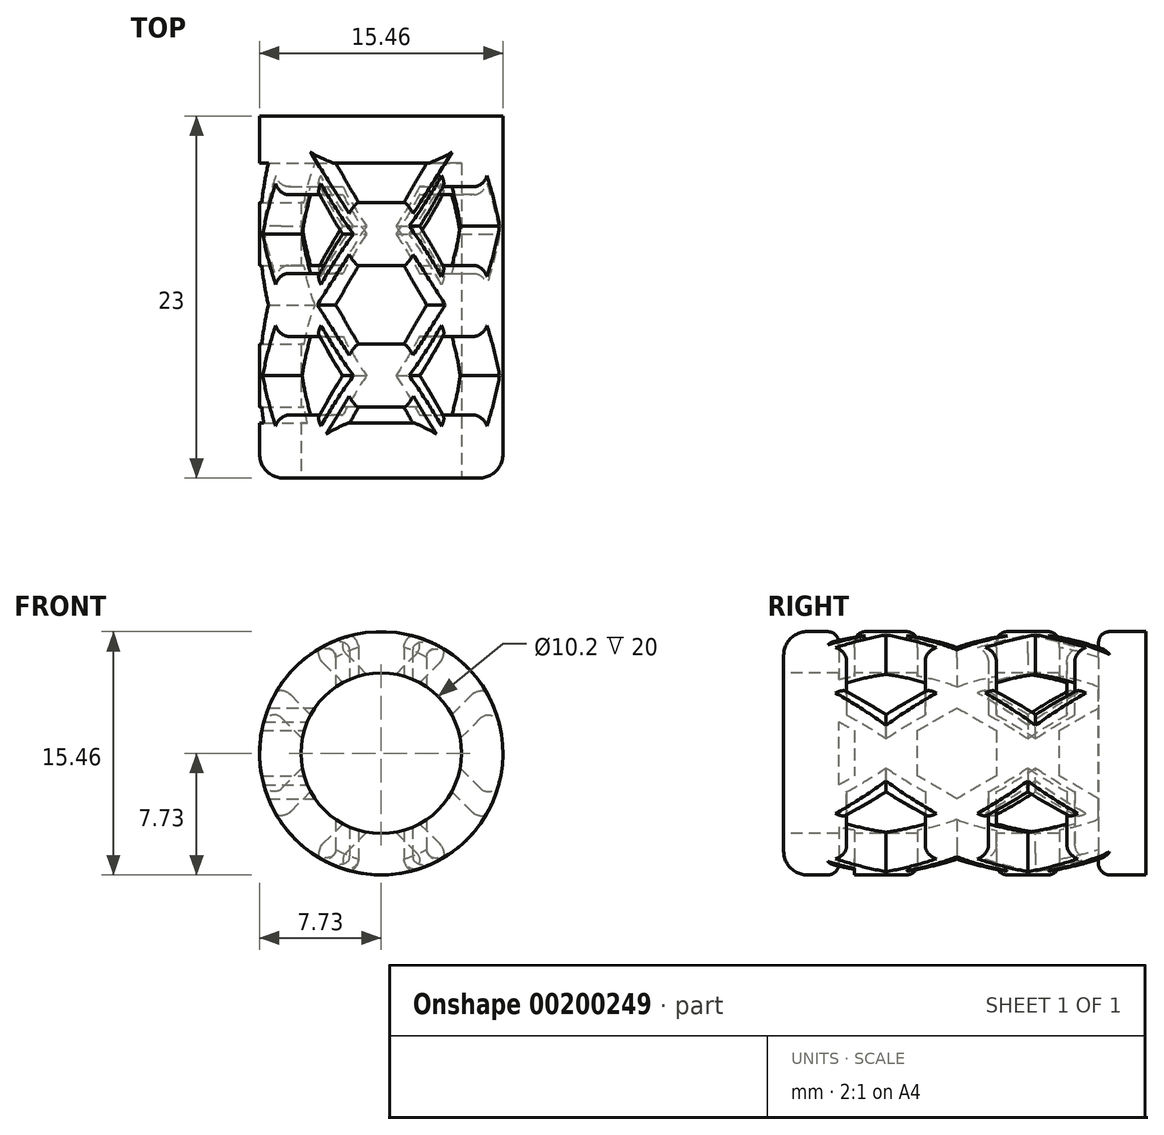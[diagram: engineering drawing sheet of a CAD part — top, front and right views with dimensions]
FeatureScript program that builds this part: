
annotation { "Feature Type Name" : "Feature", "Feature Type Description" : "" }
export const myFeature = defineFeature(function(context is Context, id is Id, definition is map)
    precondition{}
    {
        {
            var Q0;
            Q0=qCreatedBy(makeId("Front.planeOp"),FACE);
            var sketch = newSketch(context, id + "F0", { "sketchPlane" : qUnion([Q0])});
            skCircle(sketch, "E0", {"center": v(0, 0) * mm, "radius": 7.73 * mm});
            skSolve(sketch);
        }
        {
            var Q0;
            Q0=makeQuery(id+"F0.imprint","IMPRINT",FACE,{"disambiguationData":[TD([[makeQuery(id+"F0.imprint","IMPRINT",EDGE,{"derivedFrom":sQuery(id+"F0.wireOp",EDGE,"E0")}),1.0]])]});
            extrude(context, id + "F1", {"entities" : qUnion([Q0]), "oppositeDirection" : true, "depth" : 23 * mm, "offsetDistance" : 25 * mm});
        }
        {
            var Q0;
            Q0=makeQuery(id+"F1.opExtrude","CAP_FACE",FACE,{"disambiguationData":[OSD([sQuery(id+"F0.wireOp",EDGE,"E0")])],"isStart":true});
            var sketch = newSketch(context, id + "F2", { "sketchPlane" : qUnion([Q0])});
            skCircle(sketch, "E1", {"center": v(0, 0) * mm, "radius": 5.1 * mm});
            skSolve(sketch);
        }
        {
            var Q0;
            Q0=qSketchRegion(id+"F2",true);
            extrude(context, id + "F3", {"entities" : qUnion([Q0]), "operationType" : NewBodyOperationType.REMOVE, "oppositeDirection" : true, "depth" : 20 * mm, "offsetDistance" : 25 * mm});
        }
        {
            var Q0;
            Q0=qCreatedBy(makeId("Top.planeOp"),FACE);
            var sketch = newSketch(context, id + "F4", { "sketchPlane" : qUnion([Q0])});
            skLineSegment(sketch, "E2", {"start": v(0, 0) * mm, "end": v(0, 6.5) * mm, "construction": true});
            skLineSegment(sketch, "E3", {"start": v(0, 6.5) * mm, "end": v(0, 9) * mm, "construction": true});
            skCircle(sketch, "E4.cCircle", {"center": v(0, 6.5) * mm, "radius": 2.5 * mm, "construction": true});
            skLineSegment(sketch, "E4.0", {"start": v(-1.44, 9) * mm, "end": v(1.44, 9) * mm});
            skLineSegment(sketch, "E4.1", {"start": v(1.44, 9) * mm, "end": v(2.89, 6.5) * mm});
            skLineSegment(sketch, "E4.2", {"start": v(2.89, 6.5) * mm, "end": v(1.44, 4) * mm});
            skLineSegment(sketch, "E4.3", {"start": v(1.44, 4) * mm, "end": v(-1.44, 4) * mm});
            skLineSegment(sketch, "E4.4", {"start": v(-1.44, 4) * mm, "end": v(-2.89, 6.5) * mm});
            skLineSegment(sketch, "E4.5", {"start": v(-2.89, 6.5) * mm, "end": v(-1.44, 9) * mm});
            skPoint(sketch, "E4.0.midPoint", {"position": v(0, 9) * mm});
            skLineSegment(sketch, "E5.0.1.0", {"start": v(-2.89, 15.5) * mm, "end": v(-1.44, 18) * mm});
            skLineSegment(sketch, "E5.0.1.1", {"start": v(1.44, 13) * mm, "end": v(-1.44, 13) * mm});
            skLineSegment(sketch, "E5.0.1.2", {"start": v(2.89, 15.5) * mm, "end": v(1.44, 13) * mm});
            skLineSegment(sketch, "E5.0.1.3", {"start": v(1.44, 18) * mm, "end": v(2.89, 15.5) * mm});
            skLineSegment(sketch, "E5.0.1.4", {"start": v(-1.44, 18) * mm, "end": v(1.44, 18) * mm});
            skLineSegment(sketch, "E5.0.1.5", {"start": v(0, 15.5) * mm, "end": v(0, 18) * mm, "construction": true});
            skPoint(sketch, "E5.0.1.6", {"position": v(0, 18) * mm});
            skLineSegment(sketch, "E5.0.1.7", {"start": v(-1.44, 13) * mm, "end": v(-2.89, 15.5) * mm});
            skCircle(sketch, "E5.0.1.8", {"center": v(0, 15.5) * mm, "radius": 2.5 * mm, "construction": true});
            skLineSegment(sketch, "E5.direction1", {"start": v(-1.44, 4) * mm, "end": v(23.56, 4) * mm, "construction": true});
            skLineSegment(sketch, "E5.direction2", {"start": v(-1.44, 4) * mm, "end": v(-1.44, 13) * mm, "construction": true});
            skSolve(sketch);
        }
        {
            var Q0;
            Q0=qSketchRegion(id+"F4",true);
            extrude(context, id + "F5", {"entities" : qUnion([Q0]), "operationType" : NewBodyOperationType.REMOVE, "endBound" : BoundingType.SYMMETRIC, "depth" : 25 * mm});
        }
        {
            var Q0;
            Q0=qCreatedBy(makeId("Right.planeOp"),FACE);
            var sketch = newSketch(context, id + "F6", { "sketchPlane" : qUnion([Q0])});
            skLineSegment(sketch, "E6", {"start": v(0, 0) * mm, "end": v(6.5, 0) * mm, "construction": true});
            skLineSegment(sketch, "E7", {"start": v(6.5, 0) * mm, "end": v(9, 0) * mm, "construction": true});
            skCircle(sketch, "E8.cCircle", {"center": v(6.5, 0) * mm, "radius": 2.5 * mm, "construction": true});
            skLineSegment(sketch, "E8.0", {"start": v(9, 1.44) * mm, "end": v(9, -1.44) * mm});
            skLineSegment(sketch, "E8.1", {"start": v(9, -1.44) * mm, "end": v(6.5, -2.89) * mm});
            skLineSegment(sketch, "E8.2", {"start": v(6.5, -2.89) * mm, "end": v(4, -1.44) * mm});
            skLineSegment(sketch, "E8.3", {"start": v(4, -1.44) * mm, "end": v(4, 1.44) * mm});
            skLineSegment(sketch, "E8.4", {"start": v(4, 1.44) * mm, "end": v(6.5, 2.89) * mm});
            skLineSegment(sketch, "E8.5", {"start": v(6.5, 2.89) * mm, "end": v(9, 1.44) * mm});
            skPoint(sketch, "E8.0.midPoint", {"position": v(9, 0) * mm});
            skLineSegment(sketch, "E9", {"start": v(9, 0) * mm, "end": v(13.5, 0) * mm, "construction": true});
            skLineSegment(sketch, "E10", {"start": v(13.5, 0) * mm, "end": v(16, 0) * mm, "construction": true});
            skCircle(sketch, "E11.cCircle", {"center": v(16, 0) * mm, "radius": 2.5 * mm, "construction": true});
            skLineSegment(sketch, "E11.0", {"start": v(13.5, -1.44) * mm, "end": v(13.5, 1.44) * mm});
            skLineSegment(sketch, "E11.1", {"start": v(13.5, 1.44) * mm, "end": v(16, 2.89) * mm});
            skLineSegment(sketch, "E11.2", {"start": v(16, 2.89) * mm, "end": v(18.5, 1.44) * mm});
            skLineSegment(sketch, "E11.3", {"start": v(18.5, 1.44) * mm, "end": v(18.5, -1.44) * mm});
            skLineSegment(sketch, "E11.4", {"start": v(18.5, -1.44) * mm, "end": v(16, -2.89) * mm});
            skLineSegment(sketch, "E11.5", {"start": v(16, -2.89) * mm, "end": v(13.5, -1.44) * mm});
            skPoint(sketch, "E11.0.midPoint", {"position": v(13.5, 0) * mm});
            skSolve(sketch);
        }
        {
            var Q0;
            Q0=qSketchRegion(id+"F6",true);
            extrude(context, id + "F7", {"entities" : qUnion([Q0]), "operationType" : NewBodyOperationType.REMOVE, "endBound" : BoundingType.SYMMETRIC, "oppositeDirection" : true, "depth" : 25 * mm});
        }
        {
            var Q0;
            Q0=makeQuery(id+"F1.opExtrude","SWEPT_BODY",BODY,{"disambiguationData":[OSD([sQuery(id+"F0.wireOp",EDGE,"E0")])]});
            var Q1;
            Q1=makeQuery(id+"F1.opExtrude","SWEPT_FACE",FACE,{"disambiguationData":[OSD([sQuery(id+"F0.wireOp",EDGE,"E0")])]});
            transform(context, id + "F8", {"entities" : qUnion([Q0]), "transformType" : TransformType.ROTATION, "transformAxis" : qUnion([Q1]), "angle" : 45 * degree, "makeCopy" : false});
        }
        {
            var Q0;
            Q0=qCreatedBy(makeId("Top.planeOp"),FACE);
            var sketch = newSketch(context, id + "F9", { "sketchPlane" : qUnion([Q0])});
            skLineSegment(sketch, "E12", {"start": v(0, 0) * mm, "end": v(0, 11) * mm, "construction": true});
            skLineSegment(sketch, "E13", {"start": v(0, 11) * mm, "end": v(0, 13.5) * mm, "construction": true});
            skCircle(sketch, "E14.cCircle", {"center": v(0, 11) * mm, "radius": 2.5 * mm, "construction": true});
            skLineSegment(sketch, "E14.0", {"start": v(-1.44, 13.5) * mm, "end": v(1.44, 13.5) * mm});
            skLineSegment(sketch, "E14.1", {"start": v(1.44, 13.5) * mm, "end": v(2.89, 11) * mm});
            skLineSegment(sketch, "E14.2", {"start": v(2.89, 11) * mm, "end": v(1.44, 8.5) * mm});
            skLineSegment(sketch, "E14.3", {"start": v(1.44, 8.5) * mm, "end": v(-1.44, 8.5) * mm});
            skLineSegment(sketch, "E14.4", {"start": v(-1.44, 8.5) * mm, "end": v(-2.89, 11) * mm});
            skLineSegment(sketch, "E14.5", {"start": v(-2.89, 11) * mm, "end": v(-1.44, 13.5) * mm});
            skPoint(sketch, "E14.0.midPoint", {"position": v(0, 13.5) * mm});
            skLineSegment(sketch, "E15.0.1.0", {"start": v(0, 20) * mm, "end": v(0, 22.5) * mm, "construction": true});
            skPoint(sketch, "E15.0.1.1", {"position": v(0, 22.5) * mm});
            skLineSegment(sketch, "E15.0.1.2", {"start": v(1.44, 17.5) * mm, "end": v(-1.44, 17.5) * mm});
            skLineSegment(sketch, "E15.0.1.3", {"start": v(2.89, 20) * mm, "end": v(1.44, 17.5) * mm});
            skLineSegment(sketch, "E15.0.1.6", {"start": v(-1.44, 17.5) * mm, "end": v(-2.89, 20) * mm});
            skCircle(sketch, "E15.0.1.8", {"center": v(0, 20) * mm, "radius": 2.5 * mm, "construction": true});
            skLineSegment(sketch, "E15.direction1", {"start": v(-1.44, 8.5) * mm, "end": v(23.56, 8.5) * mm, "construction": true});
            skLineSegment(sketch, "E15.direction2", {"start": v(-1.44, 8.5) * mm, "end": v(-1.44, 17.5) * mm, "construction": true});
            skLineSegment(sketch, "E16", {"start": v(0, 119) * mm, "end": v(0, 128) * mm, "construction": true});
            skCircle(sketch, "E17.cCircle", {"center": v(0, 128) * mm, "radius": 2.5 * mm, "construction": true});
            skLineSegment(sketch, "E17.3", {"start": v(1.44, 125.5) * mm, "end": v(-1.44, 125.5) * mm});
            skPoint(sketch, "E17.0.midPoint", {"position": v(0, 130.5) * mm});
            skLineSegment(sketch, "E18", {"start": v(0, 126.5) * mm, "end": v(0, 125.5) * mm, "construction": true});
            skLineSegment(sketch, "E19", {"start": v(0, 126.5) * mm, "end": v(2, 126.5) * mm});
            skLineSegment(sketch, "E20", {"start": v(0, 126.5) * mm, "end": v(-2, 126.5) * mm});
            skLineSegment(sketch, "E21", {"start": v(-2, 126.5) * mm, "end": v(-1.44, 125.5) * mm});
            skLineSegment(sketch, "E22", {"start": v(1.44, 125.5) * mm, "end": v(2, 126.5) * mm});
            skLineSegment(sketch, "E23", {"start": v(0, 11) * mm, "end": v(0, 2) * mm, "construction": true});
            skCircle(sketch, "E24.cCircle", {"center": v(0, 2) * mm, "radius": 2.5 * mm, "construction": true});
            skLineSegment(sketch, "E24.3", {"start": v(-1.44, 4.5) * mm, "end": v(1.44, 4.5) * mm});
            skPoint(sketch, "E24.0.midPoint", {"position": v(0, -0.5) * mm});
            skLineSegment(sketch, "E25", {"start": v(0, 3.5) * mm, "end": v(0, 4.5) * mm, "construction": true});
            skLineSegment(sketch, "E26", {"start": v(0, 3.5) * mm, "end": v(-2, 3.5) * mm});
            skLineSegment(sketch, "E27", {"start": v(0, 3.5) * mm, "end": v(2, 3.5) * mm});
            skLineSegment(sketch, "E28", {"start": v(-2, 3.5) * mm, "end": v(-1.44, 4.5) * mm});
            skLineSegment(sketch, "E29", {"start": v(2, 3.5) * mm, "end": v(1.44, 4.5) * mm});
            skLineSegment(sketch, "E30", {"start": v(2.89, 20) * mm, "end": v(-2.89, 20) * mm});
            skSolve(sketch);
        }
        {
            var Q0;
            Q0=qSketchRegion(id+"F9",true);
            extrude(context, id + "F10", {"entities" : qUnion([Q0]), "operationType" : NewBodyOperationType.REMOVE, "endBound" : BoundingType.SYMMETRIC, "depth" : 25 * mm});
        }
        {
            var Q0;
            Q0=qCreatedBy(makeId("Right.planeOp"),FACE);
            var sketch = newSketch(context, id + "F11", { "sketchPlane" : qUnion([Q0])});
            skLineSegment(sketch, "E31", {"start": v(0, 0) * mm, "end": v(11, 0) * mm, "construction": true});
            skLineSegment(sketch, "E32", {"start": v(13.5, 0) * mm, "end": v(11, 0) * mm, "construction": true});
            skCircle(sketch, "E33.cCircle", {"center": v(11, 0) * mm, "radius": 2.5 * mm, "construction": true});
            skLineSegment(sketch, "E33.0", {"start": v(13.5, 1.44) * mm, "end": v(13.5, -1.44) * mm});
            skLineSegment(sketch, "E33.1", {"start": v(13.5, -1.44) * mm, "end": v(11, -2.89) * mm});
            skLineSegment(sketch, "E33.2", {"start": v(11, -2.89) * mm, "end": v(8.5, -1.44) * mm});
            skLineSegment(sketch, "E33.3", {"start": v(8.5, -1.44) * mm, "end": v(8.5, 1.44) * mm});
            skLineSegment(sketch, "E33.4", {"start": v(8.5, 1.44) * mm, "end": v(11, 2.89) * mm});
            skLineSegment(sketch, "E33.5", {"start": v(11, 2.89) * mm, "end": v(13.5, 1.44) * mm});
            skPoint(sketch, "E33.0.midPoint", {"position": v(13.5, 0) * mm});
            skLineSegment(sketch, "E34", {"start": v(13.5, 0) * mm, "end": v(20, 0) * mm, "construction": true});
            skLineSegment(sketch, "E35", {"start": v(20, 0) * mm, "end": v(22.5, 0) * mm, "construction": true});
            skCircle(sketch, "E36.cCircle", {"center": v(20, 0) * mm, "radius": 2.5 * mm, "construction": true});
            skLineSegment(sketch, "E36.2", {"start": v(20, -2.89) * mm, "end": v(17.5, -1.44) * mm});
            skLineSegment(sketch, "E36.3", {"start": v(17.5, -1.44) * mm, "end": v(17.5, 1.44) * mm});
            skLineSegment(sketch, "E36.4", {"start": v(17.5, 1.44) * mm, "end": v(20, 2.89) * mm});
            skPoint(sketch, "E36.0.midPoint", {"position": v(22.5, 0) * mm});
            skLineSegment(sketch, "E37", {"start": v(2, 0) * mm, "end": v(11, 0) * mm, "construction": true});
            skCircle(sketch, "E38.cCircle", {"center": v(2, 0) * mm, "radius": 2.5 * mm, "construction": true});
            skLineSegment(sketch, "E38.3", {"start": v(4.5, 1.44) * mm, "end": v(4.5, -1.44) * mm});
            skPoint(sketch, "E38.0.midPoint", {"position": v(-0.5, 0) * mm});
            skLineSegment(sketch, "E39", {"start": v(3.5, 0) * mm, "end": v(4.5, 0) * mm, "construction": true});
            skLineSegment(sketch, "E40", {"start": v(3.5, 0) * mm, "end": v(3.5, 2) * mm});
            skLineSegment(sketch, "E41", {"start": v(3.5, 0) * mm, "end": v(3.5, -2) * mm});
            skLineSegment(sketch, "E42", {"start": v(3.5, 2) * mm, "end": v(4.5, 1.44) * mm});
            skLineSegment(sketch, "E43", {"start": v(3.5, -2) * mm, "end": v(4.5, -1.44) * mm});
            skLineSegment(sketch, "E44", {"start": v(20, 2.89) * mm, "end": v(20, -2.89) * mm});
            skSolve(sketch);
        }
        {
            var Q0;
            Q0=qSketchRegion(id+"F11",true);
            extrude(context, id + "F12", {"entities" : qUnion([Q0]), "operationType" : NewBodyOperationType.REMOVE, "oppositeDirection" : true, "depth" : 25 * mm});
        }
        {
            var Q0;
            Q0=makeQuery(id+"F1.opExtrude","CAP_EDGE",EDGE,{"disambiguationData":[OSD([sQuery(id+"F0.wireOp",EDGE,"E0")])],"isStart":true});
            fillet(context, id + "F13", {"entities" : qUnion([Q0]), "radius" : 1.5 * mm, "tangentPropagation" : true, "allowEdgeOverflow" : false});
        }
        {
            var Q0;
            Q0=makeQuery(id+"F5.boolean.opBoolean","INTERSECT",EDGE,{"disambiguationData":[OD(0.0)],"derivedFrom":[makeQuery(id+"F1.opExtrude","SWEPT_FACE",FACE,{"disambiguationData":[OSD([sQuery(id+"F0.wireOp",EDGE,"E0")])]}),makeQuery(id+"F5.opExtrude","SWEPT_FACE",FACE,{"disambiguationData":[OSD([sQuery(id+"F4.wireOp",EDGE,"b579cf08-57c8-4be4-a64a-6a7c8f7f1ba5")])]})]});
            var Q1;
            Q1=makeQuery(id+"F5.boolean.opBoolean","INTERSECT",EDGE,{"disambiguationData":[OD(0.0)],"derivedFrom":[makeQuery(id+"F1.opExtrude","SWEPT_FACE",FACE,{"disambiguationData":[OSD([sQuery(id+"F0.wireOp",EDGE,"E0")])]}),makeQuery(id+"F5.opExtrude","SWEPT_FACE",FACE,{"disambiguationData":[OSD([sQuery(id+"F4.wireOp",EDGE,"bcb0f5b9-98e4-4035-bb5b-1a8c92403a19")])]})]});
            var Q2;
            Q2=makeQuery(id+"F5.boolean.opBoolean","INTERSECT",EDGE,{"disambiguationData":[OD(0.0)],"derivedFrom":[makeQuery(id+"F1.opExtrude","SWEPT_FACE",FACE,{"disambiguationData":[OSD([sQuery(id+"F0.wireOp",EDGE,"E0")])]}),makeQuery(id+"F5.opExtrude","SWEPT_FACE",FACE,{"disambiguationData":[OSD([sQuery(id+"F4.wireOp",EDGE,"09477fc4-9d29-4f20-8901-aec53dcd1546")])]})]});
            var Q3;
            Q3=makeQuery(id+"F5.boolean.opBoolean","INTERSECT",EDGE,{"disambiguationData":[OD(0.0)],"derivedFrom":[makeQuery(id+"F1.opExtrude","SWEPT_FACE",FACE,{"disambiguationData":[OSD([sQuery(id+"F0.wireOp",EDGE,"E0")])]}),makeQuery(id+"F5.opExtrude","SWEPT_FACE",FACE,{"disambiguationData":[OSD([sQuery(id+"F4.wireOp",EDGE,"92af876a-0958-4a7c-97b2-f4e8acbef095")])]})]});
            var Q4;
            Q4=makeQuery(id+"F5.boolean.opBoolean","INTERSECT",EDGE,{"disambiguationData":[OD(0.0)],"derivedFrom":[makeQuery(id+"F1.opExtrude","SWEPT_FACE",FACE,{"disambiguationData":[OSD([sQuery(id+"F0.wireOp",EDGE,"E0")])]}),makeQuery(id+"F5.opExtrude","SWEPT_FACE",FACE,{"disambiguationData":[OSD([sQuery(id+"F4.wireOp",EDGE,"67b481ec-10fe-46d3-8faa-ebe6010fe4f1")])]})]});
            var Q5;
            Q5=makeQuery(id+"F5.boolean.opBoolean","INTERSECT",EDGE,{"disambiguationData":[OD(0.0)],"derivedFrom":[makeQuery(id+"F1.opExtrude","SWEPT_FACE",FACE,{"disambiguationData":[OSD([sQuery(id+"F0.wireOp",EDGE,"E0")])]}),makeQuery(id+"F5.opExtrude","SWEPT_FACE",FACE,{"disambiguationData":[OSD([sQuery(id+"F4.wireOp",EDGE,"aca02d5f-46a9-486e-88e3-eb9aae4273e8")])]})]});
            var Q6;
            Q6=makeQuery(id+"F5.boolean.opBoolean","INTERSECT",EDGE,{"disambiguationData":[OD(0.0)],"derivedFrom":[makeQuery(id+"F1.opExtrude","SWEPT_FACE",FACE,{"disambiguationData":[OSD([sQuery(id+"F0.wireOp",EDGE,"E0")])]}),makeQuery(id+"F5.opExtrude","SWEPT_FACE",FACE,{"disambiguationData":[OSD([sQuery(id+"F4.wireOp",EDGE,"76385219-3691-4f38-9da5-edf1140a4629")])]})]});
            var Q7;
            Q7=makeQuery(id+"F5.boolean.opBoolean","INTERSECT",EDGE,{"disambiguationData":[OD(0.0)],"derivedFrom":[makeQuery(id+"F1.opExtrude","SWEPT_FACE",FACE,{"disambiguationData":[OSD([sQuery(id+"F0.wireOp",EDGE,"E0")])]}),makeQuery(id+"F5.opExtrude","SWEPT_FACE",FACE,{"disambiguationData":[OSD([sQuery(id+"F4.wireOp",EDGE,"30311b2f-ed17-4601-a199-a8278ef993fb")])]})]});
            var Q8;
            Q8=makeQuery(id+"F5.boolean.opBoolean","INTERSECT",EDGE,{"disambiguationData":[OD(0.0)],"derivedFrom":[makeQuery(id+"F1.opExtrude","SWEPT_FACE",FACE,{"disambiguationData":[OSD([sQuery(id+"F0.wireOp",EDGE,"E0")])]}),makeQuery(id+"F5.opExtrude","SWEPT_FACE",FACE,{"disambiguationData":[OSD([sQuery(id+"F4.wireOp",EDGE,"ed008b68-955d-4315-9cc0-8abb2c6860b0")])]})]});
            var Q9;
            Q9=makeQuery(id+"F5.boolean.opBoolean","INTERSECT",EDGE,{"disambiguationData":[OD(0.0)],"derivedFrom":[makeQuery(id+"F1.opExtrude","SWEPT_FACE",FACE,{"disambiguationData":[OSD([sQuery(id+"F0.wireOp",EDGE,"E0")])]}),makeQuery(id+"F5.opExtrude","SWEPT_FACE",FACE,{"disambiguationData":[OSD([sQuery(id+"F4.wireOp",EDGE,"efc5e5b1-0746-45f0-90e3-bd883f3492f4")])]})]});
            var Q10;
            Q10=makeQuery(id+"F5.boolean.opBoolean","INTERSECT",EDGE,{"disambiguationData":[OD(0.0)],"derivedFrom":[makeQuery(id+"F1.opExtrude","SWEPT_FACE",FACE,{"disambiguationData":[OSD([sQuery(id+"F0.wireOp",EDGE,"E0")])]}),makeQuery(id+"F5.opExtrude","SWEPT_FACE",FACE,{"disambiguationData":[OSD([sQuery(id+"F4.wireOp",EDGE,"562b9cc4-530f-4157-bc84-2c37910fa221")])]})]});
            var Q11;
            Q11=makeQuery(id+"F5.boolean.opBoolean","INTERSECT",EDGE,{"disambiguationData":[OD(0.0)],"derivedFrom":[makeQuery(id+"F1.opExtrude","SWEPT_FACE",FACE,{"disambiguationData":[OSD([sQuery(id+"F0.wireOp",EDGE,"E0")])]}),makeQuery(id+"F5.opExtrude","SWEPT_FACE",FACE,{"disambiguationData":[OSD([sQuery(id+"F4.wireOp",EDGE,"ab9f0dd0-8a88-45b5-9e6c-47f07906d12f")])]})]});
            var Q12;
            Q12=makeQuery(id+"F5.boolean.opBoolean","INTERSECT",EDGE,{"disambiguationData":[OD(0.0)],"derivedFrom":[makeQuery(id+"F1.opExtrude","SWEPT_FACE",FACE,{"disambiguationData":[OSD([sQuery(id+"F0.wireOp",EDGE,"E0")])]}),makeQuery(id+"F5.opExtrude","SWEPT_FACE",FACE,{"disambiguationData":[OSD([sQuery(id+"F4.wireOp",EDGE,"5e54ec67-0438-4ccb-ab1e-fb0c5627ff7a")])]})]});
            var Q13;
            Q13=makeQuery(id+"F5.boolean.opBoolean","INTERSECT",EDGE,{"disambiguationData":[OD(0.0)],"derivedFrom":[makeQuery(id+"F1.opExtrude","SWEPT_FACE",FACE,{"disambiguationData":[OSD([sQuery(id+"F0.wireOp",EDGE,"E0")])]}),makeQuery(id+"F5.opExtrude","SWEPT_FACE",FACE,{"disambiguationData":[OSD([sQuery(id+"F4.wireOp",EDGE,"1da9000e-137c-457e-9dd6-58b65176467c")])]})]});
            var Q14;
            Q14=makeQuery(id+"F5.boolean.opBoolean","INTERSECT",EDGE,{"disambiguationData":[OD(0.0)],"derivedFrom":[makeQuery(id+"F1.opExtrude","SWEPT_FACE",FACE,{"disambiguationData":[OSD([sQuery(id+"F0.wireOp",EDGE,"E0")])]}),makeQuery(id+"F5.opExtrude","SWEPT_FACE",FACE,{"disambiguationData":[OSD([sQuery(id+"F4.wireOp",EDGE,"15ec9440-3994-4756-befc-73e6937f9073")])]})]});
            var Q15;
            Q15=makeQuery(id+"F5.boolean.opBoolean","INTERSECT",EDGE,{"disambiguationData":[OD(0.0)],"derivedFrom":[makeQuery(id+"F1.opExtrude","SWEPT_FACE",FACE,{"disambiguationData":[OSD([sQuery(id+"F0.wireOp",EDGE,"E0")])]}),makeQuery(id+"F5.opExtrude","SWEPT_FACE",FACE,{"disambiguationData":[OSD([sQuery(id+"F4.wireOp",EDGE,"70ca714e-c3bb-4dc2-844f-e69955e1961d")])]})]});
            var Q16;
            Q16=makeQuery(id+"F5.boolean.opBoolean","INTERSECT",EDGE,{"disambiguationData":[OD(0.0)],"derivedFrom":[makeQuery(id+"F1.opExtrude","SWEPT_FACE",FACE,{"disambiguationData":[OSD([sQuery(id+"F0.wireOp",EDGE,"E0")])]}),makeQuery(id+"F5.opExtrude","SWEPT_FACE",FACE,{"disambiguationData":[OSD([sQuery(id+"F4.wireOp",EDGE,"b9a5c8a8-e1c1-4ccb-a6a4-30bc00998619")])]})]});
            var Q17;
            Q17=makeQuery(id+"F5.boolean.opBoolean","INTERSECT",EDGE,{"disambiguationData":[OD(0.0)],"derivedFrom":[makeQuery(id+"F1.opExtrude","SWEPT_FACE",FACE,{"disambiguationData":[OSD([sQuery(id+"F0.wireOp",EDGE,"E0")])]}),makeQuery(id+"F5.opExtrude","SWEPT_FACE",FACE,{"disambiguationData":[OSD([sQuery(id+"F4.wireOp",EDGE,"66c2d1b9-9082-457f-8158-46fefb0d0b5d")])]})]});
            var Q18;
            Q18=makeQuery(id+"F5.boolean.opBoolean","INTERSECT",EDGE,{"disambiguationData":[OD(0.0)],"derivedFrom":[makeQuery(id+"F1.opExtrude","SWEPT_FACE",FACE,{"disambiguationData":[OSD([sQuery(id+"F0.wireOp",EDGE,"E0")])]}),makeQuery(id+"F5.opExtrude","SWEPT_FACE",FACE,{"disambiguationData":[OSD([sQuery(id+"F4.wireOp",EDGE,"fd9b85d0-086e-4753-9286-7d80f3d11dd9")])]})]});
            var Q19;
            Q19=makeQuery(id+"F5.boolean.opBoolean","INTERSECT",EDGE,{"disambiguationData":[OD(0.0)],"derivedFrom":[makeQuery(id+"F1.opExtrude","SWEPT_FACE",FACE,{"disambiguationData":[OSD([sQuery(id+"F0.wireOp",EDGE,"E0")])]}),makeQuery(id+"F5.opExtrude","SWEPT_FACE",FACE,{"disambiguationData":[OSD([sQuery(id+"F4.wireOp",EDGE,"82180203-eaff-47f3-b606-d8d7c32d142f")])]})]});
            var Q20;
            Q20=makeQuery(id+"F5.boolean.opBoolean","INTERSECT",EDGE,{"disambiguationData":[OD(0.0)],"derivedFrom":[makeQuery(id+"F1.opExtrude","SWEPT_FACE",FACE,{"disambiguationData":[OSD([sQuery(id+"F0.wireOp",EDGE,"E0")])]}),makeQuery(id+"F5.opExtrude","SWEPT_FACE",FACE,{"disambiguationData":[OSD([sQuery(id+"F4.wireOp",EDGE,"536ab4de-4fb2-4d7d-9807-1d714ccadb66")])]})]});
            var Q21;
            Q21=makeQuery(id+"F5.boolean.opBoolean","INTERSECT",EDGE,{"disambiguationData":[OD(0.0)],"derivedFrom":[makeQuery(id+"F1.opExtrude","SWEPT_FACE",FACE,{"disambiguationData":[OSD([sQuery(id+"F0.wireOp",EDGE,"E0")])]}),makeQuery(id+"F5.opExtrude","SWEPT_FACE",FACE,{"disambiguationData":[OSD([sQuery(id+"F4.wireOp",EDGE,"c5cda94b-8dbb-4131-8629-d94229ce36f8")])]})]});
            var Q22;
            Q22=makeQuery(id+"F5.boolean.opBoolean","INTERSECT",EDGE,{"disambiguationData":[OD(0.0)],"derivedFrom":[makeQuery(id+"F1.opExtrude","SWEPT_FACE",FACE,{"disambiguationData":[OSD([sQuery(id+"F0.wireOp",EDGE,"E0")])]}),makeQuery(id+"F5.opExtrude","SWEPT_FACE",FACE,{"disambiguationData":[OSD([sQuery(id+"F4.wireOp",EDGE,"b8538754-f3f1-4cf7-bfe9-078eb6985bef")])]})]});
            var Q23;
            Q23=makeQuery(id+"F5.boolean.opBoolean","INTERSECT",EDGE,{"disambiguationData":[OD(0.0)],"derivedFrom":[makeQuery(id+"F1.opExtrude","SWEPT_FACE",FACE,{"disambiguationData":[OSD([sQuery(id+"F0.wireOp",EDGE,"E0")])]}),makeQuery(id+"F5.opExtrude","SWEPT_FACE",FACE,{"disambiguationData":[OSD([sQuery(id+"F4.wireOp",EDGE,"9e1b2bd2-a8a3-4caa-b598-0f2db5d1325d")])]})]});
            var Q24;
            Q24=makeQuery(id+"F5.boolean.opBoolean","INTERSECT",EDGE,{"disambiguationData":[OD(0.0)],"derivedFrom":[makeQuery(id+"F1.opExtrude","SWEPT_FACE",FACE,{"disambiguationData":[OSD([sQuery(id+"F0.wireOp",EDGE,"E0")])]}),makeQuery(id+"F5.opExtrude","SWEPT_FACE",FACE,{"disambiguationData":[OSD([sQuery(id+"F4.wireOp",EDGE,"c0d87fc6-e010-4d73-961e-dfed47c8a1b3")])]})]});
            var Q25;
            Q25=makeQuery(id+"F5.boolean.opBoolean","INTERSECT",EDGE,{"disambiguationData":[OD(0.0)],"derivedFrom":[makeQuery(id+"F1.opExtrude","SWEPT_FACE",FACE,{"disambiguationData":[OSD([sQuery(id+"F0.wireOp",EDGE,"E0")])]}),makeQuery(id+"F5.opExtrude","SWEPT_FACE",FACE,{"disambiguationData":[OSD([sQuery(id+"F4.wireOp",EDGE,"14d064f9-5360-4d18-9d9e-82328bf9daba")])]})]});
            var Q26;
            Q26=makeQuery(id+"F5.boolean.opBoolean","INTERSECT",EDGE,{"disambiguationData":[OD(0.0)],"derivedFrom":[makeQuery(id+"F1.opExtrude","SWEPT_FACE",FACE,{"disambiguationData":[OSD([sQuery(id+"F0.wireOp",EDGE,"E0")])]}),makeQuery(id+"F5.opExtrude","SWEPT_FACE",FACE,{"disambiguationData":[OSD([sQuery(id+"F4.wireOp",EDGE,"b60fa973-c727-4668-bfa0-a1e16f7a99aa")])]})]});
            var Q27;
            Q27=makeQuery(id+"F5.boolean.opBoolean","INTERSECT",EDGE,{"disambiguationData":[OD(0.0)],"derivedFrom":[makeQuery(id+"F1.opExtrude","SWEPT_FACE",FACE,{"disambiguationData":[OSD([sQuery(id+"F0.wireOp",EDGE,"E0")])]}),makeQuery(id+"F5.opExtrude","SWEPT_FACE",FACE,{"disambiguationData":[OSD([sQuery(id+"F4.wireOp",EDGE,"978e1622-7887-4f07-a91b-81f9d5efcfbf")])]})]});
            var Q28;
            Q28=makeQuery(id+"F5.boolean.opBoolean","INTERSECT",EDGE,{"disambiguationData":[OD(0.0)],"derivedFrom":[makeQuery(id+"F1.opExtrude","SWEPT_FACE",FACE,{"disambiguationData":[OSD([sQuery(id+"F0.wireOp",EDGE,"E0")])]}),makeQuery(id+"F5.opExtrude","SWEPT_FACE",FACE,{"disambiguationData":[OSD([sQuery(id+"F4.wireOp",EDGE,"d0a2849f-a89e-4989-ab6e-8e188e140a90")])]})]});
            var Q29;
            Q29=makeQuery(id+"F5.boolean.opBoolean","INTERSECT",EDGE,{"disambiguationData":[OD(0.0)],"derivedFrom":[makeQuery(id+"F1.opExtrude","SWEPT_FACE",FACE,{"disambiguationData":[OSD([sQuery(id+"F0.wireOp",EDGE,"E0")])]}),makeQuery(id+"F5.opExtrude","SWEPT_FACE",FACE,{"disambiguationData":[OSD([sQuery(id+"F4.wireOp",EDGE,"f55199c0-7004-4acb-b4c7-226994b61401")])]})]});
            var Q30;
            Q30=makeQuery(id+"F5.boolean.opBoolean","INTERSECT",EDGE,{"disambiguationData":[OD(0.0)],"derivedFrom":[makeQuery(id+"F1.opExtrude","SWEPT_FACE",FACE,{"disambiguationData":[OSD([sQuery(id+"F0.wireOp",EDGE,"E0")])]}),makeQuery(id+"F5.opExtrude","SWEPT_FACE",FACE,{"disambiguationData":[OSD([sQuery(id+"F4.wireOp",EDGE,"8a1b3b7c-f627-453a-8324-eadb2e6b2aa6")])]})]});
            var Q31;
            Q31=makeQuery(id+"F5.boolean.opBoolean","INTERSECT",EDGE,{"disambiguationData":[OD(0.0)],"derivedFrom":[makeQuery(id+"F1.opExtrude","SWEPT_FACE",FACE,{"disambiguationData":[OSD([sQuery(id+"F0.wireOp",EDGE,"E0")])]}),makeQuery(id+"F5.opExtrude","SWEPT_FACE",FACE,{"disambiguationData":[OSD([sQuery(id+"F4.wireOp",EDGE,"d52b0a11-5b01-40f3-ab4f-3d3d9242be96")])]})]});
            var Q32;
            Q32=makeQuery(id+"F5.boolean.opBoolean","INTERSECT",EDGE,{"disambiguationData":[OD(0.0)],"derivedFrom":[makeQuery(id+"F1.opExtrude","SWEPT_FACE",FACE,{"disambiguationData":[OSD([sQuery(id+"F0.wireOp",EDGE,"E0")])]}),makeQuery(id+"F5.opExtrude","SWEPT_FACE",FACE,{"disambiguationData":[OSD([sQuery(id+"F4.wireOp",EDGE,"4d2b9fd0-2ce7-462d-91df-97fb973a0c3b")])]})]});
            var Q33;
            Q33=makeQuery(id+"F5.boolean.opBoolean","INTERSECT",EDGE,{"disambiguationData":[OD(0.0)],"derivedFrom":[makeQuery(id+"F1.opExtrude","SWEPT_FACE",FACE,{"disambiguationData":[OSD([sQuery(id+"F0.wireOp",EDGE,"E0")])]}),makeQuery(id+"F5.opExtrude","SWEPT_FACE",FACE,{"disambiguationData":[OSD([sQuery(id+"F4.wireOp",EDGE,"cdeb415e-409f-4668-ae01-d5015ff68174")])]})]});
            var Q34;
            Q34=makeQuery(id+"F5.boolean.opBoolean","INTERSECT",EDGE,{"disambiguationData":[OD(0.0)],"derivedFrom":[makeQuery(id+"F1.opExtrude","SWEPT_FACE",FACE,{"disambiguationData":[OSD([sQuery(id+"F0.wireOp",EDGE,"E0")])]}),makeQuery(id+"F5.opExtrude","SWEPT_FACE",FACE,{"disambiguationData":[OSD([sQuery(id+"F4.wireOp",EDGE,"f6bfe6da-8190-4625-8366-2eafc9149588")])]})]});
            var Q35;
            Q35=makeQuery(id+"F5.boolean.opBoolean","INTERSECT",EDGE,{"disambiguationData":[OD(0.0)],"derivedFrom":[makeQuery(id+"F1.opExtrude","SWEPT_FACE",FACE,{"disambiguationData":[OSD([sQuery(id+"F0.wireOp",EDGE,"E0")])]}),makeQuery(id+"F5.opExtrude","SWEPT_FACE",FACE,{"disambiguationData":[OSD([sQuery(id+"F4.wireOp",EDGE,"c79ec3c5-8163-43ca-85dc-8d9b1c829184")])]})]});
            var Q36;
            Q36=makeQuery(id+"F5.boolean.opBoolean","INTERSECT",EDGE,{"disambiguationData":[OD(0.0)],"derivedFrom":[makeQuery(id+"F1.opExtrude","SWEPT_FACE",FACE,{"disambiguationData":[OSD([sQuery(id+"F0.wireOp",EDGE,"E0")])]}),makeQuery(id+"F5.opExtrude","SWEPT_FACE",FACE,{"disambiguationData":[OSD([sQuery(id+"F4.wireOp",EDGE,"a3fb4c3e-2145-4d81-81b1-06ede13a7337")])]})]});
            var Q37;
            Q37=makeQuery(id+"F5.boolean.opBoolean","INTERSECT",EDGE,{"disambiguationData":[OD(0.0)],"derivedFrom":[makeQuery(id+"F1.opExtrude","SWEPT_FACE",FACE,{"disambiguationData":[OSD([sQuery(id+"F0.wireOp",EDGE,"E0")])]}),makeQuery(id+"F5.opExtrude","SWEPT_FACE",FACE,{"disambiguationData":[OSD([sQuery(id+"F4.wireOp",EDGE,"b0c4be78-8462-4223-a050-0597d47616df")])]})]});
            var Q38;
            Q38=makeQuery(id+"F5.boolean.opBoolean","INTERSECT",EDGE,{"disambiguationData":[OD(0.0)],"derivedFrom":[makeQuery(id+"F1.opExtrude","SWEPT_FACE",FACE,{"disambiguationData":[OSD([sQuery(id+"F0.wireOp",EDGE,"E0")])]}),makeQuery(id+"F5.opExtrude","SWEPT_FACE",FACE,{"disambiguationData":[OSD([sQuery(id+"F4.wireOp",EDGE,"b63d48e1-6cba-4484-95e4-232a2befb6ff")])]})]});
            var Q39;
            Q39=makeQuery(id+"F5.boolean.opBoolean","INTERSECT",EDGE,{"disambiguationData":[OD(0.0)],"derivedFrom":[makeQuery(id+"F1.opExtrude","SWEPT_FACE",FACE,{"disambiguationData":[OSD([sQuery(id+"F0.wireOp",EDGE,"E0")])]}),makeQuery(id+"F5.opExtrude","SWEPT_FACE",FACE,{"disambiguationData":[OSD([sQuery(id+"F4.wireOp",EDGE,"afbb9b2d-3fe8-4547-9304-fccae8a72bf5")])]})]});
            var Q40;
            Q40=makeQuery(id+"F5.boolean.opBoolean","INTERSECT",EDGE,{"disambiguationData":[OD(0.0)],"derivedFrom":[makeQuery(id+"F1.opExtrude","SWEPT_FACE",FACE,{"disambiguationData":[OSD([sQuery(id+"F0.wireOp",EDGE,"E0")])]}),makeQuery(id+"F5.opExtrude","SWEPT_FACE",FACE,{"disambiguationData":[OSD([sQuery(id+"F4.wireOp",EDGE,"17e898d8-84c7-47b4-8d53-d44f4836d596")])]})]});
            var Q41;
            Q41=makeQuery(id+"F5.boolean.opBoolean","INTERSECT",EDGE,{"disambiguationData":[OD(0.0)],"derivedFrom":[makeQuery(id+"F1.opExtrude","SWEPT_FACE",FACE,{"disambiguationData":[OSD([sQuery(id+"F0.wireOp",EDGE,"E0")])]}),makeQuery(id+"F5.opExtrude","SWEPT_FACE",FACE,{"disambiguationData":[OSD([sQuery(id+"F4.wireOp",EDGE,"0321eed8-d3a5-4dab-8f9f-a696995c0651")])]})]});
            var Q42;
            Q42=makeQuery(id+"F5.boolean.opBoolean","INTERSECT",EDGE,{"disambiguationData":[OD(0.0)],"derivedFrom":[makeQuery(id+"F1.opExtrude","SWEPT_FACE",FACE,{"disambiguationData":[OSD([sQuery(id+"F0.wireOp",EDGE,"E0")])]}),makeQuery(id+"F5.opExtrude","SWEPT_FACE",FACE,{"disambiguationData":[OSD([sQuery(id+"F4.wireOp",EDGE,"c4d35b72-aeb9-430e-9e73-853e9b0c76ec")])]})]});
            var Q43;
            Q43=makeQuery(id+"F5.boolean.opBoolean","INTERSECT",EDGE,{"disambiguationData":[OD(0.0)],"derivedFrom":[makeQuery(id+"F1.opExtrude","SWEPT_FACE",FACE,{"disambiguationData":[OSD([sQuery(id+"F0.wireOp",EDGE,"E0")])]}),makeQuery(id+"F5.opExtrude","SWEPT_FACE",FACE,{"disambiguationData":[OSD([sQuery(id+"F4.wireOp",EDGE,"dc280805-f6e6-449f-9c66-de12d14a6505")])]})]});
            var Q44;
            Q44=makeQuery(id+"F5.boolean.opBoolean","INTERSECT",EDGE,{"disambiguationData":[OD(0.0)],"derivedFrom":[makeQuery(id+"F1.opExtrude","SWEPT_FACE",FACE,{"disambiguationData":[OSD([sQuery(id+"F0.wireOp",EDGE,"E0")])]}),makeQuery(id+"F5.opExtrude","SWEPT_FACE",FACE,{"disambiguationData":[OSD([sQuery(id+"F4.wireOp",EDGE,"c3060930-26c4-4b07-9e4a-7a125c9e4bcc")])]})]});
            var Q45;
            Q45=makeQuery(id+"F5.boolean.opBoolean","INTERSECT",EDGE,{"disambiguationData":[OD(0.0)],"derivedFrom":[makeQuery(id+"F1.opExtrude","SWEPT_FACE",FACE,{"disambiguationData":[OSD([sQuery(id+"F0.wireOp",EDGE,"E0")])]}),makeQuery(id+"F5.opExtrude","SWEPT_FACE",FACE,{"disambiguationData":[OSD([sQuery(id+"F4.wireOp",EDGE,"c1b4e133-c4b8-441d-9ad6-da7bbba7f6e1")])]})]});
            var Q46;
            Q46=makeQuery(id+"F5.boolean.opBoolean","INTERSECT",EDGE,{"disambiguationData":[OD(0.0)],"derivedFrom":[makeQuery(id+"F1.opExtrude","SWEPT_FACE",FACE,{"disambiguationData":[OSD([sQuery(id+"F0.wireOp",EDGE,"E0")])]}),makeQuery(id+"F5.opExtrude","SWEPT_FACE",FACE,{"disambiguationData":[OSD([sQuery(id+"F4.wireOp",EDGE,"6482df09-691d-4fcb-8b92-72aa1eb952c4")])]})]});
            var Q47;
            Q47=makeQuery(id+"F5.boolean.opBoolean","INTERSECT",EDGE,{"disambiguationData":[OD(0.0)],"derivedFrom":[makeQuery(id+"F1.opExtrude","SWEPT_FACE",FACE,{"disambiguationData":[OSD([sQuery(id+"F0.wireOp",EDGE,"E0")])]}),makeQuery(id+"F5.opExtrude","SWEPT_FACE",FACE,{"disambiguationData":[OSD([sQuery(id+"F4.wireOp",EDGE,"c69de198-cab7-4a97-91da-0287aae22bb7")])]})]});
            var Q48;
            Q48=makeQuery(id+"F5.boolean.opBoolean","INTERSECT",EDGE,{"disambiguationData":[OD(0.0)],"derivedFrom":[makeQuery(id+"F1.opExtrude","SWEPT_FACE",FACE,{"disambiguationData":[OSD([sQuery(id+"F0.wireOp",EDGE,"E0")])]}),makeQuery(id+"F5.opExtrude","SWEPT_FACE",FACE,{"disambiguationData":[OSD([sQuery(id+"F4.wireOp",EDGE,"4dd2465f-f76c-4ed8-a0a4-661656c39b6e")])]})]});
            var Q49;
            Q49=makeQuery(id+"F5.boolean.opBoolean","INTERSECT",EDGE,{"disambiguationData":[OD(0.0)],"derivedFrom":[makeQuery(id+"F1.opExtrude","SWEPT_FACE",FACE,{"disambiguationData":[OSD([sQuery(id+"F0.wireOp",EDGE,"E0")])]}),makeQuery(id+"F5.opExtrude","SWEPT_FACE",FACE,{"disambiguationData":[OSD([sQuery(id+"F4.wireOp",EDGE,"981d5c34-8f63-4288-b664-c119c34ece28")])]})]});
            var Q50;
            Q50=makeQuery(id+"F5.boolean.opBoolean","INTERSECT",EDGE,{"disambiguationData":[OD(0.0)],"derivedFrom":[makeQuery(id+"F1.opExtrude","SWEPT_FACE",FACE,{"disambiguationData":[OSD([sQuery(id+"F0.wireOp",EDGE,"E0")])]}),makeQuery(id+"F5.opExtrude","SWEPT_FACE",FACE,{"disambiguationData":[OSD([sQuery(id+"F4.wireOp",EDGE,"4bb37bd6-656b-4624-b683-e77c2f51eea1")])]})]});
            var Q51;
            Q51=makeQuery(id+"F5.boolean.opBoolean","INTERSECT",EDGE,{"disambiguationData":[OD(0.0)],"derivedFrom":[makeQuery(id+"F1.opExtrude","SWEPT_FACE",FACE,{"disambiguationData":[OSD([sQuery(id+"F0.wireOp",EDGE,"E0")])]}),makeQuery(id+"F5.opExtrude","SWEPT_FACE",FACE,{"disambiguationData":[OSD([sQuery(id+"F4.wireOp",EDGE,"a7220ec3-3de3-437a-89c6-8f6e48a94db4")])]})]});
            var Q52;
            Q52=makeQuery(id+"F5.boolean.opBoolean","INTERSECT",EDGE,{"disambiguationData":[OD(0.0)],"derivedFrom":[makeQuery(id+"F1.opExtrude","SWEPT_FACE",FACE,{"disambiguationData":[OSD([sQuery(id+"F0.wireOp",EDGE,"E0")])]}),makeQuery(id+"F5.opExtrude","SWEPT_FACE",FACE,{"disambiguationData":[OSD([sQuery(id+"F4.wireOp",EDGE,"ad6a620c-f5ab-4820-8ed8-d40d38394706")])]})]});
            var Q53;
            Q53=makeQuery(id+"F5.boolean.opBoolean","INTERSECT",EDGE,{"disambiguationData":[OD(0.0)],"derivedFrom":[makeQuery(id+"F1.opExtrude","SWEPT_FACE",FACE,{"disambiguationData":[OSD([sQuery(id+"F0.wireOp",EDGE,"E0")])]}),makeQuery(id+"F5.opExtrude","SWEPT_FACE",FACE,{"disambiguationData":[OSD([sQuery(id+"F4.wireOp",EDGE,"941b1c59-87e7-468b-8371-b89298454958")])]})]});
            var Q54;
            Q54=makeQuery(id+"F5.boolean.opBoolean","INTERSECT",EDGE,{"disambiguationData":[OD(0.0)],"derivedFrom":[makeQuery(id+"F1.opExtrude","SWEPT_FACE",FACE,{"disambiguationData":[OSD([sQuery(id+"F0.wireOp",EDGE,"E0")])]}),makeQuery(id+"F5.opExtrude","SWEPT_FACE",FACE,{"disambiguationData":[OSD([sQuery(id+"F4.wireOp",EDGE,"bef314f7-3a79-43c5-a841-5e6a101abbee")])]})]});
            var Q55;
            Q55=makeQuery(id+"F5.boolean.opBoolean","INTERSECT",EDGE,{"disambiguationData":[OD(0.0)],"derivedFrom":[makeQuery(id+"F1.opExtrude","SWEPT_FACE",FACE,{"disambiguationData":[OSD([sQuery(id+"F0.wireOp",EDGE,"E0")])]}),makeQuery(id+"F5.opExtrude","SWEPT_FACE",FACE,{"disambiguationData":[OSD([sQuery(id+"F4.wireOp",EDGE,"0648dc57-717b-43e8-adf0-6dc20ff83d95")])]})]});
            var Q56;
            Q56=makeQuery(id+"F5.boolean.opBoolean","INTERSECT",EDGE,{"disambiguationData":[OD(0.0)],"derivedFrom":[makeQuery(id+"F1.opExtrude","SWEPT_FACE",FACE,{"disambiguationData":[OSD([sQuery(id+"F0.wireOp",EDGE,"E0")])]}),makeQuery(id+"F5.opExtrude","SWEPT_FACE",FACE,{"disambiguationData":[OSD([sQuery(id+"F4.wireOp",EDGE,"6b48d1a6-d9e0-4d44-864b-96c7a48616eb")])]})]});
            var Q57;
            Q57=makeQuery(id+"F5.boolean.opBoolean","INTERSECT",EDGE,{"disambiguationData":[OD(0.0)],"derivedFrom":[makeQuery(id+"F1.opExtrude","SWEPT_FACE",FACE,{"disambiguationData":[OSD([sQuery(id+"F0.wireOp",EDGE,"E0")])]}),makeQuery(id+"F5.opExtrude","SWEPT_FACE",FACE,{"disambiguationData":[OSD([sQuery(id+"F4.wireOp",EDGE,"0cab01fc-36dc-4ee5-8aad-b0ef9c2b601d")])]})]});
            var Q58;
            Q58=makeQuery(id+"F5.boolean.opBoolean","INTERSECT",EDGE,{"disambiguationData":[OD(0.0)],"derivedFrom":[makeQuery(id+"F1.opExtrude","SWEPT_FACE",FACE,{"disambiguationData":[OSD([sQuery(id+"F0.wireOp",EDGE,"E0")])]}),makeQuery(id+"F5.opExtrude","SWEPT_FACE",FACE,{"disambiguationData":[OSD([sQuery(id+"F4.wireOp",EDGE,"07e56c10-a22d-4a71-bd1c-05f810bbc1d3")])]})]});
            var Q59;
            Q59=makeQuery(id+"F5.boolean.opBoolean","INTERSECT",EDGE,{"disambiguationData":[OD(0.0)],"derivedFrom":[makeQuery(id+"F1.opExtrude","SWEPT_FACE",FACE,{"disambiguationData":[OSD([sQuery(id+"F0.wireOp",EDGE,"E0")])]}),makeQuery(id+"F5.opExtrude","SWEPT_FACE",FACE,{"disambiguationData":[OSD([sQuery(id+"F4.wireOp",EDGE,"537901f3-e070-42e2-b15a-1a2327522176")])]})]});
            var Q60;
            Q60=makeQuery(id+"F5.boolean.opBoolean","INTERSECT",EDGE,{"disambiguationData":[OD(0.0)],"derivedFrom":[makeQuery(id+"F1.opExtrude","SWEPT_FACE",FACE,{"disambiguationData":[OSD([sQuery(id+"F0.wireOp",EDGE,"E0")])]}),makeQuery(id+"F5.opExtrude","SWEPT_FACE",FACE,{"disambiguationData":[OSD([sQuery(id+"F4.wireOp",EDGE,"570eaa13-a835-4f5c-9393-ffbc36022b64")])]})]});
            var Q61;
            Q61=makeQuery(id+"F5.boolean.opBoolean","INTERSECT",EDGE,{"disambiguationData":[OD(0.0)],"derivedFrom":[makeQuery(id+"F1.opExtrude","SWEPT_FACE",FACE,{"disambiguationData":[OSD([sQuery(id+"F0.wireOp",EDGE,"E0")])]}),makeQuery(id+"F5.opExtrude","SWEPT_FACE",FACE,{"disambiguationData":[OSD([sQuery(id+"F4.wireOp",EDGE,"5e9c52b7-e873-4326-812b-35e100de69ae")])]})]});
            var Q62;
            Q62=makeQuery(id+"F5.boolean.opBoolean","INTERSECT",EDGE,{"disambiguationData":[OD(0.0)],"derivedFrom":[makeQuery(id+"F1.opExtrude","SWEPT_FACE",FACE,{"disambiguationData":[OSD([sQuery(id+"F0.wireOp",EDGE,"E0")])]}),makeQuery(id+"F5.opExtrude","SWEPT_FACE",FACE,{"disambiguationData":[OSD([sQuery(id+"F4.wireOp",EDGE,"2f2a9835-3d8d-43e3-8360-67f6976d79c8")])]})]});
            var Q63;
            Q63=makeQuery(id+"F5.boolean.opBoolean","INTERSECT",EDGE,{"disambiguationData":[OD(0.0)],"derivedFrom":[makeQuery(id+"F1.opExtrude","SWEPT_FACE",FACE,{"disambiguationData":[OSD([sQuery(id+"F0.wireOp",EDGE,"E0")])]}),makeQuery(id+"F5.opExtrude","SWEPT_FACE",FACE,{"disambiguationData":[OSD([sQuery(id+"F4.wireOp",EDGE,"6d0ddde6-eeae-473b-8fbb-40228edda87a")])]})]});
            var Q64;
            Q64=makeQuery(id+"F5.boolean.opBoolean","INTERSECT",EDGE,{"disambiguationData":[OD(0.0)],"derivedFrom":[makeQuery(id+"F1.opExtrude","SWEPT_FACE",FACE,{"disambiguationData":[OSD([sQuery(id+"F0.wireOp",EDGE,"E0")])]}),makeQuery(id+"F5.opExtrude","SWEPT_FACE",FACE,{"disambiguationData":[OSD([sQuery(id+"F4.wireOp",EDGE,"698e3026-83e8-4a96-89d8-85748f8eba81")])]})]});
            var Q65;
            Q65=makeQuery(id+"F5.boolean.opBoolean","INTERSECT",EDGE,{"disambiguationData":[OD(0.0)],"derivedFrom":[makeQuery(id+"F1.opExtrude","SWEPT_FACE",FACE,{"disambiguationData":[OSD([sQuery(id+"F0.wireOp",EDGE,"E0")])]}),makeQuery(id+"F5.opExtrude","SWEPT_FACE",FACE,{"disambiguationData":[OSD([sQuery(id+"F4.wireOp",EDGE,"7b01ac76-4f73-4855-90dc-ab2067377e7d")])]})]});
            var Q66;
            Q66=makeQuery(id+"F5.boolean.opBoolean","INTERSECT",EDGE,{"disambiguationData":[OD(0.0)],"derivedFrom":[makeQuery(id+"F1.opExtrude","SWEPT_FACE",FACE,{"disambiguationData":[OSD([sQuery(id+"F0.wireOp",EDGE,"E0")])]}),makeQuery(id+"F5.opExtrude","SWEPT_FACE",FACE,{"disambiguationData":[OSD([sQuery(id+"F4.wireOp",EDGE,"f2f599b8-f5a2-47e9-8bc0-b292fd8eaa36")])]})]});
            var Q67;
            Q67=makeQuery(id+"F5.boolean.opBoolean","INTERSECT",EDGE,{"disambiguationData":[OD(0.0)],"derivedFrom":[makeQuery(id+"F1.opExtrude","SWEPT_FACE",FACE,{"disambiguationData":[OSD([sQuery(id+"F0.wireOp",EDGE,"E0")])]}),makeQuery(id+"F5.opExtrude","SWEPT_FACE",FACE,{"disambiguationData":[OSD([sQuery(id+"F4.wireOp",EDGE,"cd1f4ce4-2bdf-46d9-add9-aa29dd8642a7")])]})]});
            var Q68;
            Q68=makeQuery(id+"F5.boolean.opBoolean","INTERSECT",EDGE,{"disambiguationData":[OD(0.0)],"derivedFrom":[makeQuery(id+"F1.opExtrude","SWEPT_FACE",FACE,{"disambiguationData":[OSD([sQuery(id+"F0.wireOp",EDGE,"E0")])]}),makeQuery(id+"F5.opExtrude","SWEPT_FACE",FACE,{"disambiguationData":[OSD([sQuery(id+"F4.wireOp",EDGE,"37a73c55-c155-4e62-8b34-27461510b276")])]})]});
            var Q69;
            Q69=makeQuery(id+"F5.boolean.opBoolean","INTERSECT",EDGE,{"disambiguationData":[OD(0.0)],"derivedFrom":[makeQuery(id+"F1.opExtrude","SWEPT_FACE",FACE,{"disambiguationData":[OSD([sQuery(id+"F0.wireOp",EDGE,"E0")])]}),makeQuery(id+"F5.opExtrude","SWEPT_FACE",FACE,{"disambiguationData":[OSD([sQuery(id+"F4.wireOp",EDGE,"70095d75-91cd-40af-a70f-813c3114abcc")])]})]});
            var Q70;
            Q70=makeQuery(id+"F5.boolean.opBoolean","INTERSECT",EDGE,{"disambiguationData":[OD(0.0)],"derivedFrom":[makeQuery(id+"F1.opExtrude","SWEPT_FACE",FACE,{"disambiguationData":[OSD([sQuery(id+"F0.wireOp",EDGE,"E0")])]}),makeQuery(id+"F5.opExtrude","SWEPT_FACE",FACE,{"disambiguationData":[OSD([sQuery(id+"F4.wireOp",EDGE,"82706a72-63eb-40cc-839c-e0d1195260aa")])]})]});
            var Q71;
            Q71=makeQuery(id+"F5.boolean.opBoolean","INTERSECT",EDGE,{"disambiguationData":[OD(0.0)],"derivedFrom":[makeQuery(id+"F1.opExtrude","SWEPT_FACE",FACE,{"disambiguationData":[OSD([sQuery(id+"F0.wireOp",EDGE,"E0")])]}),makeQuery(id+"F5.opExtrude","SWEPT_FACE",FACE,{"disambiguationData":[OSD([sQuery(id+"F4.wireOp",EDGE,"8ba90ffa-b527-484e-b8a8-654b458372bb")])]})]});
            var Q72;
            Q72=makeQuery(id+"F5.boolean.opBoolean","INTERSECT",EDGE,{"disambiguationData":[OD(0.0)],"derivedFrom":[makeQuery(id+"F1.opExtrude","SWEPT_FACE",FACE,{"disambiguationData":[OSD([sQuery(id+"F0.wireOp",EDGE,"E0")])]}),makeQuery(id+"F5.opExtrude","SWEPT_FACE",FACE,{"disambiguationData":[OSD([sQuery(id+"F4.wireOp",EDGE,"f230033e-8e97-4c48-a61c-878d7d3044cc")])]})]});
            var Q73;
            Q73=makeQuery(id+"F5.boolean.opBoolean","INTERSECT",EDGE,{"disambiguationData":[OD(0.0)],"derivedFrom":[makeQuery(id+"F1.opExtrude","SWEPT_FACE",FACE,{"disambiguationData":[OSD([sQuery(id+"F0.wireOp",EDGE,"E0")])]}),makeQuery(id+"F5.opExtrude","SWEPT_FACE",FACE,{"disambiguationData":[OSD([sQuery(id+"F4.wireOp",EDGE,"4144a65f-7927-494c-8b6f-a1137679e0c2")])]})]});
            var Q74;
            Q74=makeQuery(id+"F5.boolean.opBoolean","INTERSECT",EDGE,{"disambiguationData":[OD(0.0)],"derivedFrom":[makeQuery(id+"F1.opExtrude","SWEPT_FACE",FACE,{"disambiguationData":[OSD([sQuery(id+"F0.wireOp",EDGE,"E0")])]}),makeQuery(id+"F5.opExtrude","SWEPT_FACE",FACE,{"disambiguationData":[OSD([sQuery(id+"F4.wireOp",EDGE,"12fd482c-4469-40d2-a6f5-f27bb2f23065")])]})]});
            var Q75;
            Q75=makeQuery(id+"F5.boolean.opBoolean","INTERSECT",EDGE,{"disambiguationData":[OD(0.0)],"derivedFrom":[makeQuery(id+"F1.opExtrude","SWEPT_FACE",FACE,{"disambiguationData":[OSD([sQuery(id+"F0.wireOp",EDGE,"E0")])]}),makeQuery(id+"F5.opExtrude","SWEPT_FACE",FACE,{"disambiguationData":[OSD([sQuery(id+"F4.wireOp",EDGE,"068a08e4-cb17-442e-8f38-57a3403c7c46")])]})]});
            var Q76;
            Q76=makeQuery(id+"F5.boolean.opBoolean","INTERSECT",EDGE,{"disambiguationData":[OD(0.0)],"derivedFrom":[makeQuery(id+"F1.opExtrude","SWEPT_FACE",FACE,{"disambiguationData":[OSD([sQuery(id+"F0.wireOp",EDGE,"E0")])]}),makeQuery(id+"F5.opExtrude","SWEPT_FACE",FACE,{"disambiguationData":[OSD([sQuery(id+"F4.wireOp",EDGE,"57a90445-0bd0-490a-9b1f-698a67fd895c")])]})]});
            var Q77;
            Q77=makeQuery(id+"F5.boolean.opBoolean","INTERSECT",EDGE,{"disambiguationData":[OD(0.0)],"derivedFrom":[makeQuery(id+"F1.opExtrude","SWEPT_FACE",FACE,{"disambiguationData":[OSD([sQuery(id+"F0.wireOp",EDGE,"E0")])]}),makeQuery(id+"F5.opExtrude","SWEPT_FACE",FACE,{"disambiguationData":[OSD([sQuery(id+"F4.wireOp",EDGE,"0cf69e63-39ca-4a42-b99a-dd0b7aa5f2af")])]})]});
            var Q78;
            Q78=makeQuery(id+"F5.boolean.opBoolean","INTERSECT",EDGE,{"disambiguationData":[OD(0.0)],"derivedFrom":[makeQuery(id+"F1.opExtrude","SWEPT_FACE",FACE,{"disambiguationData":[OSD([sQuery(id+"F0.wireOp",EDGE,"E0")])]}),makeQuery(id+"F5.opExtrude","SWEPT_FACE",FACE,{"disambiguationData":[OSD([sQuery(id+"F4.wireOp",EDGE,"f02fcaa4-8809-4191-8bb9-9daee93d77e2")])]})]});
            var Q79;
            Q79=makeQuery(id+"F5.boolean.opBoolean","INTERSECT",EDGE,{"disambiguationData":[OD(0.0)],"derivedFrom":[makeQuery(id+"F1.opExtrude","SWEPT_FACE",FACE,{"disambiguationData":[OSD([sQuery(id+"F0.wireOp",EDGE,"E0")])]}),makeQuery(id+"F5.opExtrude","SWEPT_FACE",FACE,{"disambiguationData":[OSD([sQuery(id+"F4.wireOp",EDGE,"d264c38f-4b04-4a21-be61-ebc556e8b4dc")])]})]});
            var Q80;
            Q80=makeQuery(id+"F5.boolean.opBoolean","INTERSECT",EDGE,{"disambiguationData":[OD(0.0)],"derivedFrom":[makeQuery(id+"F1.opExtrude","SWEPT_FACE",FACE,{"disambiguationData":[OSD([sQuery(id+"F0.wireOp",EDGE,"E0")])]}),makeQuery(id+"F5.opExtrude","SWEPT_FACE",FACE,{"disambiguationData":[OSD([sQuery(id+"F4.wireOp",EDGE,"bd2a5c31-cc9d-444b-baf1-6f7b9b2beccf")])]})]});
            var Q81;
            Q81=makeQuery(id+"F5.boolean.opBoolean","INTERSECT",EDGE,{"disambiguationData":[OD(0.0)],"derivedFrom":[makeQuery(id+"F1.opExtrude","SWEPT_FACE",FACE,{"disambiguationData":[OSD([sQuery(id+"F0.wireOp",EDGE,"E0")])]}),makeQuery(id+"F5.opExtrude","SWEPT_FACE",FACE,{"disambiguationData":[OSD([sQuery(id+"F4.wireOp",EDGE,"19f739e4-1ef2-45c8-9f20-bd755fe40443")])]})]});
            var Q82;
            Q82=makeQuery(id+"F5.boolean.opBoolean","INTERSECT",EDGE,{"disambiguationData":[OD(0.0)],"derivedFrom":[makeQuery(id+"F1.opExtrude","SWEPT_FACE",FACE,{"disambiguationData":[OSD([sQuery(id+"F0.wireOp",EDGE,"E0")])]}),makeQuery(id+"F5.opExtrude","SWEPT_FACE",FACE,{"disambiguationData":[OSD([sQuery(id+"F4.wireOp",EDGE,"03b36015-34d2-4950-84e9-b550512b4ec9")])]})]});
            var Q83;
            Q83=makeQuery(id+"F5.boolean.opBoolean","INTERSECT",EDGE,{"disambiguationData":[OD(0.0)],"derivedFrom":[makeQuery(id+"F1.opExtrude","SWEPT_FACE",FACE,{"disambiguationData":[OSD([sQuery(id+"F0.wireOp",EDGE,"E0")])]}),makeQuery(id+"F5.opExtrude","SWEPT_FACE",FACE,{"disambiguationData":[OSD([sQuery(id+"F4.wireOp",EDGE,"10851094-9e06-4481-a16a-60cc523c1961")])]})]});
            var Q84;
            Q84=makeQuery(id+"F7.boolean.opBoolean","INTERSECT",EDGE,{"disambiguationData":[OD(0.0)],"derivedFrom":[makeQuery(id+"F1.opExtrude","SWEPT_FACE",FACE,{"disambiguationData":[OSD([sQuery(id+"F0.wireOp",EDGE,"E0")])]}),makeQuery(id+"F7.opExtrude","SWEPT_FACE",FACE,{"disambiguationData":[OSD([sQuery(id+"F6.wireOp",EDGE,"22307501-336a-4987-af9f-3473d2358a36")])]})]});
            var Q85;
            Q85=makeQuery(id+"F7.boolean.opBoolean","INTERSECT",EDGE,{"disambiguationData":[OD(0.0)],"derivedFrom":[makeQuery(id+"F1.opExtrude","SWEPT_FACE",FACE,{"disambiguationData":[OSD([sQuery(id+"F0.wireOp",EDGE,"E0")])]}),makeQuery(id+"F7.opExtrude","SWEPT_FACE",FACE,{"disambiguationData":[OSD([sQuery(id+"F6.wireOp",EDGE,"7a5957e4-cc16-4d21-8b24-b71f9a09db7a")])]})]});
            var Q86;
            Q86=makeQuery(id+"F7.boolean.opBoolean","INTERSECT",EDGE,{"disambiguationData":[OD(0.0)],"derivedFrom":[makeQuery(id+"F1.opExtrude","SWEPT_FACE",FACE,{"disambiguationData":[OSD([sQuery(id+"F0.wireOp",EDGE,"E0")])]}),makeQuery(id+"F7.opExtrude","SWEPT_FACE",FACE,{"disambiguationData":[OSD([sQuery(id+"F6.wireOp",EDGE,"f5a73cac-6e2b-4509-98b7-614c817debd5")])]})]});
            var Q87;
            Q87=makeQuery(id+"F7.boolean.opBoolean","INTERSECT",EDGE,{"disambiguationData":[OD(0.0)],"derivedFrom":[makeQuery(id+"F1.opExtrude","SWEPT_FACE",FACE,{"disambiguationData":[OSD([sQuery(id+"F0.wireOp",EDGE,"E0")])]}),makeQuery(id+"F7.opExtrude","SWEPT_FACE",FACE,{"disambiguationData":[OSD([sQuery(id+"F6.wireOp",EDGE,"3257f0e8-a14c-4f57-a5a9-66824f5aab70")])]})]});
            var Q88;
            Q88=makeQuery(id+"F7.boolean.opBoolean","INTERSECT",EDGE,{"disambiguationData":[OD(0.0)],"derivedFrom":[makeQuery(id+"F1.opExtrude","SWEPT_FACE",FACE,{"disambiguationData":[OSD([sQuery(id+"F0.wireOp",EDGE,"E0")])]}),makeQuery(id+"F7.opExtrude","SWEPT_FACE",FACE,{"disambiguationData":[OSD([sQuery(id+"F6.wireOp",EDGE,"ee405ad0-9952-4166-b40a-09788f6ddfb5")])]})]});
            var Q89;
            Q89=makeQuery(id+"F7.boolean.opBoolean","INTERSECT",EDGE,{"disambiguationData":[OD(0.0)],"derivedFrom":[makeQuery(id+"F1.opExtrude","SWEPT_FACE",FACE,{"disambiguationData":[OSD([sQuery(id+"F0.wireOp",EDGE,"E0")])]}),makeQuery(id+"F7.opExtrude","SWEPT_FACE",FACE,{"disambiguationData":[OSD([sQuery(id+"F6.wireOp",EDGE,"2fa87e37-a699-481d-8a24-3aeddef2e244")])]})]});
            var Q90;
            Q90=makeQuery(id+"F7.boolean.opBoolean","INTERSECT",EDGE,{"disambiguationData":[OD(0.0)],"derivedFrom":[makeQuery(id+"F1.opExtrude","SWEPT_FACE",FACE,{"disambiguationData":[OSD([sQuery(id+"F0.wireOp",EDGE,"E0")])]}),makeQuery(id+"F7.opExtrude","SWEPT_FACE",FACE,{"disambiguationData":[OSD([sQuery(id+"F6.wireOp",EDGE,"4cac9c55-7efd-43a6-b3a8-6db941ce081a")])]})]});
            var Q91;
            Q91=makeQuery(id+"F7.boolean.opBoolean","INTERSECT",EDGE,{"disambiguationData":[OD(0.0)],"derivedFrom":[makeQuery(id+"F1.opExtrude","SWEPT_FACE",FACE,{"disambiguationData":[OSD([sQuery(id+"F0.wireOp",EDGE,"E0")])]}),makeQuery(id+"F7.opExtrude","SWEPT_FACE",FACE,{"disambiguationData":[OSD([sQuery(id+"F6.wireOp",EDGE,"b7c61857-15d8-4b71-81a2-4fbbf24b3784")])]})]});
            var Q92;
            Q92=makeQuery(id+"F7.boolean.opBoolean","INTERSECT",EDGE,{"disambiguationData":[OD(0.0)],"derivedFrom":[makeQuery(id+"F1.opExtrude","SWEPT_FACE",FACE,{"disambiguationData":[OSD([sQuery(id+"F0.wireOp",EDGE,"E0")])]}),makeQuery(id+"F7.opExtrude","SWEPT_FACE",FACE,{"disambiguationData":[OSD([sQuery(id+"F6.wireOp",EDGE,"48937804-74be-4d1d-a780-8159de361928")])]})]});
            var Q93;
            Q93=makeQuery(id+"F7.boolean.opBoolean","INTERSECT",EDGE,{"disambiguationData":[OD(0.0)],"derivedFrom":[makeQuery(id+"F1.opExtrude","SWEPT_FACE",FACE,{"disambiguationData":[OSD([sQuery(id+"F0.wireOp",EDGE,"E0")])]}),makeQuery(id+"F7.opExtrude","SWEPT_FACE",FACE,{"disambiguationData":[OSD([sQuery(id+"F6.wireOp",EDGE,"f4b3b797-2859-490d-b7b5-c2bfef3c68df")])]})]});
            var Q94;
            Q94=makeQuery(id+"F7.boolean.opBoolean","INTERSECT",EDGE,{"disambiguationData":[OD(0.0)],"derivedFrom":[makeQuery(id+"F1.opExtrude","SWEPT_FACE",FACE,{"disambiguationData":[OSD([sQuery(id+"F0.wireOp",EDGE,"E0")])]}),makeQuery(id+"F7.opExtrude","SWEPT_FACE",FACE,{"disambiguationData":[OSD([sQuery(id+"F6.wireOp",EDGE,"1201f4c5-c131-4895-a1f1-c302d83bce6e")])]})]});
            var Q95;
            Q95=makeQuery(id+"F7.boolean.opBoolean","INTERSECT",EDGE,{"disambiguationData":[OD(0.0)],"derivedFrom":[makeQuery(id+"F1.opExtrude","SWEPT_FACE",FACE,{"disambiguationData":[OSD([sQuery(id+"F0.wireOp",EDGE,"E0")])]}),makeQuery(id+"F7.opExtrude","SWEPT_FACE",FACE,{"disambiguationData":[OSD([sQuery(id+"F6.wireOp",EDGE,"de09daf4-2825-49fb-a621-eb4d3bd58af1")])]})]});
            var Q96;
            Q96=makeQuery(id+"F7.boolean.opBoolean","INTERSECT",EDGE,{"disambiguationData":[OD(0.0)],"derivedFrom":[makeQuery(id+"F1.opExtrude","SWEPT_FACE",FACE,{"disambiguationData":[OSD([sQuery(id+"F0.wireOp",EDGE,"E0")])]}),makeQuery(id+"F7.opExtrude","SWEPT_FACE",FACE,{"disambiguationData":[OSD([sQuery(id+"F6.wireOp",EDGE,"2a262191-3a4f-451e-b395-dc7af2397be1")])]})]});
            var Q97;
            Q97=makeQuery(id+"F7.boolean.opBoolean","INTERSECT",EDGE,{"disambiguationData":[OD(0.0)],"derivedFrom":[makeQuery(id+"F1.opExtrude","SWEPT_FACE",FACE,{"disambiguationData":[OSD([sQuery(id+"F0.wireOp",EDGE,"E0")])]}),makeQuery(id+"F7.opExtrude","SWEPT_FACE",FACE,{"disambiguationData":[OSD([sQuery(id+"F6.wireOp",EDGE,"9832b7fa-ab71-4669-b3d5-036fdeb69183")])]})]});
            var Q98;
            Q98=makeQuery(id+"F7.boolean.opBoolean","INTERSECT",EDGE,{"disambiguationData":[OD(0.0)],"derivedFrom":[makeQuery(id+"F1.opExtrude","SWEPT_FACE",FACE,{"disambiguationData":[OSD([sQuery(id+"F0.wireOp",EDGE,"E0")])]}),makeQuery(id+"F7.opExtrude","SWEPT_FACE",FACE,{"disambiguationData":[OSD([sQuery(id+"F6.wireOp",EDGE,"5a534d87-88aa-4def-9ebb-4f3525dad718")])]})]});
            var Q99;
            Q99=makeQuery(id+"F7.boolean.opBoolean","INTERSECT",EDGE,{"disambiguationData":[OD(0.0)],"derivedFrom":[makeQuery(id+"F1.opExtrude","SWEPT_FACE",FACE,{"disambiguationData":[OSD([sQuery(id+"F0.wireOp",EDGE,"E0")])]}),makeQuery(id+"F7.opExtrude","SWEPT_FACE",FACE,{"disambiguationData":[OSD([sQuery(id+"F6.wireOp",EDGE,"af5d01d9-e0bb-42d4-a9e9-53d224fa13c4")])]})]});
            var Q100;
            Q100=makeQuery(id+"F7.boolean.opBoolean","INTERSECT",EDGE,{"disambiguationData":[OD(0.0)],"derivedFrom":[makeQuery(id+"F1.opExtrude","SWEPT_FACE",FACE,{"disambiguationData":[OSD([sQuery(id+"F0.wireOp",EDGE,"E0")])]}),makeQuery(id+"F7.opExtrude","SWEPT_FACE",FACE,{"disambiguationData":[OSD([sQuery(id+"F6.wireOp",EDGE,"63af3750-506c-4288-83c5-8929affd3ff9")])]})]});
            var Q101;
            Q101=makeQuery(id+"F7.boolean.opBoolean","INTERSECT",EDGE,{"disambiguationData":[OD(0.0)],"derivedFrom":[makeQuery(id+"F1.opExtrude","SWEPT_FACE",FACE,{"disambiguationData":[OSD([sQuery(id+"F0.wireOp",EDGE,"E0")])]}),makeQuery(id+"F7.opExtrude","SWEPT_FACE",FACE,{"disambiguationData":[OSD([sQuery(id+"F6.wireOp",EDGE,"2db1c546-a54b-418f-a515-398807a46512")])]})]});
            var Q102;
            Q102=makeQuery(id+"F10.boolean.opBoolean","INTERSECT",EDGE,{"disambiguationData":[OD(0.0)],"derivedFrom":[makeQuery(id+"F1.opExtrude","SWEPT_FACE",FACE,{"disambiguationData":[OSD([sQuery(id+"F0.wireOp",EDGE,"E0")])]}),makeQuery(id+"F10.opExtrude","SWEPT_FACE",FACE,{"disambiguationData":[OSD([sQuery(id+"F9.wireOp",EDGE,"429d95a1-3c8a-48cf-b1fd-65ae80db6ffc")])]})]});
            var Q103;
            Q103=makeQuery(id+"F10.boolean.opBoolean","INTERSECT",EDGE,{"disambiguationData":[OD(0.0)],"derivedFrom":[makeQuery(id+"F1.opExtrude","SWEPT_FACE",FACE,{"disambiguationData":[OSD([sQuery(id+"F0.wireOp",EDGE,"E0")])]}),makeQuery(id+"F10.opExtrude","SWEPT_FACE",FACE,{"disambiguationData":[OSD([sQuery(id+"F9.wireOp",EDGE,"88dc3317-14d6-4f39-a813-642e505b3db3")])]})]});
            var Q104;
            Q104=makeQuery(id+"F10.boolean.opBoolean","INTERSECT",EDGE,{"disambiguationData":[OD(0.0)],"derivedFrom":[makeQuery(id+"F1.opExtrude","SWEPT_FACE",FACE,{"disambiguationData":[OSD([sQuery(id+"F0.wireOp",EDGE,"E0")])]}),makeQuery(id+"F10.opExtrude","SWEPT_FACE",FACE,{"disambiguationData":[OSD([sQuery(id+"F9.wireOp",EDGE,"c61f0de6-50a4-4502-a890-74c6c6ac1cd3")])]})]});
            var Q105;
            Q105=makeQuery(id+"F10.boolean.opBoolean","INTERSECT",EDGE,{"disambiguationData":[OD(0.0)],"derivedFrom":[makeQuery(id+"F1.opExtrude","SWEPT_FACE",FACE,{"disambiguationData":[OSD([sQuery(id+"F0.wireOp",EDGE,"E0")])]}),makeQuery(id+"F10.opExtrude","SWEPT_FACE",FACE,{"disambiguationData":[OSD([sQuery(id+"F9.wireOp",EDGE,"479dec23-3f8f-44ee-8e45-d2b113d31b07")])]})]});
            var Q106;
            Q106=makeQuery(id+"F10.boolean.opBoolean","INTERSECT",EDGE,{"disambiguationData":[OD(0.0)],"derivedFrom":[makeQuery(id+"F1.opExtrude","SWEPT_FACE",FACE,{"disambiguationData":[OSD([sQuery(id+"F0.wireOp",EDGE,"E0")])]}),makeQuery(id+"F10.opExtrude","SWEPT_FACE",FACE,{"disambiguationData":[OSD([sQuery(id+"F9.wireOp",EDGE,"fce1ec24-8c70-45cc-92f2-20edd6db3c88")])]})]});
            var Q107;
            Q107=makeQuery(id+"F10.boolean.opBoolean","INTERSECT",EDGE,{"disambiguationData":[OD(0.0)],"derivedFrom":[makeQuery(id+"F1.opExtrude","SWEPT_FACE",FACE,{"disambiguationData":[OSD([sQuery(id+"F0.wireOp",EDGE,"E0")])]}),makeQuery(id+"F10.opExtrude","SWEPT_FACE",FACE,{"disambiguationData":[OSD([sQuery(id+"F9.wireOp",EDGE,"0975aea8-55f6-417d-8d6b-6ad5a96ef988")])]})]});
            var Q108;
            Q108=makeQuery(id+"F10.boolean.opBoolean","INTERSECT",EDGE,{"disambiguationData":[OD(0.0)],"derivedFrom":[makeQuery(id+"F1.opExtrude","SWEPT_FACE",FACE,{"disambiguationData":[OSD([sQuery(id+"F0.wireOp",EDGE,"E0")])]}),makeQuery(id+"F10.opExtrude","SWEPT_FACE",FACE,{"disambiguationData":[OSD([sQuery(id+"F9.wireOp",EDGE,"e0e213fe-66f1-429b-aeb4-bda37cd8a542")])]})]});
            var Q109;
            Q109=makeQuery(id+"F10.boolean.opBoolean","INTERSECT",EDGE,{"disambiguationData":[OD(0.0)],"derivedFrom":[makeQuery(id+"F1.opExtrude","SWEPT_FACE",FACE,{"disambiguationData":[OSD([sQuery(id+"F0.wireOp",EDGE,"E0")])]}),makeQuery(id+"F10.opExtrude","SWEPT_FACE",FACE,{"disambiguationData":[OSD([sQuery(id+"F9.wireOp",EDGE,"OpU4Ypz6-Hcb8-YkKV-7chd-lZCeiZS7tYYF")])]})]});
            var Q110;
            Q110=makeQuery(id+"F10.boolean.opBoolean","INTERSECT",EDGE,{"disambiguationData":[OD(0.0)],"derivedFrom":[makeQuery(id+"F1.opExtrude","SWEPT_FACE",FACE,{"disambiguationData":[OSD([sQuery(id+"F0.wireOp",EDGE,"E0")])]}),makeQuery(id+"F10.opExtrude","SWEPT_FACE",FACE,{"disambiguationData":[OSD([sQuery(id+"F9.wireOp",EDGE,"7meaahbg-dbg3-uSPd-PEJJ-e7DtyzYx0gQt"),sQuery(id+"F9.wireOp",EDGE,"vEAYXyeL-ay2Z-WL7a-7Ha5-VfRoazVvpcCo")])]})]});
            var Q111;
            Q111=makeQuery(id+"F10.boolean.opBoolean","INTERSECT",EDGE,{"disambiguationData":[OD(0.0)],"derivedFrom":[makeQuery(id+"F1.opExtrude","SWEPT_FACE",FACE,{"disambiguationData":[OSD([sQuery(id+"F0.wireOp",EDGE,"E0")])]}),makeQuery(id+"F10.opExtrude","SWEPT_FACE",FACE,{"disambiguationData":[OSD([sQuery(id+"F9.wireOp",EDGE,"1QEsIIjE-87yi-7XXF-o0p4-XyzEA0SBXInf")])]})]});
            var Q112;
            Q112=makeQuery(id+"F10.boolean.opBoolean","INTERSECT",EDGE,{"disambiguationData":[OD(0.0)],"derivedFrom":[makeQuery(id+"F1.opExtrude","SWEPT_FACE",FACE,{"disambiguationData":[OSD([sQuery(id+"F0.wireOp",EDGE,"E0")])]}),makeQuery(id+"F10.opExtrude","SWEPT_FACE",FACE,{"disambiguationData":[OSD([sQuery(id+"F9.wireOp",EDGE,"4fa15834-391d-4db3-8b3b-82f9d2034739")])]})]});
            var Q113;
            Q113=makeQuery(id+"F10.boolean.opBoolean","INTERSECT",EDGE,{"disambiguationData":[OD(0.0)],"derivedFrom":[makeQuery(id+"F1.opExtrude","SWEPT_FACE",FACE,{"disambiguationData":[OSD([sQuery(id+"F0.wireOp",EDGE,"E0")])]}),makeQuery(id+"F10.opExtrude","SWEPT_FACE",FACE,{"disambiguationData":[OSD([sQuery(id+"F9.wireOp",EDGE,"cf1de00f-3169-4f70-98fb-b7290205bd4b")])]})]});
            var Q114;
            Q114=makeQuery(id+"F10.boolean.opBoolean","INTERSECT",EDGE,{"disambiguationData":[OD(0.0)],"derivedFrom":[makeQuery(id+"F1.opExtrude","SWEPT_FACE",FACE,{"disambiguationData":[OSD([sQuery(id+"F0.wireOp",EDGE,"E0")])]}),makeQuery(id+"F10.opExtrude","SWEPT_FACE",FACE,{"disambiguationData":[OSD([sQuery(id+"F9.wireOp",EDGE,"e82f161c-c8f9-431a-b111-592f8292c69f")])]})]});
            var Q115;
            Q115=makeQuery(id+"F10.boolean.opBoolean","INTERSECT",EDGE,{"disambiguationData":[OD(0.0)],"derivedFrom":[makeQuery(id+"F1.opExtrude","SWEPT_FACE",FACE,{"disambiguationData":[OSD([sQuery(id+"F0.wireOp",EDGE,"E0")])]}),makeQuery(id+"F10.opExtrude","SWEPT_FACE",FACE,{"disambiguationData":[OSD([sQuery(id+"F9.wireOp",EDGE,"17f8cebd-a2bc-4d80-8a13-7e07ce9ceaf0")])]})]});
            var Q116;
            Q116=makeQuery(id+"F10.boolean.opBoolean","INTERSECT",EDGE,{"disambiguationData":[OD(0.0)],"derivedFrom":[makeQuery(id+"F1.opExtrude","SWEPT_FACE",FACE,{"disambiguationData":[OSD([sQuery(id+"F0.wireOp",EDGE,"E0")])]}),makeQuery(id+"F10.opExtrude","SWEPT_FACE",FACE,{"disambiguationData":[OSD([sQuery(id+"F9.wireOp",EDGE,"4653122c-81e7-43b8-a175-0e9b4399c1dd")])]})]});
            var Q117;
            Q117=makeQuery(id+"F10.boolean.opBoolean","INTERSECT",EDGE,{"disambiguationData":[OD(0.0)],"derivedFrom":[makeQuery(id+"F1.opExtrude","SWEPT_FACE",FACE,{"disambiguationData":[OSD([sQuery(id+"F0.wireOp",EDGE,"E0")])]}),makeQuery(id+"F10.opExtrude","SWEPT_FACE",FACE,{"disambiguationData":[OSD([sQuery(id+"F9.wireOp",EDGE,"f7332d99-994a-4820-91d6-0eb80c66d826")])]})]});
            var Q118;
            Q118=makeQuery(id+"F10.boolean.opBoolean","INTERSECT",EDGE,{"disambiguationData":[OD(0.0)],"derivedFrom":[makeQuery(id+"F1.opExtrude","SWEPT_FACE",FACE,{"disambiguationData":[OSD([sQuery(id+"F0.wireOp",EDGE,"E0")])]}),makeQuery(id+"F10.opExtrude","SWEPT_FACE",FACE,{"disambiguationData":[OSD([sQuery(id+"F9.wireOp",EDGE,"917abea8-5958-4d13-b49a-d9c63b39efb4")])]})]});
            var Q119;
            Q119=makeQuery(id+"F10.boolean.opBoolean","INTERSECT",EDGE,{"disambiguationData":[OD(0.0)],"derivedFrom":[makeQuery(id+"F1.opExtrude","SWEPT_FACE",FACE,{"disambiguationData":[OSD([sQuery(id+"F0.wireOp",EDGE,"E0")])]}),makeQuery(id+"F10.opExtrude","SWEPT_FACE",FACE,{"disambiguationData":[OSD([sQuery(id+"F9.wireOp",EDGE,"5ad42132-cac8-4035-b0a1-ce6f07b595eb")])]})]});
            var Q120;
            Q120=makeQuery(id+"F10.boolean.opBoolean","INTERSECT",EDGE,{"disambiguationData":[OD(0.0)],"derivedFrom":[makeQuery(id+"F1.opExtrude","SWEPT_FACE",FACE,{"disambiguationData":[OSD([sQuery(id+"F0.wireOp",EDGE,"E0")])]}),makeQuery(id+"F10.opExtrude","SWEPT_FACE",FACE,{"disambiguationData":[OSD([sQuery(id+"F9.wireOp",EDGE,"423f58d8-1f19-46c3-b5b6-1235c5f2b6ac")])]})]});
            var Q121;
            Q121=makeQuery(id+"F10.boolean.opBoolean","INTERSECT",EDGE,{"disambiguationData":[OD(0.0)],"derivedFrom":[makeQuery(id+"F1.opExtrude","SWEPT_FACE",FACE,{"disambiguationData":[OSD([sQuery(id+"F0.wireOp",EDGE,"E0")])]}),makeQuery(id+"F10.opExtrude","SWEPT_FACE",FACE,{"disambiguationData":[OSD([sQuery(id+"F9.wireOp",EDGE,"a8de5c63-b59d-4111-aaf0-c59ceeb84539")])]})]});
            var Q122;
            Q122=makeQuery(id+"F10.boolean.opBoolean","INTERSECT",EDGE,{"disambiguationData":[OD(0.0)],"derivedFrom":[makeQuery(id+"F1.opExtrude","SWEPT_FACE",FACE,{"disambiguationData":[OSD([sQuery(id+"F0.wireOp",EDGE,"E0")])]}),makeQuery(id+"F10.opExtrude","SWEPT_FACE",FACE,{"disambiguationData":[OSD([sQuery(id+"F9.wireOp",EDGE,"43266347-99e5-4a65-87d8-d68d1b57105e")])]})]});
            var Q123;
            Q123=makeQuery(id+"F10.boolean.opBoolean","INTERSECT",EDGE,{"disambiguationData":[OD(0.0)],"derivedFrom":[makeQuery(id+"F1.opExtrude","SWEPT_FACE",FACE,{"disambiguationData":[OSD([sQuery(id+"F0.wireOp",EDGE,"E0")])]}),makeQuery(id+"F10.opExtrude","SWEPT_FACE",FACE,{"disambiguationData":[OSD([sQuery(id+"F9.wireOp",EDGE,"2193aa8a-cfb0-48d0-87fc-1cfe83a7fd52")])]})]});
            var Q124;
            Q124=makeQuery(id+"F10.boolean.opBoolean","INTERSECT",EDGE,{"disambiguationData":[OD(0.0)],"derivedFrom":[makeQuery(id+"F1.opExtrude","SWEPT_FACE",FACE,{"disambiguationData":[OSD([sQuery(id+"F0.wireOp",EDGE,"E0")])]}),makeQuery(id+"F10.opExtrude","SWEPT_FACE",FACE,{"disambiguationData":[OSD([sQuery(id+"F9.wireOp",EDGE,"589360f9-4b1b-47cd-a11b-2a67260c207c")])]})]});
            var Q125;
            Q125=makeQuery(id+"F10.boolean.opBoolean","INTERSECT",EDGE,{"disambiguationData":[OD(0.0)],"derivedFrom":[makeQuery(id+"F1.opExtrude","SWEPT_FACE",FACE,{"disambiguationData":[OSD([sQuery(id+"F0.wireOp",EDGE,"E0")])]}),makeQuery(id+"F10.opExtrude","SWEPT_FACE",FACE,{"disambiguationData":[OSD([sQuery(id+"F9.wireOp",EDGE,"d7004727-f34f-4852-a492-ed529d9aa36c")])]})]});
            var Q126;
            Q126=makeQuery(id+"F10.boolean.opBoolean","INTERSECT",EDGE,{"disambiguationData":[OD(0.0)],"derivedFrom":[makeQuery(id+"F1.opExtrude","SWEPT_FACE",FACE,{"disambiguationData":[OSD([sQuery(id+"F0.wireOp",EDGE,"E0")])]}),makeQuery(id+"F10.opExtrude","SWEPT_FACE",FACE,{"disambiguationData":[OSD([sQuery(id+"F9.wireOp",EDGE,"b6c25ba9-2617-4775-a0b3-41ef528efab6")])]})]});
            var Q127;
            Q127=makeQuery(id+"F10.boolean.opBoolean","INTERSECT",EDGE,{"disambiguationData":[OD(0.0)],"derivedFrom":[makeQuery(id+"F1.opExtrude","SWEPT_FACE",FACE,{"disambiguationData":[OSD([sQuery(id+"F0.wireOp",EDGE,"E0")])]}),makeQuery(id+"F10.opExtrude","SWEPT_FACE",FACE,{"disambiguationData":[OSD([sQuery(id+"F9.wireOp",EDGE,"0749a5eb-1656-439a-a869-05d76e53423e")])]})]});
            var Q128;
            Q128=makeQuery(id+"F10.boolean.opBoolean","INTERSECT",EDGE,{"disambiguationData":[OD(0.0)],"derivedFrom":[makeQuery(id+"F1.opExtrude","SWEPT_FACE",FACE,{"disambiguationData":[OSD([sQuery(id+"F0.wireOp",EDGE,"E0")])]}),makeQuery(id+"F10.opExtrude","SWEPT_FACE",FACE,{"disambiguationData":[OSD([sQuery(id+"F9.wireOp",EDGE,"8357bcdf-6207-4d5b-93da-fad6725d465d")])]})]});
            var Q129;
            Q129=makeQuery(id+"F10.boolean.opBoolean","INTERSECT",EDGE,{"disambiguationData":[OD(0.0)],"derivedFrom":[makeQuery(id+"F1.opExtrude","SWEPT_FACE",FACE,{"disambiguationData":[OSD([sQuery(id+"F0.wireOp",EDGE,"E0")])]}),makeQuery(id+"F10.opExtrude","SWEPT_FACE",FACE,{"disambiguationData":[OSD([sQuery(id+"F9.wireOp",EDGE,"c678ade0-3d66-4aad-85d1-643d7c5f28b6")])]})]});
            var Q130;
            Q130=makeQuery(id+"F7.boolean.opBoolean","INTERSECT",EDGE,{"disambiguationData":[OD(0.0)],"derivedFrom":[makeQuery(id+"F1.opExtrude","SWEPT_FACE",FACE,{"disambiguationData":[OSD([sQuery(id+"F0.wireOp",EDGE,"E0")])]}),makeQuery(id+"F7.opExtrude","SWEPT_FACE",FACE,{"disambiguationData":[OSD([sQuery(id+"F6.wireOp",EDGE,"31c7d22c-81f8-4662-bd11-6a8b92b7cb61")])]})]});
            var Q131;
            Q131=makeQuery(id+"F7.boolean.opBoolean","INTERSECT",EDGE,{"disambiguationData":[OD(0.0)],"derivedFrom":[makeQuery(id+"F1.opExtrude","SWEPT_FACE",FACE,{"disambiguationData":[OSD([sQuery(id+"F0.wireOp",EDGE,"E0")])]}),makeQuery(id+"F7.opExtrude","SWEPT_FACE",FACE,{"disambiguationData":[OSD([sQuery(id+"F6.wireOp",EDGE,"9760f720-9e2d-42e7-b9e9-8ad347021829")])]})]});
            var Q132;
            Q132=makeQuery(id+"F7.boolean.opBoolean","INTERSECT",EDGE,{"disambiguationData":[OD(0.0)],"derivedFrom":[makeQuery(id+"F1.opExtrude","SWEPT_FACE",FACE,{"disambiguationData":[OSD([sQuery(id+"F0.wireOp",EDGE,"E0")])]}),makeQuery(id+"F7.opExtrude","SWEPT_FACE",FACE,{"disambiguationData":[OSD([sQuery(id+"F6.wireOp",EDGE,"f669afdf-d7ad-41c0-aa00-2f38db0ae71b")])]})]});
            var Q133;
            Q133=makeQuery(id+"F7.boolean.opBoolean","INTERSECT",EDGE,{"disambiguationData":[OD(0.0)],"derivedFrom":[makeQuery(id+"F1.opExtrude","SWEPT_FACE",FACE,{"disambiguationData":[OSD([sQuery(id+"F0.wireOp",EDGE,"E0")])]}),makeQuery(id+"F7.opExtrude","SWEPT_FACE",FACE,{"disambiguationData":[OSD([sQuery(id+"F6.wireOp",EDGE,"27ce2371-831d-4e51-9e08-e601952e9ea9")])]})]});
            var Q134;
            Q134=makeQuery(id+"F7.boolean.opBoolean","INTERSECT",EDGE,{"disambiguationData":[OD(0.0)],"derivedFrom":[makeQuery(id+"F1.opExtrude","SWEPT_FACE",FACE,{"disambiguationData":[OSD([sQuery(id+"F0.wireOp",EDGE,"E0")])]}),makeQuery(id+"F7.opExtrude","SWEPT_FACE",FACE,{"disambiguationData":[OSD([sQuery(id+"F6.wireOp",EDGE,"e27b1b56-f1a0-4449-8924-ff9f4a1ebb5a")])]})]});
            var Q135;
            Q135=makeQuery(id+"F10.boolean.opBoolean","INTERSECT",EDGE,{"disambiguationData":[OD(0.0)],"derivedFrom":[makeQuery(id+"F1.opExtrude","SWEPT_FACE",FACE,{"disambiguationData":[OSD([sQuery(id+"F0.wireOp",EDGE,"E0")])]}),makeQuery(id+"F10.opExtrude","SWEPT_FACE",FACE,{"disambiguationData":[OSD([sQuery(id+"F9.wireOp",EDGE,"bc574ee6-e8d7-4402-b7bf-a31d76de5201")])]})]});
            var Q136;
            Q136=makeQuery(id+"F10.boolean.opBoolean","INTERSECT",EDGE,{"disambiguationData":[OD(0.0)],"derivedFrom":[makeQuery(id+"F1.opExtrude","SWEPT_FACE",FACE,{"disambiguationData":[OSD([sQuery(id+"F0.wireOp",EDGE,"E0")])]}),makeQuery(id+"F10.opExtrude","SWEPT_FACE",FACE,{"disambiguationData":[OSD([sQuery(id+"F9.wireOp",EDGE,"34f3141e-2481-4cad-a724-18fe9355e9ac")])]})]});
            var Q137;
            Q137=makeQuery(id+"F10.boolean.opBoolean","INTERSECT",EDGE,{"disambiguationData":[OD(0.0)],"derivedFrom":[makeQuery(id+"F1.opExtrude","SWEPT_FACE",FACE,{"disambiguationData":[OSD([sQuery(id+"F0.wireOp",EDGE,"E0")])]}),makeQuery(id+"F10.opExtrude","SWEPT_FACE",FACE,{"disambiguationData":[OSD([sQuery(id+"F9.wireOp",EDGE,"6dc2a6c8-a69d-41e3-9ee2-05e60369f11b")])]})]});
            var Q138;
            Q138=makeQuery(id+"F10.boolean.opBoolean","INTERSECT",EDGE,{"disambiguationData":[OD(0.0)],"derivedFrom":[makeQuery(id+"F1.opExtrude","SWEPT_FACE",FACE,{"disambiguationData":[OSD([sQuery(id+"F0.wireOp",EDGE,"E0")])]}),makeQuery(id+"F10.opExtrude","SWEPT_FACE",FACE,{"disambiguationData":[OSD([sQuery(id+"F9.wireOp",EDGE,"2db869a3-9406-4888-bcbb-00bb43a69eba")])]})]});
            var Q139;
            Q139=makeQuery(id+"F10.boolean.opBoolean","INTERSECT",EDGE,{"disambiguationData":[OD(0.0)],"derivedFrom":[makeQuery(id+"F1.opExtrude","SWEPT_FACE",FACE,{"disambiguationData":[OSD([sQuery(id+"F0.wireOp",EDGE,"E0")])]}),makeQuery(id+"F10.opExtrude","SWEPT_FACE",FACE,{"disambiguationData":[OSD([sQuery(id+"F9.wireOp",EDGE,"7b437f7c-4576-4f11-8c60-76c3eb11ba37")])]})]});
            var Q140;
            Q140=makeQuery(id+"F10.boolean.opBoolean","INTERSECT",EDGE,{"disambiguationData":[OD(0.0)],"derivedFrom":[makeQuery(id+"F1.opExtrude","SWEPT_FACE",FACE,{"disambiguationData":[OSD([sQuery(id+"F0.wireOp",EDGE,"E0")])]}),makeQuery(id+"F10.opExtrude","SWEPT_FACE",FACE,{"disambiguationData":[OSD([sQuery(id+"F9.wireOp",EDGE,"7bb27c30-01e1-4c30-9b62-d81abe0e1569")])]})]});
            var Q141;
            Q141=makeQuery(id+"F7.boolean.opBoolean","INTERSECT",EDGE,{"disambiguationData":[OD(0.0)],"derivedFrom":[makeQuery(id+"F1.opExtrude","SWEPT_FACE",FACE,{"disambiguationData":[OSD([sQuery(id+"F0.wireOp",EDGE,"E0")])]}),makeQuery(id+"F7.opExtrude","SWEPT_FACE",FACE,{"disambiguationData":[OSD([sQuery(id+"F6.wireOp",EDGE,"93935017-728a-4f1c-903b-dfa4ee534358")])]})]});
            var Q142;
            Q142=makeQuery(id+"F7.boolean.opBoolean","INTERSECT",EDGE,{"disambiguationData":[OD(0.0)],"derivedFrom":[makeQuery(id+"F1.opExtrude","SWEPT_FACE",FACE,{"disambiguationData":[OSD([sQuery(id+"F0.wireOp",EDGE,"E0")])]}),makeQuery(id+"F7.opExtrude","SWEPT_FACE",FACE,{"disambiguationData":[OSD([sQuery(id+"F6.wireOp",EDGE,"1be80a28-2c43-4fd4-89f8-f32c44110b3f")])]})]});
            var Q143;
            Q143=makeQuery(id+"F7.boolean.opBoolean","INTERSECT",EDGE,{"disambiguationData":[OD(0.0)],"derivedFrom":[makeQuery(id+"F1.opExtrude","SWEPT_FACE",FACE,{"disambiguationData":[OSD([sQuery(id+"F0.wireOp",EDGE,"E0")])]}),makeQuery(id+"F7.opExtrude","SWEPT_FACE",FACE,{"disambiguationData":[OSD([sQuery(id+"F6.wireOp",EDGE,"bd02c535-79a8-436b-9978-bd3653fcbfbf")])]})]});
            var Q144;
            Q144=makeQuery(id+"F7.boolean.opBoolean","INTERSECT",EDGE,{"disambiguationData":[OD(0.0)],"derivedFrom":[makeQuery(id+"F1.opExtrude","SWEPT_FACE",FACE,{"disambiguationData":[OSD([sQuery(id+"F0.wireOp",EDGE,"E0")])]}),makeQuery(id+"F7.opExtrude","SWEPT_FACE",FACE,{"disambiguationData":[OSD([sQuery(id+"F6.wireOp",EDGE,"8923652c-60ee-40cc-b4c6-e39304594786")])]})]});
            var Q145;
            Q145=makeQuery(id+"F7.boolean.opBoolean","INTERSECT",EDGE,{"disambiguationData":[OD(0.0)],"derivedFrom":[makeQuery(id+"F1.opExtrude","SWEPT_FACE",FACE,{"disambiguationData":[OSD([sQuery(id+"F0.wireOp",EDGE,"E0")])]}),makeQuery(id+"F7.opExtrude","SWEPT_FACE",FACE,{"disambiguationData":[OSD([sQuery(id+"F6.wireOp",EDGE,"a1de85a8-8a62-40c6-b726-1736eda7a2da")])]})]});
            var Q146;
            Q146=makeQuery(id+"F7.boolean.opBoolean","INTERSECT",EDGE,{"disambiguationData":[OD(0.0)],"derivedFrom":[makeQuery(id+"F1.opExtrude","SWEPT_FACE",FACE,{"disambiguationData":[OSD([sQuery(id+"F0.wireOp",EDGE,"E0")])]}),makeQuery(id+"F7.opExtrude","SWEPT_FACE",FACE,{"disambiguationData":[OSD([sQuery(id+"F6.wireOp",EDGE,"5c94e7fe-7667-4b5c-a899-a170bc688a63")])]})]});
            var Q147;
            Q147=makeQuery(id+"F10.boolean.opBoolean","INTERSECT",EDGE,{"disambiguationData":[OD(0.0)],"derivedFrom":[makeQuery(id+"F1.opExtrude","SWEPT_FACE",FACE,{"disambiguationData":[OSD([sQuery(id+"F0.wireOp",EDGE,"E0")])]}),makeQuery(id+"F10.opExtrude","SWEPT_FACE",FACE,{"disambiguationData":[OSD([sQuery(id+"F9.wireOp",EDGE,"ad162529-5cfe-4944-83b4-e317f5486a3e")])]})]});
            var Q148;
            Q148=makeQuery(id+"F10.boolean.opBoolean","INTERSECT",EDGE,{"disambiguationData":[OD(0.0)],"derivedFrom":[makeQuery(id+"F1.opExtrude","SWEPT_FACE",FACE,{"disambiguationData":[OSD([sQuery(id+"F0.wireOp",EDGE,"E0")])]}),makeQuery(id+"F10.opExtrude","SWEPT_FACE",FACE,{"disambiguationData":[OSD([sQuery(id+"F9.wireOp",EDGE,"68b86c13-7ece-4168-b183-e17e549264ea")])]})]});
            var Q149;
            Q149=makeQuery(id+"F10.boolean.opBoolean","INTERSECT",EDGE,{"disambiguationData":[OD(0.0)],"derivedFrom":[makeQuery(id+"F1.opExtrude","SWEPT_FACE",FACE,{"disambiguationData":[OSD([sQuery(id+"F0.wireOp",EDGE,"E0")])]}),makeQuery(id+"F10.opExtrude","SWEPT_FACE",FACE,{"disambiguationData":[OSD([sQuery(id+"F9.wireOp",EDGE,"b2bf0872-2c35-4f65-a834-23150e7e820b")])]})]});
            var Q150;
            Q150=makeQuery(id+"F10.boolean.opBoolean","INTERSECT",EDGE,{"disambiguationData":[OD(0.0)],"derivedFrom":[makeQuery(id+"F1.opExtrude","SWEPT_FACE",FACE,{"disambiguationData":[OSD([sQuery(id+"F0.wireOp",EDGE,"E0")])]}),makeQuery(id+"F10.opExtrude","SWEPT_FACE",FACE,{"disambiguationData":[OSD([sQuery(id+"F9.wireOp",EDGE,"8715a638-6380-49e4-8166-a35da90eea4d")])]})]});
            var Q151;
            Q151=makeQuery(id+"F10.boolean.opBoolean","INTERSECT",EDGE,{"disambiguationData":[OD(0.0)],"derivedFrom":[makeQuery(id+"F1.opExtrude","SWEPT_FACE",FACE,{"disambiguationData":[OSD([sQuery(id+"F0.wireOp",EDGE,"E0")])]}),makeQuery(id+"F10.opExtrude","SWEPT_FACE",FACE,{"disambiguationData":[OSD([sQuery(id+"F9.wireOp",EDGE,"1193cbdb-8a08-404e-b46e-3bccfaa25342")])]})]});
            var Q152;
            Q152=makeQuery(id+"F10.boolean.opBoolean","INTERSECT",EDGE,{"disambiguationData":[OD(0.0)],"derivedFrom":[makeQuery(id+"F1.opExtrude","SWEPT_FACE",FACE,{"disambiguationData":[OSD([sQuery(id+"F0.wireOp",EDGE,"E0")])]}),makeQuery(id+"F10.opExtrude","SWEPT_FACE",FACE,{"disambiguationData":[OSD([sQuery(id+"F9.wireOp",EDGE,"9310307e-7862-42e2-8ad8-274fad6d12ca")])]})]});
            var Q153;
            Q153=makeQuery(id+"F7.boolean.opBoolean","INTERSECT",EDGE,{"disambiguationData":[OD(0.0)],"derivedFrom":[makeQuery(id+"F1.opExtrude","SWEPT_FACE",FACE,{"disambiguationData":[OSD([sQuery(id+"F0.wireOp",EDGE,"E0")])]}),makeQuery(id+"F7.opExtrude","SWEPT_FACE",FACE,{"disambiguationData":[OSD([sQuery(id+"F6.wireOp",EDGE,"a7bcfd16-c37a-45c4-b358-1ae0edba8923")])]})]});
            var Q154;
            Q154=makeQuery(id+"F7.boolean.opBoolean","INTERSECT",EDGE,{"disambiguationData":[OD(0.0)],"derivedFrom":[makeQuery(id+"F1.opExtrude","SWEPT_FACE",FACE,{"disambiguationData":[OSD([sQuery(id+"F0.wireOp",EDGE,"E0")])]}),makeQuery(id+"F7.opExtrude","SWEPT_FACE",FACE,{"disambiguationData":[OSD([sQuery(id+"F6.wireOp",EDGE,"ccd121b1-441a-4014-95ef-4c36e07d2233")])]})]});
            var Q155;
            Q155=makeQuery(id+"F7.boolean.opBoolean","INTERSECT",EDGE,{"disambiguationData":[OD(0.0)],"derivedFrom":[makeQuery(id+"F1.opExtrude","SWEPT_FACE",FACE,{"disambiguationData":[OSD([sQuery(id+"F0.wireOp",EDGE,"E0")])]}),makeQuery(id+"F7.opExtrude","SWEPT_FACE",FACE,{"disambiguationData":[OSD([sQuery(id+"F6.wireOp",EDGE,"1a29ebeb-8835-42a1-b92c-50c246a9d529")])]})]});
            var Q156;
            Q156=makeQuery(id+"F7.boolean.opBoolean","INTERSECT",EDGE,{"disambiguationData":[OD(0.0)],"derivedFrom":[makeQuery(id+"F1.opExtrude","SWEPT_FACE",FACE,{"disambiguationData":[OSD([sQuery(id+"F0.wireOp",EDGE,"E0")])]}),makeQuery(id+"F7.opExtrude","SWEPT_FACE",FACE,{"disambiguationData":[OSD([sQuery(id+"F6.wireOp",EDGE,"b31f20a5-7ea0-4ac5-bdea-8d9f319a5f5b")])]})]});
            var Q157;
            Q157=makeQuery(id+"F7.boolean.opBoolean","INTERSECT",EDGE,{"disambiguationData":[OD(0.0)],"derivedFrom":[makeQuery(id+"F1.opExtrude","SWEPT_FACE",FACE,{"disambiguationData":[OSD([sQuery(id+"F0.wireOp",EDGE,"E0")])]}),makeQuery(id+"F7.opExtrude","SWEPT_FACE",FACE,{"disambiguationData":[OSD([sQuery(id+"F6.wireOp",EDGE,"066ffb92-3af2-4bb7-b7a5-d42d1a48a872")])]})]});
            var Q158;
            Q158=makeQuery(id+"F7.boolean.opBoolean","INTERSECT",EDGE,{"disambiguationData":[OD(0.0)],"derivedFrom":[makeQuery(id+"F1.opExtrude","SWEPT_FACE",FACE,{"disambiguationData":[OSD([sQuery(id+"F0.wireOp",EDGE,"E0")])]}),makeQuery(id+"F7.opExtrude","SWEPT_FACE",FACE,{"disambiguationData":[OSD([sQuery(id+"F6.wireOp",EDGE,"ced44ab8-ddc7-4aad-977b-2de9040397a9")])]})]});
            var Q159;
            Q159=makeQuery(id+"F10.boolean.opBoolean","INTERSECT",EDGE,{"disambiguationData":[OD(0.0)],"derivedFrom":[makeQuery(id+"F1.opExtrude","SWEPT_FACE",FACE,{"disambiguationData":[OSD([sQuery(id+"F0.wireOp",EDGE,"E0")])]}),makeQuery(id+"F10.opExtrude","SWEPT_FACE",FACE,{"disambiguationData":[OSD([sQuery(id+"F9.wireOp",EDGE,"2ac3ecf1-5bac-41c2-b359-9419124c2cbe")])]})]});
            var Q160;
            Q160=makeQuery(id+"F10.boolean.opBoolean","INTERSECT",EDGE,{"disambiguationData":[OD(0.0)],"derivedFrom":[makeQuery(id+"F1.opExtrude","SWEPT_FACE",FACE,{"disambiguationData":[OSD([sQuery(id+"F0.wireOp",EDGE,"E0")])]}),makeQuery(id+"F10.opExtrude","SWEPT_FACE",FACE,{"disambiguationData":[OSD([sQuery(id+"F9.wireOp",EDGE,"bb57b571-6d28-4bdc-bb85-3a8de86b828f")])]})]});
            var Q161;
            Q161=makeQuery(id+"F10.boolean.opBoolean","INTERSECT",EDGE,{"disambiguationData":[OD(0.0)],"derivedFrom":[makeQuery(id+"F1.opExtrude","SWEPT_FACE",FACE,{"disambiguationData":[OSD([sQuery(id+"F0.wireOp",EDGE,"E0")])]}),makeQuery(id+"F10.opExtrude","SWEPT_FACE",FACE,{"disambiguationData":[OSD([sQuery(id+"F9.wireOp",EDGE,"01df38a3-00a2-4b1c-aa54-0799b5c0ab2b")])]})]});
            var Q162;
            Q162=makeQuery(id+"F10.boolean.opBoolean","INTERSECT",EDGE,{"disambiguationData":[OD(0.0)],"derivedFrom":[makeQuery(id+"F1.opExtrude","SWEPT_FACE",FACE,{"disambiguationData":[OSD([sQuery(id+"F0.wireOp",EDGE,"E0")])]}),makeQuery(id+"F10.opExtrude","SWEPT_FACE",FACE,{"disambiguationData":[OSD([sQuery(id+"F9.wireOp",EDGE,"8d6d2ff5-cd1a-4c01-981c-d6a7ec693cea")])]})]});
            var Q163;
            Q163=makeQuery(id+"F10.boolean.opBoolean","INTERSECT",EDGE,{"disambiguationData":[OD(0.0)],"derivedFrom":[makeQuery(id+"F1.opExtrude","SWEPT_FACE",FACE,{"disambiguationData":[OSD([sQuery(id+"F0.wireOp",EDGE,"E0")])]}),makeQuery(id+"F10.opExtrude","SWEPT_FACE",FACE,{"disambiguationData":[OSD([sQuery(id+"F9.wireOp",EDGE,"2a376053-e003-4ce5-91a1-66395999f384")])]})]});
            var Q164;
            Q164=makeQuery(id+"F10.boolean.opBoolean","INTERSECT",EDGE,{"disambiguationData":[OD(0.0)],"derivedFrom":[makeQuery(id+"F1.opExtrude","SWEPT_FACE",FACE,{"disambiguationData":[OSD([sQuery(id+"F0.wireOp",EDGE,"E0")])]}),makeQuery(id+"F10.opExtrude","SWEPT_FACE",FACE,{"disambiguationData":[OSD([sQuery(id+"F9.wireOp",EDGE,"3ae87d72-d5e9-4fd7-8bad-e14353bbd74b")])]})]});
            var Q165;
            Q165=makeQuery(id+"F10.boolean.opBoolean","INTERSECT",EDGE,{"disambiguationData":[OD(0.0)],"derivedFrom":[makeQuery(id+"F1.opExtrude","SWEPT_FACE",FACE,{"disambiguationData":[OSD([sQuery(id+"F0.wireOp",EDGE,"E0")])]}),makeQuery(id+"F10.opExtrude","SWEPT_FACE",FACE,{"disambiguationData":[OSD([sQuery(id+"F9.wireOp",EDGE,"8d6d2ff5-cd1a-4c01-981c-d6a7ec693cea")])]})]});
            var Q166;
            Q166=makeQuery(id+"F10.boolean.opBoolean","INTERSECT",EDGE,{"disambiguationData":[OD(0.0)],"derivedFrom":[makeQuery(id+"F1.opExtrude","SWEPT_FACE",FACE,{"disambiguationData":[OSD([sQuery(id+"F0.wireOp",EDGE,"E0")])]}),makeQuery(id+"F10.opExtrude","SWEPT_FACE",FACE,{"disambiguationData":[OSD([sQuery(id+"F9.wireOp",EDGE,"be914a45-ffb7-4e2b-a3ec-587ed71103c0")])]})]});
            var Q167;
            Q167=makeQuery(id+"F10.boolean.opBoolean","INTERSECT",EDGE,{"disambiguationData":[OD(0.0)],"derivedFrom":[makeQuery(id+"F1.opExtrude","SWEPT_FACE",FACE,{"disambiguationData":[OSD([sQuery(id+"F0.wireOp",EDGE,"E0")])]}),makeQuery(id+"F10.opExtrude","SWEPT_FACE",FACE,{"disambiguationData":[OSD([sQuery(id+"F9.wireOp",EDGE,"3ffd9d2e-510e-4de6-8091-eb6a432f9cc3")])]})]});
            var Q168;
            Q168=makeQuery(id+"F10.boolean.opBoolean","INTERSECT",EDGE,{"disambiguationData":[OD(0.0)],"derivedFrom":[makeQuery(id+"F1.opExtrude","SWEPT_FACE",FACE,{"disambiguationData":[OSD([sQuery(id+"F0.wireOp",EDGE,"E0")])]}),makeQuery(id+"F10.opExtrude","SWEPT_FACE",FACE,{"disambiguationData":[OSD([sQuery(id+"F9.wireOp",EDGE,"bd4633cb-a1a0-4c2a-b75b-ae6ce3798ed8")])]})]});
            var Q169;
            Q169=makeQuery(id+"F10.boolean.opBoolean","INTERSECT",EDGE,{"disambiguationData":[OD(0.0)],"derivedFrom":[makeQuery(id+"F1.opExtrude","SWEPT_FACE",FACE,{"disambiguationData":[OSD([sQuery(id+"F0.wireOp",EDGE,"E0")])]}),makeQuery(id+"F10.opExtrude","SWEPT_FACE",FACE,{"disambiguationData":[OSD([sQuery(id+"F9.wireOp",EDGE,"117fbaf9-7363-4f4d-8f80-632232ace110")])]})]});
            var Q170;
            Q170=makeQuery(id+"F10.boolean.opBoolean","INTERSECT",EDGE,{"disambiguationData":[OD(0.0)],"derivedFrom":[makeQuery(id+"F1.opExtrude","SWEPT_FACE",FACE,{"disambiguationData":[OSD([sQuery(id+"F0.wireOp",EDGE,"E0")])]}),makeQuery(id+"F10.opExtrude","SWEPT_FACE",FACE,{"disambiguationData":[OSD([sQuery(id+"F9.wireOp",EDGE,"a88a4bda-f792-4dab-aaff-bd76e840daaf")])]})]});
            var Q171;
            Q171=makeQuery(id+"F10.boolean.opBoolean","INTERSECT",EDGE,{"disambiguationData":[OD(0.0)],"derivedFrom":[makeQuery(id+"F1.opExtrude","SWEPT_FACE",FACE,{"disambiguationData":[OSD([sQuery(id+"F0.wireOp",EDGE,"E0")])]}),makeQuery(id+"F10.opExtrude","SWEPT_FACE",FACE,{"disambiguationData":[OSD([sQuery(id+"F9.wireOp",EDGE,"4e834629-6a74-4855-ade5-f6e74bb3a83c")])]})]});
            var Q172;
            Q172=makeQuery(id+"F7.boolean.opBoolean","INTERSECT",EDGE,{"disambiguationData":[OD(0.0)],"derivedFrom":[makeQuery(id+"F1.opExtrude","SWEPT_FACE",FACE,{"disambiguationData":[OSD([sQuery(id+"F0.wireOp",EDGE,"E0")])]}),makeQuery(id+"F7.opExtrude","SWEPT_FACE",FACE,{"disambiguationData":[OSD([sQuery(id+"F6.wireOp",EDGE,"6589fb1d-312b-4644-b9fc-294650b0a4aa")])]})]});
            var Q173;
            Q173=makeQuery(id+"F7.boolean.opBoolean","INTERSECT",EDGE,{"disambiguationData":[OD(0.0)],"derivedFrom":[makeQuery(id+"F1.opExtrude","SWEPT_FACE",FACE,{"disambiguationData":[OSD([sQuery(id+"F0.wireOp",EDGE,"E0")])]}),makeQuery(id+"F7.opExtrude","SWEPT_FACE",FACE,{"disambiguationData":[OSD([sQuery(id+"F6.wireOp",EDGE,"5f897133-5c0d-465f-b427-282926e35fab")])]})]});
            var Q174;
            Q174=makeQuery(id+"F7.boolean.opBoolean","INTERSECT",EDGE,{"disambiguationData":[OD(0.0)],"derivedFrom":[makeQuery(id+"F1.opExtrude","SWEPT_FACE",FACE,{"disambiguationData":[OSD([sQuery(id+"F0.wireOp",EDGE,"E0")])]}),makeQuery(id+"F7.opExtrude","SWEPT_FACE",FACE,{"disambiguationData":[OSD([sQuery(id+"F6.wireOp",EDGE,"7a775aec-8bcc-46c7-9e27-2acd780fd80b")])]})]});
            var Q175;
            Q175=makeQuery(id+"F7.boolean.opBoolean","INTERSECT",EDGE,{"disambiguationData":[OD(0.0)],"derivedFrom":[makeQuery(id+"F1.opExtrude","SWEPT_FACE",FACE,{"disambiguationData":[OSD([sQuery(id+"F0.wireOp",EDGE,"E0")])]}),makeQuery(id+"F7.opExtrude","SWEPT_FACE",FACE,{"disambiguationData":[OSD([sQuery(id+"F6.wireOp",EDGE,"2559da72-e7a5-4982-a9d1-a98772cbbb5a")])]})]});
            var Q176;
            Q176=makeQuery(id+"F7.boolean.opBoolean","INTERSECT",EDGE,{"disambiguationData":[OD(0.0)],"derivedFrom":[makeQuery(id+"F1.opExtrude","SWEPT_FACE",FACE,{"disambiguationData":[OSD([sQuery(id+"F0.wireOp",EDGE,"E0")])]}),makeQuery(id+"F7.opExtrude","SWEPT_FACE",FACE,{"disambiguationData":[OSD([sQuery(id+"F6.wireOp",EDGE,"42a4befa-22b1-49a7-8f1c-9fc5c3368c5a")])]})]});
            var Q177;
            Q177=makeQuery(id+"F7.boolean.opBoolean","INTERSECT",EDGE,{"disambiguationData":[OD(0.0)],"derivedFrom":[makeQuery(id+"F1.opExtrude","SWEPT_FACE",FACE,{"disambiguationData":[OSD([sQuery(id+"F0.wireOp",EDGE,"E0")])]}),makeQuery(id+"F7.opExtrude","SWEPT_FACE",FACE,{"disambiguationData":[OSD([sQuery(id+"F6.wireOp",EDGE,"3dd659d4-b549-4a72-82e9-7f461cba10e9")])]})]});
            var Q178;
            Q178=makeQuery(id+"F7.boolean.opBoolean","INTERSECT",EDGE,{"disambiguationData":[OD(0.0)],"derivedFrom":[makeQuery(id+"F1.opExtrude","SWEPT_FACE",FACE,{"disambiguationData":[OSD([sQuery(id+"F0.wireOp",EDGE,"E0")])]}),makeQuery(id+"F7.opExtrude","SWEPT_FACE",FACE,{"disambiguationData":[OSD([sQuery(id+"F6.wireOp",EDGE,"ac3f06c8-d89a-4fdc-8656-42fb609f7cb2")])]})]});
            var Q179;
            Q179=makeQuery(id+"F7.boolean.opBoolean","INTERSECT",EDGE,{"disambiguationData":[OD(0.0)],"derivedFrom":[makeQuery(id+"F1.opExtrude","SWEPT_FACE",FACE,{"disambiguationData":[OSD([sQuery(id+"F0.wireOp",EDGE,"E0")])]}),makeQuery(id+"F7.opExtrude","SWEPT_FACE",FACE,{"disambiguationData":[OSD([sQuery(id+"F6.wireOp",EDGE,"20dcadda-9b8f-4667-a020-87fb84a874f5")])]})]});
            var Q180;
            Q180=makeQuery(id+"F7.boolean.opBoolean","INTERSECT",EDGE,{"disambiguationData":[OD(0.0)],"derivedFrom":[makeQuery(id+"F1.opExtrude","SWEPT_FACE",FACE,{"disambiguationData":[OSD([sQuery(id+"F0.wireOp",EDGE,"E0")])]}),makeQuery(id+"F7.opExtrude","SWEPT_FACE",FACE,{"disambiguationData":[OSD([sQuery(id+"F6.wireOp",EDGE,"0a54e51b-04a4-4c72-8fdd-f2044cd41bb6")])]})]});
            var Q181;
            Q181=makeQuery(id+"F7.boolean.opBoolean","INTERSECT",EDGE,{"disambiguationData":[OD(0.0)],"derivedFrom":[makeQuery(id+"F1.opExtrude","SWEPT_FACE",FACE,{"disambiguationData":[OSD([sQuery(id+"F0.wireOp",EDGE,"E0")])]}),makeQuery(id+"F7.opExtrude","SWEPT_FACE",FACE,{"disambiguationData":[OSD([sQuery(id+"F6.wireOp",EDGE,"5279c50d-e3c7-40df-a6ae-2a829e30a2e4")])]})]});
            var Q182;
            Q182=makeQuery(id+"F7.boolean.opBoolean","INTERSECT",EDGE,{"disambiguationData":[OD(0.0)],"derivedFrom":[makeQuery(id+"F1.opExtrude","SWEPT_FACE",FACE,{"disambiguationData":[OSD([sQuery(id+"F0.wireOp",EDGE,"E0")])]}),makeQuery(id+"F7.opExtrude","SWEPT_FACE",FACE,{"disambiguationData":[OSD([sQuery(id+"F6.wireOp",EDGE,"c00e0242-21cc-46da-ab10-4ac23868c1ae")])]})]});
            var Q183;
            Q183=makeQuery(id+"F7.boolean.opBoolean","INTERSECT",EDGE,{"disambiguationData":[OD(0.0)],"derivedFrom":[makeQuery(id+"F1.opExtrude","SWEPT_FACE",FACE,{"disambiguationData":[OSD([sQuery(id+"F0.wireOp",EDGE,"E0")])]}),makeQuery(id+"F7.opExtrude","SWEPT_FACE",FACE,{"disambiguationData":[OSD([sQuery(id+"F6.wireOp",EDGE,"b2934774-308d-449c-932f-3a1098ac2e13")])]})]});
            var Q184;
            Q184=makeQuery(id+"F7.boolean.opBoolean","INTERSECT",EDGE,{"disambiguationData":[OD(0.0)],"derivedFrom":[makeQuery(id+"F1.opExtrude","SWEPT_FACE",FACE,{"disambiguationData":[OSD([sQuery(id+"F0.wireOp",EDGE,"E0")])]}),makeQuery(id+"F7.opExtrude","SWEPT_FACE",FACE,{"disambiguationData":[OSD([sQuery(id+"F6.wireOp",EDGE,"080e9595-97ee-4677-8bd6-bafa410fbacd")])]})]});
            var Q185;
            Q185=makeQuery(id+"F7.boolean.opBoolean","INTERSECT",EDGE,{"disambiguationData":[OD(0.0)],"derivedFrom":[makeQuery(id+"F1.opExtrude","SWEPT_FACE",FACE,{"disambiguationData":[OSD([sQuery(id+"F0.wireOp",EDGE,"E0")])]}),makeQuery(id+"F7.opExtrude","SWEPT_FACE",FACE,{"disambiguationData":[OSD([sQuery(id+"F6.wireOp",EDGE,"dadb567b-1386-430c-9f3a-5fc8d100a7a2")])]})]});
            var Q186;
            Q186=makeQuery(id+"F7.boolean.opBoolean","INTERSECT",EDGE,{"disambiguationData":[OD(0.0)],"derivedFrom":[makeQuery(id+"F1.opExtrude","SWEPT_FACE",FACE,{"disambiguationData":[OSD([sQuery(id+"F0.wireOp",EDGE,"E0")])]}),makeQuery(id+"F7.opExtrude","SWEPT_FACE",FACE,{"disambiguationData":[OSD([sQuery(id+"F6.wireOp",EDGE,"b9266994-6da7-4218-b9b6-dc69dad9fbb6")])]})]});
            var Q187;
            Q187=makeQuery(id+"F7.boolean.opBoolean","INTERSECT",EDGE,{"disambiguationData":[OD(0.0)],"derivedFrom":[makeQuery(id+"F1.opExtrude","SWEPT_FACE",FACE,{"disambiguationData":[OSD([sQuery(id+"F0.wireOp",EDGE,"E0")])]}),makeQuery(id+"F7.opExtrude","SWEPT_FACE",FACE,{"disambiguationData":[OSD([sQuery(id+"F6.wireOp",EDGE,"9dd98ae6-2e30-47a1-ba76-83a55859fa92")])]})]});
            var Q188;
            Q188=makeQuery(id+"F7.boolean.opBoolean","INTERSECT",EDGE,{"disambiguationData":[OD(0.0)],"derivedFrom":[makeQuery(id+"F1.opExtrude","SWEPT_FACE",FACE,{"disambiguationData":[OSD([sQuery(id+"F0.wireOp",EDGE,"E0")])]}),makeQuery(id+"F7.opExtrude","SWEPT_FACE",FACE,{"disambiguationData":[OSD([sQuery(id+"F6.wireOp",EDGE,"e0db4643-829f-48a9-8eff-a25beb6ab781")])]})]});
            var Q189;
            Q189=makeQuery(id+"F7.boolean.opBoolean","INTERSECT",EDGE,{"disambiguationData":[OD(0.0)],"derivedFrom":[makeQuery(id+"F1.opExtrude","SWEPT_FACE",FACE,{"disambiguationData":[OSD([sQuery(id+"F0.wireOp",EDGE,"E0")])]}),makeQuery(id+"F7.opExtrude","SWEPT_FACE",FACE,{"disambiguationData":[OSD([sQuery(id+"F6.wireOp",EDGE,"f1bd9ad3-5cd4-4e3a-b3b8-e332278da6fa")])]})]});
            var Q190;
            Q190=makeQuery(id+"F10.boolean.opBoolean","INTERSECT",EDGE,{"disambiguationData":[OD(0.0)],"derivedFrom":[makeQuery(id+"F1.opExtrude","SWEPT_FACE",FACE,{"disambiguationData":[OSD([sQuery(id+"F0.wireOp",EDGE,"E0")])]}),makeQuery(id+"F10.opExtrude","SWEPT_FACE",FACE,{"disambiguationData":[OSD([sQuery(id+"F9.wireOp",EDGE,"cb8d6cfe-6865-4672-8e74-b6eabd104ceb")])]})]});
            var Q191;
            Q191=makeQuery(id+"F10.boolean.opBoolean","INTERSECT",EDGE,{"disambiguationData":[OD(0.0)],"derivedFrom":[makeQuery(id+"F1.opExtrude","SWEPT_FACE",FACE,{"disambiguationData":[OSD([sQuery(id+"F0.wireOp",EDGE,"E0")])]}),makeQuery(id+"F10.opExtrude","SWEPT_FACE",FACE,{"disambiguationData":[OSD([sQuery(id+"F9.wireOp",EDGE,"669bf558-646c-496e-bf26-3749fa86c7e1")])]})]});
            var Q192;
            Q192=makeQuery(id+"F10.boolean.opBoolean","INTERSECT",EDGE,{"disambiguationData":[OD(0.0)],"derivedFrom":[makeQuery(id+"F1.opExtrude","SWEPT_FACE",FACE,{"disambiguationData":[OSD([sQuery(id+"F0.wireOp",EDGE,"E0")])]}),makeQuery(id+"F10.opExtrude","SWEPT_FACE",FACE,{"disambiguationData":[OSD([sQuery(id+"F9.wireOp",EDGE,"0a28de13-28e8-4f33-8bdd-1a0962719dc5")])]})]});
            var Q193;
            Q193=makeQuery(id+"F10.boolean.opBoolean","INTERSECT",EDGE,{"disambiguationData":[OD(0.0)],"derivedFrom":[makeQuery(id+"F1.opExtrude","SWEPT_FACE",FACE,{"disambiguationData":[OSD([sQuery(id+"F0.wireOp",EDGE,"E0")])]}),makeQuery(id+"F10.opExtrude","SWEPT_FACE",FACE,{"disambiguationData":[OSD([sQuery(id+"F9.wireOp",EDGE,"3b8b2b28-c0e3-4522-9afb-7c7d64f31835")])]})]});
            var Q194;
            Q194=makeQuery(id+"F10.boolean.opBoolean","INTERSECT",EDGE,{"disambiguationData":[OD(0.0)],"derivedFrom":[makeQuery(id+"F1.opExtrude","SWEPT_FACE",FACE,{"disambiguationData":[OSD([sQuery(id+"F0.wireOp",EDGE,"E0")])]}),makeQuery(id+"F10.opExtrude","SWEPT_FACE",FACE,{"disambiguationData":[OSD([sQuery(id+"F9.wireOp",EDGE,"b5321248-a158-4813-ba77-dbdb8d777a1d")])]})]});
            var Q195;
            Q195=makeQuery(id+"F10.boolean.opBoolean","INTERSECT",EDGE,{"disambiguationData":[OD(0.0)],"derivedFrom":[makeQuery(id+"F1.opExtrude","SWEPT_FACE",FACE,{"disambiguationData":[OSD([sQuery(id+"F0.wireOp",EDGE,"E0")])]}),makeQuery(id+"F10.opExtrude","SWEPT_FACE",FACE,{"disambiguationData":[OSD([sQuery(id+"F9.wireOp",EDGE,"e5c3d3fb-08e1-497d-ac67-a5b448ee73d7")])]})]});
            var Q196;
            Q196=makeQuery(id+"F7.boolean.opBoolean","INTERSECT",EDGE,{"disambiguationData":[OD(0.0)],"derivedFrom":[makeQuery(id+"F1.opExtrude","SWEPT_FACE",FACE,{"disambiguationData":[OSD([sQuery(id+"F0.wireOp",EDGE,"E0")])]}),makeQuery(id+"F7.opExtrude","SWEPT_FACE",FACE,{"disambiguationData":[OSD([sQuery(id+"F6.wireOp",EDGE,"a546d2dc-2605-408c-b24e-faa2d271309e")])]})]});
            var Q197;
            Q197=makeQuery(id+"F7.boolean.opBoolean","INTERSECT",EDGE,{"disambiguationData":[OD(0.0)],"derivedFrom":[makeQuery(id+"F1.opExtrude","SWEPT_FACE",FACE,{"disambiguationData":[OSD([sQuery(id+"F0.wireOp",EDGE,"E0")])]}),makeQuery(id+"F7.opExtrude","SWEPT_FACE",FACE,{"disambiguationData":[OSD([sQuery(id+"F6.wireOp",EDGE,"83d52e6d-92a4-4648-8b46-e9a9552c27ba")])]})]});
            var Q198;
            Q198=makeQuery(id+"F7.boolean.opBoolean","INTERSECT",EDGE,{"disambiguationData":[OD(0.0)],"derivedFrom":[makeQuery(id+"F1.opExtrude","SWEPT_FACE",FACE,{"disambiguationData":[OSD([sQuery(id+"F0.wireOp",EDGE,"E0")])]}),makeQuery(id+"F7.opExtrude","SWEPT_FACE",FACE,{"disambiguationData":[OSD([sQuery(id+"F6.wireOp",EDGE,"3a394f99-872c-4196-87e6-3b072fe8ed46")])]})]});
            var Q199;
            Q199=makeQuery(id+"F7.boolean.opBoolean","INTERSECT",EDGE,{"disambiguationData":[OD(0.0)],"derivedFrom":[makeQuery(id+"F1.opExtrude","SWEPT_FACE",FACE,{"disambiguationData":[OSD([sQuery(id+"F0.wireOp",EDGE,"E0")])]}),makeQuery(id+"F7.opExtrude","SWEPT_FACE",FACE,{"disambiguationData":[OSD([sQuery(id+"F6.wireOp",EDGE,"dacff5a3-6968-4a67-9e75-63fe3a24236e")])]})]});
            var Q200;
            Q200=makeQuery(id+"F7.boolean.opBoolean","INTERSECT",EDGE,{"disambiguationData":[OD(0.0)],"derivedFrom":[makeQuery(id+"F1.opExtrude","SWEPT_FACE",FACE,{"disambiguationData":[OSD([sQuery(id+"F0.wireOp",EDGE,"E0")])]}),makeQuery(id+"F7.opExtrude","SWEPT_FACE",FACE,{"disambiguationData":[OSD([sQuery(id+"F6.wireOp",EDGE,"4bd018d2-9826-418d-bf88-deb3f47e7d26")])]})]});
            var Q201;
            Q201=makeQuery(id+"F7.boolean.opBoolean","INTERSECT",EDGE,{"disambiguationData":[OD(0.0)],"derivedFrom":[makeQuery(id+"F1.opExtrude","SWEPT_FACE",FACE,{"disambiguationData":[OSD([sQuery(id+"F0.wireOp",EDGE,"E0")])]}),makeQuery(id+"F7.opExtrude","SWEPT_FACE",FACE,{"disambiguationData":[OSD([sQuery(id+"F6.wireOp",EDGE,"688fe3da-c086-43d2-9b33-13069743b833")])]})]});
            var Q202;
            Q202=makeQuery(id+"F10.boolean.opBoolean","INTERSECT",EDGE,{"disambiguationData":[OD(0.0)],"derivedFrom":[makeQuery(id+"F1.opExtrude","SWEPT_FACE",FACE,{"disambiguationData":[OSD([sQuery(id+"F0.wireOp",EDGE,"E0")])]}),makeQuery(id+"F10.opExtrude","SWEPT_FACE",FACE,{"disambiguationData":[OSD([sQuery(id+"F9.wireOp",EDGE,"7b52eed1-5e93-4795-8e62-8c7c827c961c")])]})]});
            var Q203;
            Q203=makeQuery(id+"F10.boolean.opBoolean","INTERSECT",EDGE,{"disambiguationData":[OD(0.0)],"derivedFrom":[makeQuery(id+"F1.opExtrude","SWEPT_FACE",FACE,{"disambiguationData":[OSD([sQuery(id+"F0.wireOp",EDGE,"E0")])]}),makeQuery(id+"F10.opExtrude","SWEPT_FACE",FACE,{"disambiguationData":[OSD([sQuery(id+"F9.wireOp",EDGE,"121e2676-15f0-40c4-bdde-db49c7b0ce91")])]})]});
            var Q204;
            Q204=makeQuery(id+"F10.boolean.opBoolean","INTERSECT",EDGE,{"disambiguationData":[OD(0.0)],"derivedFrom":[makeQuery(id+"F1.opExtrude","SWEPT_FACE",FACE,{"disambiguationData":[OSD([sQuery(id+"F0.wireOp",EDGE,"E0")])]}),makeQuery(id+"F10.opExtrude","SWEPT_FACE",FACE,{"disambiguationData":[OSD([sQuery(id+"F9.wireOp",EDGE,"6c8742e6-57ac-4896-b350-d79696f56fd6")])]})]});
            var Q205;
            Q205=makeQuery(id+"F10.boolean.opBoolean","INTERSECT",EDGE,{"disambiguationData":[OD(0.0)],"derivedFrom":[makeQuery(id+"F1.opExtrude","SWEPT_FACE",FACE,{"disambiguationData":[OSD([sQuery(id+"F0.wireOp",EDGE,"E0")])]}),makeQuery(id+"F10.opExtrude","SWEPT_FACE",FACE,{"disambiguationData":[OSD([sQuery(id+"F9.wireOp",EDGE,"abb82f81-c2b7-42e4-b461-f70187babd0f")])]})]});
            var Q206;
            Q206=makeQuery(id+"F10.boolean.opBoolean","INTERSECT",EDGE,{"disambiguationData":[OD(0.0)],"derivedFrom":[makeQuery(id+"F1.opExtrude","SWEPT_FACE",FACE,{"disambiguationData":[OSD([sQuery(id+"F0.wireOp",EDGE,"E0")])]}),makeQuery(id+"F10.opExtrude","SWEPT_FACE",FACE,{"disambiguationData":[OSD([sQuery(id+"F9.wireOp",EDGE,"60341486-7ff5-44b2-945d-25077e210a42")])]})]});
            var Q207;
            Q207=makeQuery(id+"F10.boolean.opBoolean","INTERSECT",EDGE,{"disambiguationData":[OD(0.0)],"derivedFrom":[makeQuery(id+"F1.opExtrude","SWEPT_FACE",FACE,{"disambiguationData":[OSD([sQuery(id+"F0.wireOp",EDGE,"E0")])]}),makeQuery(id+"F10.opExtrude","SWEPT_FACE",FACE,{"disambiguationData":[OSD([sQuery(id+"F9.wireOp",EDGE,"22d36337-f6bf-46cf-8a45-76c05130d686")])]})]});
            var Q208;
            Q208=makeQuery(id+"F10.boolean.opBoolean","INTERSECT",EDGE,{"disambiguationData":[OD(0.0)],"derivedFrom":[makeQuery(id+"F1.opExtrude","SWEPT_FACE",FACE,{"disambiguationData":[OSD([sQuery(id+"F0.wireOp",EDGE,"E0")])]}),makeQuery(id+"F10.opExtrude","SWEPT_FACE",FACE,{"disambiguationData":[OSD([sQuery(id+"F9.wireOp",EDGE,"5e611113-fa52-45c0-bc99-d49581cd234e")])]})]});
            var Q209;
            Q209=makeQuery(id+"F10.boolean.opBoolean","INTERSECT",EDGE,{"disambiguationData":[OD(0.0)],"derivedFrom":[makeQuery(id+"F1.opExtrude","SWEPT_FACE",FACE,{"disambiguationData":[OSD([sQuery(id+"F0.wireOp",EDGE,"E0")])]}),makeQuery(id+"F10.opExtrude","SWEPT_FACE",FACE,{"disambiguationData":[OSD([sQuery(id+"F9.wireOp",EDGE,"1215eb1f-7712-420f-9f37-3d618c989f06")])]})]});
            var Q210;
            Q210=makeQuery(id+"F10.boolean.opBoolean","INTERSECT",EDGE,{"disambiguationData":[OD(0.0)],"derivedFrom":[makeQuery(id+"F1.opExtrude","SWEPT_FACE",FACE,{"disambiguationData":[OSD([sQuery(id+"F0.wireOp",EDGE,"E0")])]}),makeQuery(id+"F10.opExtrude","SWEPT_FACE",FACE,{"disambiguationData":[OSD([sQuery(id+"F9.wireOp",EDGE,"f9cdae2c-dfee-4b7b-8cfa-af8311c95cb8")])]})]});
            var Q211;
            Q211=makeQuery(id+"F10.boolean.opBoolean","INTERSECT",EDGE,{"disambiguationData":[OD(0.0)],"derivedFrom":[makeQuery(id+"F1.opExtrude","SWEPT_FACE",FACE,{"disambiguationData":[OSD([sQuery(id+"F0.wireOp",EDGE,"E0")])]}),makeQuery(id+"F10.opExtrude","SWEPT_FACE",FACE,{"disambiguationData":[OSD([sQuery(id+"F9.wireOp",EDGE,"9c5e5121-c6ac-4869-af42-ed4733e390cc")])]})]});
            var Q212;
            Q212=makeQuery(id+"F10.boolean.opBoolean","INTERSECT",EDGE,{"disambiguationData":[OD(0.0)],"derivedFrom":[makeQuery(id+"F1.opExtrude","SWEPT_FACE",FACE,{"disambiguationData":[OSD([sQuery(id+"F0.wireOp",EDGE,"E0")])]}),makeQuery(id+"F10.opExtrude","SWEPT_FACE",FACE,{"disambiguationData":[OSD([sQuery(id+"F9.wireOp",EDGE,"1c791c94-9947-4f29-8c52-677e286b93e0")])]})]});
            var Q213;
            Q213=makeQuery(id+"F10.boolean.opBoolean","INTERSECT",EDGE,{"disambiguationData":[OD(0.0)],"derivedFrom":[makeQuery(id+"F1.opExtrude","SWEPT_FACE",FACE,{"disambiguationData":[OSD([sQuery(id+"F0.wireOp",EDGE,"E0")])]}),makeQuery(id+"F10.opExtrude","SWEPT_FACE",FACE,{"disambiguationData":[OSD([sQuery(id+"F9.wireOp",EDGE,"b11a55d2-776c-4cc8-9330-3b53156f9da6")])]})]});
            var Q214;
            Q214=makeQuery(id+"F7.boolean.opBoolean","INTERSECT",EDGE,{"disambiguationData":[OD(0.0)],"derivedFrom":[makeQuery(id+"F1.opExtrude","SWEPT_FACE",FACE,{"disambiguationData":[OSD([sQuery(id+"F0.wireOp",EDGE,"E0")])]}),makeQuery(id+"F7.opExtrude","SWEPT_FACE",FACE,{"disambiguationData":[OSD([sQuery(id+"F6.wireOp",EDGE,"81ec299c-6d5d-4c24-8a4f-7c4c23e1b546")])]})]});
            var Q215;
            Q215=makeQuery(id+"F7.boolean.opBoolean","INTERSECT",EDGE,{"disambiguationData":[OD(0.0)],"derivedFrom":[makeQuery(id+"F1.opExtrude","SWEPT_FACE",FACE,{"disambiguationData":[OSD([sQuery(id+"F0.wireOp",EDGE,"E0")])]}),makeQuery(id+"F7.opExtrude","SWEPT_FACE",FACE,{"disambiguationData":[OSD([sQuery(id+"F6.wireOp",EDGE,"82e6de43-fa50-4c70-abab-f4b9416176ad")])]})]});
            var Q216;
            Q216=makeQuery(id+"F7.boolean.opBoolean","INTERSECT",EDGE,{"disambiguationData":[OD(0.0)],"derivedFrom":[makeQuery(id+"F1.opExtrude","SWEPT_FACE",FACE,{"disambiguationData":[OSD([sQuery(id+"F0.wireOp",EDGE,"E0")])]}),makeQuery(id+"F7.opExtrude","SWEPT_FACE",FACE,{"disambiguationData":[OSD([sQuery(id+"F6.wireOp",EDGE,"7f228a5c-a083-4118-82ee-67a40d784e87")])]})]});
            var Q217;
            Q217=makeQuery(id+"F7.boolean.opBoolean","INTERSECT",EDGE,{"disambiguationData":[OD(0.0)],"derivedFrom":[makeQuery(id+"F1.opExtrude","SWEPT_FACE",FACE,{"disambiguationData":[OSD([sQuery(id+"F0.wireOp",EDGE,"E0")])]}),makeQuery(id+"F7.opExtrude","SWEPT_FACE",FACE,{"disambiguationData":[OSD([sQuery(id+"F6.wireOp",EDGE,"07bcde23-f94c-47bd-99ba-0344f469b981")])]})]});
            var Q218;
            Q218=makeQuery(id+"F7.boolean.opBoolean","INTERSECT",EDGE,{"disambiguationData":[OD(0.0)],"derivedFrom":[makeQuery(id+"F1.opExtrude","SWEPT_FACE",FACE,{"disambiguationData":[OSD([sQuery(id+"F0.wireOp",EDGE,"E0")])]}),makeQuery(id+"F7.opExtrude","SWEPT_FACE",FACE,{"disambiguationData":[OSD([sQuery(id+"F6.wireOp",EDGE,"2b333a8c-11cd-4584-9d3f-b39d69e47acf")])]})]});
            var Q219;
            Q219=makeQuery(id+"F7.boolean.opBoolean","INTERSECT",EDGE,{"disambiguationData":[OD(0.0)],"derivedFrom":[makeQuery(id+"F1.opExtrude","SWEPT_FACE",FACE,{"disambiguationData":[OSD([sQuery(id+"F0.wireOp",EDGE,"E0")])]}),makeQuery(id+"F7.opExtrude","SWEPT_FACE",FACE,{"disambiguationData":[OSD([sQuery(id+"F6.wireOp",EDGE,"f91ae07e-f7fe-47d5-8632-f1a35ba81e8f")])]})]});
            var Q220;
            Q220=makeQuery(id+"F10.boolean.opBoolean","INTERSECT",EDGE,{"disambiguationData":[OD(0.0)],"derivedFrom":[makeQuery(id+"F1.opExtrude","SWEPT_FACE",FACE,{"disambiguationData":[OSD([sQuery(id+"F0.wireOp",EDGE,"E0")])]}),makeQuery(id+"F10.opExtrude","SWEPT_FACE",FACE,{"disambiguationData":[OSD([sQuery(id+"F9.wireOp",EDGE,"6096a3ce-5044-48b5-a349-b3a0c47d5e99")])]})]});
            var Q221;
            Q221=makeQuery(id+"F10.boolean.opBoolean","INTERSECT",EDGE,{"disambiguationData":[OD(0.0)],"derivedFrom":[makeQuery(id+"F1.opExtrude","SWEPT_FACE",FACE,{"disambiguationData":[OSD([sQuery(id+"F0.wireOp",EDGE,"E0")])]}),makeQuery(id+"F10.opExtrude","SWEPT_FACE",FACE,{"disambiguationData":[OSD([sQuery(id+"F9.wireOp",EDGE,"9a94c099-41bb-40ba-894c-4f3c7a0eafbb")])]})]});
            var Q222;
            Q222=makeQuery(id+"F10.boolean.opBoolean","INTERSECT",EDGE,{"disambiguationData":[OD(0.0)],"derivedFrom":[makeQuery(id+"F1.opExtrude","SWEPT_FACE",FACE,{"disambiguationData":[OSD([sQuery(id+"F0.wireOp",EDGE,"E0")])]}),makeQuery(id+"F10.opExtrude","SWEPT_FACE",FACE,{"disambiguationData":[OSD([sQuery(id+"F9.wireOp",EDGE,"2796c508-b6ce-4770-b208-7c59b8d85fbc")])]})]});
            var Q223;
            Q223=makeQuery(id+"F10.boolean.opBoolean","INTERSECT",EDGE,{"disambiguationData":[OD(0.0)],"derivedFrom":[makeQuery(id+"F1.opExtrude","SWEPT_FACE",FACE,{"disambiguationData":[OSD([sQuery(id+"F0.wireOp",EDGE,"E0")])]}),makeQuery(id+"F10.opExtrude","SWEPT_FACE",FACE,{"disambiguationData":[OSD([sQuery(id+"F9.wireOp",EDGE,"2e52e4ba-a856-43cc-8b69-bc95ae584be1")])]})]});
            var Q224;
            Q224=makeQuery(id+"F10.boolean.opBoolean","INTERSECT",EDGE,{"disambiguationData":[OD(0.0)],"derivedFrom":[makeQuery(id+"F1.opExtrude","SWEPT_FACE",FACE,{"disambiguationData":[OSD([sQuery(id+"F0.wireOp",EDGE,"E0")])]}),makeQuery(id+"F10.opExtrude","SWEPT_FACE",FACE,{"disambiguationData":[OSD([sQuery(id+"F9.wireOp",EDGE,"d68f23c5-fa44-4f68-a5e1-914856eae846")])]})]});
            var Q225;
            Q225=makeQuery(id+"F10.boolean.opBoolean","INTERSECT",EDGE,{"disambiguationData":[OD(0.0)],"derivedFrom":[makeQuery(id+"F1.opExtrude","SWEPT_FACE",FACE,{"disambiguationData":[OSD([sQuery(id+"F0.wireOp",EDGE,"E0")])]}),makeQuery(id+"F10.opExtrude","SWEPT_FACE",FACE,{"disambiguationData":[OSD([sQuery(id+"F9.wireOp",EDGE,"3921cf77-2c7d-4081-b0dc-8dd1674662ff")])]})]});
            var Q226;
            Q226=makeQuery(id+"F7.boolean.opBoolean","INTERSECT",EDGE,{"disambiguationData":[OD(0.0)],"derivedFrom":[makeQuery(id+"F1.opExtrude","SWEPT_FACE",FACE,{"disambiguationData":[OSD([sQuery(id+"F0.wireOp",EDGE,"E0")])]}),makeQuery(id+"F7.opExtrude","SWEPT_FACE",FACE,{"disambiguationData":[OSD([sQuery(id+"F6.wireOp",EDGE,"1f1a9126-4da4-4afe-b3b0-61ea06e02878")])]})]});
            var Q227;
            Q227=makeQuery(id+"F7.boolean.opBoolean","INTERSECT",EDGE,{"disambiguationData":[OD(0.0)],"derivedFrom":[makeQuery(id+"F1.opExtrude","SWEPT_FACE",FACE,{"disambiguationData":[OSD([sQuery(id+"F0.wireOp",EDGE,"E0")])]}),makeQuery(id+"F7.opExtrude","SWEPT_FACE",FACE,{"disambiguationData":[OSD([sQuery(id+"F6.wireOp",EDGE,"fd6a0418-0a5b-4901-b5a5-5e60565ddb8d")])]})]});
            var Q228;
            Q228=makeQuery(id+"F7.boolean.opBoolean","INTERSECT",EDGE,{"disambiguationData":[OD(0.0)],"derivedFrom":[makeQuery(id+"F1.opExtrude","SWEPT_FACE",FACE,{"disambiguationData":[OSD([sQuery(id+"F0.wireOp",EDGE,"E0")])]}),makeQuery(id+"F7.opExtrude","SWEPT_FACE",FACE,{"disambiguationData":[OSD([sQuery(id+"F6.wireOp",EDGE,"88fd7354-daea-4d87-87de-3f4d9154d1db")])]})]});
            var Q229;
            Q229=makeQuery(id+"F7.boolean.opBoolean","INTERSECT",EDGE,{"disambiguationData":[OD(0.0)],"derivedFrom":[makeQuery(id+"F1.opExtrude","SWEPT_FACE",FACE,{"disambiguationData":[OSD([sQuery(id+"F0.wireOp",EDGE,"E0")])]}),makeQuery(id+"F7.opExtrude","SWEPT_FACE",FACE,{"disambiguationData":[OSD([sQuery(id+"F6.wireOp",EDGE,"e686fd54-ae98-4f09-90c8-07cd4bd11a16")])]})]});
            var Q230;
            Q230=makeQuery(id+"F7.boolean.opBoolean","INTERSECT",EDGE,{"disambiguationData":[OD(0.0)],"derivedFrom":[makeQuery(id+"F1.opExtrude","SWEPT_FACE",FACE,{"disambiguationData":[OSD([sQuery(id+"F0.wireOp",EDGE,"E0")])]}),makeQuery(id+"F7.opExtrude","SWEPT_FACE",FACE,{"disambiguationData":[OSD([sQuery(id+"F6.wireOp",EDGE,"08b58334-56ca-40a0-8f56-63621d04fc0f")])]})]});
            var Q231;
            Q231=makeQuery(id+"F7.boolean.opBoolean","INTERSECT",EDGE,{"disambiguationData":[OD(0.0)],"derivedFrom":[makeQuery(id+"F1.opExtrude","SWEPT_FACE",FACE,{"disambiguationData":[OSD([sQuery(id+"F0.wireOp",EDGE,"E0")])]}),makeQuery(id+"F7.opExtrude","SWEPT_FACE",FACE,{"disambiguationData":[OSD([sQuery(id+"F6.wireOp",EDGE,"cd7f04d2-3622-47ae-9a04-707a5ea18902")])]})]});
            var Q232;
            Q232=makeQuery(id+"F10.boolean.opBoolean","INTERSECT",EDGE,{"disambiguationData":[OD(0.0)],"derivedFrom":[makeQuery(id+"F1.opExtrude","SWEPT_FACE",FACE,{"disambiguationData":[OSD([sQuery(id+"F0.wireOp",EDGE,"E0")])]}),makeQuery(id+"F10.opExtrude","SWEPT_FACE",FACE,{"disambiguationData":[OSD([sQuery(id+"F9.wireOp",EDGE,"d83faa9b-d45e-407d-93d1-fc8e5d4eca17")])]})]});
            var Q233;
            Q233=makeQuery(id+"F10.boolean.opBoolean","INTERSECT",EDGE,{"disambiguationData":[OD(0.0)],"derivedFrom":[makeQuery(id+"F1.opExtrude","SWEPT_FACE",FACE,{"disambiguationData":[OSD([sQuery(id+"F0.wireOp",EDGE,"E0")])]}),makeQuery(id+"F10.opExtrude","SWEPT_FACE",FACE,{"disambiguationData":[OSD([sQuery(id+"F9.wireOp",EDGE,"0bb9bc1b-8636-4d55-a596-8fb459d88000")])]})]});
            var Q234;
            Q234=makeQuery(id+"F10.boolean.opBoolean","INTERSECT",EDGE,{"disambiguationData":[OD(0.0)],"derivedFrom":[makeQuery(id+"F1.opExtrude","SWEPT_FACE",FACE,{"disambiguationData":[OSD([sQuery(id+"F0.wireOp",EDGE,"E0")])]}),makeQuery(id+"F10.opExtrude","SWEPT_FACE",FACE,{"disambiguationData":[OSD([sQuery(id+"F9.wireOp",EDGE,"de8f1f6c-7dc9-478c-a1e7-a0d904edc68b")])]})]});
            var Q235;
            Q235=makeQuery(id+"F10.boolean.opBoolean","INTERSECT",EDGE,{"disambiguationData":[OD(0.0)],"derivedFrom":[makeQuery(id+"F1.opExtrude","SWEPT_FACE",FACE,{"disambiguationData":[OSD([sQuery(id+"F0.wireOp",EDGE,"E0")])]}),makeQuery(id+"F10.opExtrude","SWEPT_FACE",FACE,{"disambiguationData":[OSD([sQuery(id+"F9.wireOp",EDGE,"4b50f863-6222-4670-ab38-0f94a0e4d076")])]})]});
            var Q236;
            Q236=makeQuery(id+"F10.boolean.opBoolean","INTERSECT",EDGE,{"disambiguationData":[OD(0.0)],"derivedFrom":[makeQuery(id+"F1.opExtrude","SWEPT_FACE",FACE,{"disambiguationData":[OSD([sQuery(id+"F0.wireOp",EDGE,"E0")])]}),makeQuery(id+"F10.opExtrude","SWEPT_FACE",FACE,{"disambiguationData":[OSD([sQuery(id+"F9.wireOp",EDGE,"f2b9081a-a049-4a09-bb62-bcd79e53e865")])]})]});
            var Q237;
            Q237=makeQuery(id+"F10.boolean.opBoolean","INTERSECT",EDGE,{"disambiguationData":[OD(0.0)],"derivedFrom":[makeQuery(id+"F1.opExtrude","SWEPT_FACE",FACE,{"disambiguationData":[OSD([sQuery(id+"F0.wireOp",EDGE,"E0")])]}),makeQuery(id+"F10.opExtrude","SWEPT_FACE",FACE,{"disambiguationData":[OSD([sQuery(id+"F9.wireOp",EDGE,"6a67a89a-99b4-4420-acea-3905a5a2b65e")])]})]});
            var Q238;
            Q238=makeQuery(id+"F7.boolean.opBoolean","INTERSECT",EDGE,{"disambiguationData":[OD(0.0)],"derivedFrom":[makeQuery(id+"F1.opExtrude","SWEPT_FACE",FACE,{"disambiguationData":[OSD([sQuery(id+"F0.wireOp",EDGE,"E0")])]}),makeQuery(id+"F7.opExtrude","SWEPT_FACE",FACE,{"disambiguationData":[OSD([sQuery(id+"F6.wireOp",EDGE,"90d9cdbb-a078-4297-bb66-39e745c2c8dc")])]})]});
            var Q239;
            Q239=makeQuery(id+"F7.boolean.opBoolean","INTERSECT",EDGE,{"disambiguationData":[OD(0.0)],"derivedFrom":[makeQuery(id+"F1.opExtrude","SWEPT_FACE",FACE,{"disambiguationData":[OSD([sQuery(id+"F0.wireOp",EDGE,"E0")])]}),makeQuery(id+"F7.opExtrude","SWEPT_FACE",FACE,{"disambiguationData":[OSD([sQuery(id+"F6.wireOp",EDGE,"869f0f0d-0ab4-4e92-8b7b-8667710e2349")])]})]});
            var Q240;
            Q240=makeQuery(id+"F7.boolean.opBoolean","INTERSECT",EDGE,{"disambiguationData":[OD(0.0)],"derivedFrom":[makeQuery(id+"F1.opExtrude","SWEPT_FACE",FACE,{"disambiguationData":[OSD([sQuery(id+"F0.wireOp",EDGE,"E0")])]}),makeQuery(id+"F7.opExtrude","SWEPT_FACE",FACE,{"disambiguationData":[OSD([sQuery(id+"F6.wireOp",EDGE,"14efab8d-e5b4-4b99-a3b8-db90cb956341")])]})]});
            var Q241;
            Q241=makeQuery(id+"F7.boolean.opBoolean","INTERSECT",EDGE,{"disambiguationData":[OD(0.0)],"derivedFrom":[makeQuery(id+"F1.opExtrude","SWEPT_FACE",FACE,{"disambiguationData":[OSD([sQuery(id+"F0.wireOp",EDGE,"E0")])]}),makeQuery(id+"F7.opExtrude","SWEPT_FACE",FACE,{"disambiguationData":[OSD([sQuery(id+"F6.wireOp",EDGE,"a2e2d135-410d-43f5-bfc8-0a9909259d6e")])]})]});
            var Q242;
            Q242=makeQuery(id+"F7.boolean.opBoolean","INTERSECT",EDGE,{"disambiguationData":[OD(0.0)],"derivedFrom":[makeQuery(id+"F1.opExtrude","SWEPT_FACE",FACE,{"disambiguationData":[OSD([sQuery(id+"F0.wireOp",EDGE,"E0")])]}),makeQuery(id+"F7.opExtrude","SWEPT_FACE",FACE,{"disambiguationData":[OSD([sQuery(id+"F6.wireOp",EDGE,"6f801692-b756-4057-a928-afc3f0341116")])]})]});
            var Q243;
            Q243=makeQuery(id+"F7.boolean.opBoolean","INTERSECT",EDGE,{"disambiguationData":[OD(0.0)],"derivedFrom":[makeQuery(id+"F1.opExtrude","SWEPT_FACE",FACE,{"disambiguationData":[OSD([sQuery(id+"F0.wireOp",EDGE,"E0")])]}),makeQuery(id+"F7.opExtrude","SWEPT_FACE",FACE,{"disambiguationData":[OSD([sQuery(id+"F6.wireOp",EDGE,"305cdedf-1ec9-4fee-9b59-03e7a0ef637e")])]})]});
            var Q244;
            Q244=makeQuery(id+"F7.boolean.opBoolean","INTERSECT",EDGE,{"disambiguationData":[OD(0.0)],"derivedFrom":[makeQuery(id+"F1.opExtrude","SWEPT_FACE",FACE,{"disambiguationData":[OSD([sQuery(id+"F0.wireOp",EDGE,"E0")])]}),makeQuery(id+"F7.opExtrude","SWEPT_FACE",FACE,{"disambiguationData":[OSD([sQuery(id+"F6.wireOp",EDGE,"14efab8d-e5b4-4b99-a3b8-db90cb956341")])]})]});
            var Q245;
            Q245=makeQuery(id+"F7.boolean.opBoolean","INTERSECT",EDGE,{"disambiguationData":[OD(0.0)],"derivedFrom":[makeQuery(id+"F1.opExtrude","SWEPT_FACE",FACE,{"disambiguationData":[OSD([sQuery(id+"F0.wireOp",EDGE,"E0")])]}),makeQuery(id+"F7.opExtrude","SWEPT_FACE",FACE,{"disambiguationData":[OSD([sQuery(id+"F6.wireOp",EDGE,"65326cb1-3073-4610-b18b-feae14be5c13")])]})]});
            var Q246;
            Q246=makeQuery(id+"F7.boolean.opBoolean","INTERSECT",EDGE,{"disambiguationData":[OD(0.0)],"derivedFrom":[makeQuery(id+"F1.opExtrude","SWEPT_FACE",FACE,{"disambiguationData":[OSD([sQuery(id+"F0.wireOp",EDGE,"E0")])]}),makeQuery(id+"F7.opExtrude","SWEPT_FACE",FACE,{"disambiguationData":[OSD([sQuery(id+"F6.wireOp",EDGE,"f8088e12-c72b-4b3d-90fb-837d882fcbba")])]})]});
            var Q247;
            Q247=makeQuery(id+"F7.boolean.opBoolean","INTERSECT",EDGE,{"disambiguationData":[OD(0.0)],"derivedFrom":[makeQuery(id+"F1.opExtrude","SWEPT_FACE",FACE,{"disambiguationData":[OSD([sQuery(id+"F0.wireOp",EDGE,"E0")])]}),makeQuery(id+"F7.opExtrude","SWEPT_FACE",FACE,{"disambiguationData":[OSD([sQuery(id+"F6.wireOp",EDGE,"3024085b-1277-45ff-89f3-f8cc26ec2f35")])]})]});
            var Q248;
            Q248=makeQuery(id+"F7.boolean.opBoolean","INTERSECT",EDGE,{"disambiguationData":[OD(0.0)],"derivedFrom":[makeQuery(id+"F1.opExtrude","SWEPT_FACE",FACE,{"disambiguationData":[OSD([sQuery(id+"F0.wireOp",EDGE,"E0")])]}),makeQuery(id+"F7.opExtrude","SWEPT_FACE",FACE,{"disambiguationData":[OSD([sQuery(id+"F6.wireOp",EDGE,"00d8fb87-0f4c-424d-839c-7e7ec4f3fd4c")])]})]});
            var Q249;
            Q249=makeQuery(id+"F7.boolean.opBoolean","INTERSECT",EDGE,{"disambiguationData":[OD(0.0)],"derivedFrom":[makeQuery(id+"F1.opExtrude","SWEPT_FACE",FACE,{"disambiguationData":[OSD([sQuery(id+"F0.wireOp",EDGE,"E0")])]}),makeQuery(id+"F7.opExtrude","SWEPT_FACE",FACE,{"disambiguationData":[OSD([sQuery(id+"F6.wireOp",EDGE,"75183ba1-81fe-4bd2-98a4-39212aa8f21d")])]})]});
            var Q250;
            Q250=makeQuery(id+"F7.boolean.opBoolean","INTERSECT",EDGE,{"disambiguationData":[OD(0.0)],"derivedFrom":[makeQuery(id+"F1.opExtrude","SWEPT_FACE",FACE,{"disambiguationData":[OSD([sQuery(id+"F0.wireOp",EDGE,"E0")])]}),makeQuery(id+"F7.opExtrude","SWEPT_FACE",FACE,{"disambiguationData":[OSD([sQuery(id+"F6.wireOp",EDGE,"a0acb2da-2927-4627-867c-5d33e32ae2f5")])]})]});
            var Q251;
            Q251=makeQuery(id+"F10.boolean.opBoolean","INTERSECT",EDGE,{"disambiguationData":[OD(0.0)],"derivedFrom":[makeQuery(id+"F1.opExtrude","SWEPT_FACE",FACE,{"disambiguationData":[OSD([sQuery(id+"F0.wireOp",EDGE,"E0")])]}),makeQuery(id+"F10.opExtrude","SWEPT_FACE",FACE,{"disambiguationData":[OSD([sQuery(id+"F9.wireOp",EDGE,"043d117d-676f-48b6-932c-ed189ea02d01")])]})]});
            var Q252;
            Q252=makeQuery(id+"F10.boolean.opBoolean","INTERSECT",EDGE,{"disambiguationData":[OD(0.0)],"derivedFrom":[makeQuery(id+"F1.opExtrude","SWEPT_FACE",FACE,{"disambiguationData":[OSD([sQuery(id+"F0.wireOp",EDGE,"E0")])]}),makeQuery(id+"F10.opExtrude","SWEPT_FACE",FACE,{"disambiguationData":[OSD([sQuery(id+"F9.wireOp",EDGE,"I1SNvpHa-ovKs-9DXm-2cYc-TDOwp1cF8JiJ")])]})]});
            var Q253;
            Q253=makeQuery(id+"F10.boolean.opBoolean","INTERSECT",EDGE,{"disambiguationData":[OD(0.0)],"derivedFrom":[makeQuery(id+"F1.opExtrude","SWEPT_FACE",FACE,{"disambiguationData":[OSD([sQuery(id+"F0.wireOp",EDGE,"E0")])]}),makeQuery(id+"F10.opExtrude","SWEPT_FACE",FACE,{"disambiguationData":[OSD([sQuery(id+"F9.wireOp",EDGE,"ThbpAlgf-J1ZK-8EEi-tm60-MKaAh34L7w5e"),sQuery(id+"F9.wireOp",EDGE,"h7cyK7oW-8o4M-WHfY-pIGo-xKwypN2QV7Za")])]})]});
            var Q254;
            Q254=makeQuery(id+"F10.boolean.opBoolean","INTERSECT",EDGE,{"disambiguationData":[OD(0.0)],"derivedFrom":[makeQuery(id+"F1.opExtrude","SWEPT_FACE",FACE,{"disambiguationData":[OSD([sQuery(id+"F0.wireOp",EDGE,"E0")])]}),makeQuery(id+"F10.opExtrude","SWEPT_FACE",FACE,{"disambiguationData":[OSD([sQuery(id+"F9.wireOp",EDGE,"YlMJEoje-hVPp-NrIK-c2S6-AKWunBmpYVRp")])]})]});
            var Q255;
            Q255=makeQuery(id+"F12.boolean.opBoolean","INTERSECT",EDGE,{"derivedFrom":[makeQuery(id+"F1.opExtrude","SWEPT_FACE",FACE,{"disambiguationData":[OSD([sQuery(id+"F0.wireOp",EDGE,"E0")])]}),makeQuery(id+"F12.opExtrude","SWEPT_FACE",FACE,{"disambiguationData":[OSD([sQuery(id+"F11.wireOp",EDGE,"ea7ba490-2a23-4636-bf66-31f082130ce2"),sQuery(id+"F11.wireOp",EDGE,"7865739c-c3e9-4b94-9baf-c32e4e0c586f")])]})]});
            var Q256;
            Q256=makeQuery(id+"F12.boolean.opBoolean","INTERSECT",EDGE,{"derivedFrom":[makeQuery(id+"F1.opExtrude","SWEPT_FACE",FACE,{"disambiguationData":[OSD([sQuery(id+"F0.wireOp",EDGE,"E0")])]}),makeQuery(id+"F12.opExtrude","SWEPT_FACE",FACE,{"disambiguationData":[OSD([sQuery(id+"F11.wireOp",EDGE,"34c2dada-d6a9-419e-92ec-ab1ef5f216ab")])]})]});
            var Q257;
            Q257=makeQuery(id+"F12.boolean.opBoolean","INTERSECT",EDGE,{"derivedFrom":[makeQuery(id+"F1.opExtrude","SWEPT_FACE",FACE,{"disambiguationData":[OSD([sQuery(id+"F0.wireOp",EDGE,"E0")])]}),makeQuery(id+"F12.opExtrude","SWEPT_FACE",FACE,{"disambiguationData":[OSD([sQuery(id+"F11.wireOp",EDGE,"db216c74-79ea-496e-b24d-2c971d5c719f")])]})]});
            var Q258;
            Q258=makeQuery(id+"F12.boolean.opBoolean","INTERSECT",EDGE,{"derivedFrom":[makeQuery(id+"F1.opExtrude","SWEPT_FACE",FACE,{"disambiguationData":[OSD([sQuery(id+"F0.wireOp",EDGE,"E0")])]}),makeQuery(id+"F12.opExtrude","SWEPT_FACE",FACE,{"disambiguationData":[OSD([sQuery(id+"F11.wireOp",EDGE,"2cbe05a2-fc25-4f97-b96c-8479a1089892")])]})]});
            var Q259;
            Q259=makeQuery(id+"F5.boolean.opBoolean","INTERSECT",EDGE,{"disambiguationData":[OD(1.0)],"derivedFrom":[makeQuery(id+"F1.opExtrude","SWEPT_FACE",FACE,{"disambiguationData":[OSD([sQuery(id+"F0.wireOp",EDGE,"E0")])]}),makeQuery(id+"F5.opExtrude","SWEPT_FACE",FACE,{"disambiguationData":[OSD([sQuery(id+"F4.wireOp",EDGE,"57a90445-0bd0-490a-9b1f-698a67fd895c")])]})]});
            var Q260;
            Q260=makeQuery(id+"F5.boolean.opBoolean","INTERSECT",EDGE,{"disambiguationData":[OD(1.0)],"derivedFrom":[makeQuery(id+"F1.opExtrude","SWEPT_FACE",FACE,{"disambiguationData":[OSD([sQuery(id+"F0.wireOp",EDGE,"E0")])]}),makeQuery(id+"F5.opExtrude","SWEPT_FACE",FACE,{"disambiguationData":[OSD([sQuery(id+"F4.wireOp",EDGE,"0cf69e63-39ca-4a42-b99a-dd0b7aa5f2af")])]})]});
            var Q261;
            Q261=makeQuery(id+"F5.boolean.opBoolean","INTERSECT",EDGE,{"disambiguationData":[OD(1.0)],"derivedFrom":[makeQuery(id+"F1.opExtrude","SWEPT_FACE",FACE,{"disambiguationData":[OSD([sQuery(id+"F0.wireOp",EDGE,"E0")])]}),makeQuery(id+"F5.opExtrude","SWEPT_FACE",FACE,{"disambiguationData":[OSD([sQuery(id+"F4.wireOp",EDGE,"f230033e-8e97-4c48-a61c-878d7d3044cc")])]})]});
            var Q262;
            Q262=makeQuery(id+"F5.boolean.opBoolean","INTERSECT",EDGE,{"disambiguationData":[OD(1.0)],"derivedFrom":[makeQuery(id+"F1.opExtrude","SWEPT_FACE",FACE,{"disambiguationData":[OSD([sQuery(id+"F0.wireOp",EDGE,"E0")])]}),makeQuery(id+"F5.opExtrude","SWEPT_FACE",FACE,{"disambiguationData":[OSD([sQuery(id+"F4.wireOp",EDGE,"4144a65f-7927-494c-8b6f-a1137679e0c2")])]})]});
            var Q263;
            Q263=makeQuery(id+"F5.boolean.opBoolean","INTERSECT",EDGE,{"disambiguationData":[OD(1.0)],"derivedFrom":[makeQuery(id+"F1.opExtrude","SWEPT_FACE",FACE,{"disambiguationData":[OSD([sQuery(id+"F0.wireOp",EDGE,"E0")])]}),makeQuery(id+"F5.opExtrude","SWEPT_FACE",FACE,{"disambiguationData":[OSD([sQuery(id+"F4.wireOp",EDGE,"12fd482c-4469-40d2-a6f5-f27bb2f23065")])]})]});
            var Q264;
            Q264=makeQuery(id+"F5.boolean.opBoolean","INTERSECT",EDGE,{"disambiguationData":[OD(1.0)],"derivedFrom":[makeQuery(id+"F1.opExtrude","SWEPT_FACE",FACE,{"disambiguationData":[OSD([sQuery(id+"F0.wireOp",EDGE,"E0")])]}),makeQuery(id+"F5.opExtrude","SWEPT_FACE",FACE,{"disambiguationData":[OSD([sQuery(id+"F4.wireOp",EDGE,"068a08e4-cb17-442e-8f38-57a3403c7c46")])]})]});
            var Q265;
            Q265=makeQuery(id+"F12.boolean.opBoolean","INTERSECT",EDGE,{"derivedFrom":[makeQuery(id+"F1.opExtrude","SWEPT_FACE",FACE,{"disambiguationData":[OSD([sQuery(id+"F0.wireOp",EDGE,"E0")])]}),makeQuery(id+"F12.opExtrude","SWEPT_FACE",FACE,{"disambiguationData":[OSD([sQuery(id+"F11.wireOp",EDGE,"67c183d3-1d7e-42da-bf2e-3ae0fa41da7f")])]})]});
            var Q266;
            Q266=makeQuery(id+"F12.boolean.opBoolean","INTERSECT",EDGE,{"derivedFrom":[makeQuery(id+"F1.opExtrude","SWEPT_FACE",FACE,{"disambiguationData":[OSD([sQuery(id+"F0.wireOp",EDGE,"E0")])]}),makeQuery(id+"F12.opExtrude","SWEPT_FACE",FACE,{"disambiguationData":[OSD([sQuery(id+"F11.wireOp",EDGE,"b03eed20-ebc4-4b92-b3f9-1f2c04b3648d")])]})]});
            var Q267;
            Q267=makeQuery(id+"F12.boolean.opBoolean","INTERSECT",EDGE,{"derivedFrom":[makeQuery(id+"F1.opExtrude","SWEPT_FACE",FACE,{"disambiguationData":[OSD([sQuery(id+"F0.wireOp",EDGE,"E0")])]}),makeQuery(id+"F12.opExtrude","SWEPT_FACE",FACE,{"disambiguationData":[OSD([sQuery(id+"F11.wireOp",EDGE,"8758c10c-265c-4590-a45d-ef684658fe9d")])]})]});
            var Q268;
            Q268=makeQuery(id+"F12.boolean.opBoolean","INTERSECT",EDGE,{"derivedFrom":[makeQuery(id+"F1.opExtrude","SWEPT_FACE",FACE,{"disambiguationData":[OSD([sQuery(id+"F0.wireOp",EDGE,"E0")])]}),makeQuery(id+"F12.opExtrude","SWEPT_FACE",FACE,{"disambiguationData":[OSD([sQuery(id+"F11.wireOp",EDGE,"f5ab9e36-810e-4fb2-ab21-dc782ddc3775")])]})]});
            var Q269;
            Q269=makeQuery(id+"F12.boolean.opBoolean","INTERSECT",EDGE,{"derivedFrom":[makeQuery(id+"F1.opExtrude","SWEPT_FACE",FACE,{"disambiguationData":[OSD([sQuery(id+"F0.wireOp",EDGE,"E0")])]}),makeQuery(id+"F12.opExtrude","SWEPT_FACE",FACE,{"disambiguationData":[OSD([sQuery(id+"F11.wireOp",EDGE,"3bce39cf-3fba-4d9c-932c-c4ba27150efd")])]})]});
            var Q270;
            Q270=makeQuery(id+"F12.boolean.opBoolean","INTERSECT",EDGE,{"derivedFrom":[makeQuery(id+"F1.opExtrude","SWEPT_FACE",FACE,{"disambiguationData":[OSD([sQuery(id+"F0.wireOp",EDGE,"E0")])]}),makeQuery(id+"F12.opExtrude","SWEPT_FACE",FACE,{"disambiguationData":[OSD([sQuery(id+"F11.wireOp",EDGE,"cf1fa2b7-3847-4b1a-8fbb-cf5b8043f2ce")])]})]});
            var Q271;
            Q271=makeQuery(id+"F12.boolean.opBoolean","INTERSECT",EDGE,{"derivedFrom":[makeQuery(id+"F1.opExtrude","SWEPT_FACE",FACE,{"disambiguationData":[OSD([sQuery(id+"F0.wireOp",EDGE,"E0")])]}),makeQuery(id+"F12.opExtrude","SWEPT_FACE",FACE,{"disambiguationData":[OSD([sQuery(id+"F11.wireOp",EDGE,"8758c10c-265c-4590-a45d-ef684658fe9d")])]})]});
            var Q272;
            Q272=makeQuery(id+"F12.boolean.opBoolean","INTERSECT",EDGE,{"derivedFrom":[makeQuery(id+"F1.opExtrude","SWEPT_FACE",FACE,{"disambiguationData":[OSD([sQuery(id+"F0.wireOp",EDGE,"E0")])]}),makeQuery(id+"F12.opExtrude","SWEPT_FACE",FACE,{"disambiguationData":[OSD([sQuery(id+"F11.wireOp",EDGE,"fa630e0c-4c21-4da5-be15-fd4a47fe4884")])]})]});
            var Q273;
            Q273=makeQuery(id+"F12.boolean.opBoolean","INTERSECT",EDGE,{"derivedFrom":[makeQuery(id+"F1.opExtrude","SWEPT_FACE",FACE,{"disambiguationData":[OSD([sQuery(id+"F0.wireOp",EDGE,"E0")])]}),makeQuery(id+"F12.opExtrude","SWEPT_FACE",FACE,{"disambiguationData":[OSD([sQuery(id+"F11.wireOp",EDGE,"b6a6a7a6-ca24-45d9-8187-9d395d61f82d")])]})]});
            var Q274;
            Q274=makeQuery(id+"F12.boolean.opBoolean","INTERSECT",EDGE,{"derivedFrom":[makeQuery(id+"F1.opExtrude","SWEPT_FACE",FACE,{"disambiguationData":[OSD([sQuery(id+"F0.wireOp",EDGE,"E0")])]}),makeQuery(id+"F12.opExtrude","SWEPT_FACE",FACE,{"disambiguationData":[OSD([sQuery(id+"F11.wireOp",EDGE,"e8bf7530-191c-453a-80a5-56862e84f5e5")])]})]});
            var Q275;
            Q275=makeQuery(id+"F12.boolean.opBoolean","INTERSECT",EDGE,{"derivedFrom":[makeQuery(id+"F1.opExtrude","SWEPT_FACE",FACE,{"disambiguationData":[OSD([sQuery(id+"F0.wireOp",EDGE,"E0")])]}),makeQuery(id+"F12.opExtrude","SWEPT_FACE",FACE,{"disambiguationData":[OSD([sQuery(id+"F11.wireOp",EDGE,"b703aa34-a04e-4aae-bb17-b9baaf51e667")])]})]});
            var Q276;
            Q276=makeQuery(id+"F12.boolean.opBoolean","INTERSECT",EDGE,{"derivedFrom":[makeQuery(id+"F1.opExtrude","SWEPT_FACE",FACE,{"disambiguationData":[OSD([sQuery(id+"F0.wireOp",EDGE,"E0")])]}),makeQuery(id+"F12.opExtrude","SWEPT_FACE",FACE,{"disambiguationData":[OSD([sQuery(id+"F11.wireOp",EDGE,"dfae5c97-7dd7-4fff-be0f-4a5376e00253")])]})]});
            var Q277;
            Q277=makeQuery(id+"F12.boolean.opBoolean","INTERSECT",EDGE,{"derivedFrom":[makeQuery(id+"F1.opExtrude","SWEPT_FACE",FACE,{"disambiguationData":[OSD([sQuery(id+"F0.wireOp",EDGE,"E0")])]}),makeQuery(id+"F12.opExtrude","SWEPT_FACE",FACE,{"disambiguationData":[OSD([sQuery(id+"F11.wireOp",EDGE,"adbe43ba-a4ba-4f23-8ac4-e92d10ea3226")])]})]});
            var Q278;
            Q278=makeQuery(id+"F12.boolean.opBoolean","INTERSECT",EDGE,{"derivedFrom":[makeQuery(id+"F1.opExtrude","SWEPT_FACE",FACE,{"disambiguationData":[OSD([sQuery(id+"F0.wireOp",EDGE,"E0")])]}),makeQuery(id+"F12.opExtrude","SWEPT_FACE",FACE,{"disambiguationData":[OSD([sQuery(id+"F11.wireOp",EDGE,"9feed077-ff96-4066-aaeb-50173201c3fb")])]})]});
            var Q279;
            Q279=makeQuery(id+"F12.boolean.opBoolean","INTERSECT",EDGE,{"derivedFrom":[makeQuery(id+"F1.opExtrude","SWEPT_FACE",FACE,{"disambiguationData":[OSD([sQuery(id+"F0.wireOp",EDGE,"E0")])]}),makeQuery(id+"F12.opExtrude","SWEPT_FACE",FACE,{"disambiguationData":[OSD([sQuery(id+"F11.wireOp",EDGE,"7fb09006-04e6-4153-a925-a5b02efa07b1")])]})]});
            var Q280;
            Q280=makeQuery(id+"F12.boolean.opBoolean","INTERSECT",EDGE,{"derivedFrom":[makeQuery(id+"F1.opExtrude","SWEPT_FACE",FACE,{"disambiguationData":[OSD([sQuery(id+"F0.wireOp",EDGE,"E0")])]}),makeQuery(id+"F12.opExtrude","SWEPT_FACE",FACE,{"disambiguationData":[OSD([sQuery(id+"F11.wireOp",EDGE,"0eb8d5e7-ee9a-4d98-a7d9-7c3a4b78cebe")])]})]});
            var Q281;
            Q281=makeQuery(id+"F12.boolean.opBoolean","INTERSECT",EDGE,{"derivedFrom":[makeQuery(id+"F1.opExtrude","SWEPT_FACE",FACE,{"disambiguationData":[OSD([sQuery(id+"F0.wireOp",EDGE,"E0")])]}),makeQuery(id+"F12.opExtrude","SWEPT_FACE",FACE,{"disambiguationData":[OSD([sQuery(id+"F11.wireOp",EDGE,"7b78b5aa-67af-4fde-b4af-6a032dea360b")])]})]});
            var Q282;
            Q282=makeQuery(id+"F12.boolean.opBoolean","INTERSECT",EDGE,{"derivedFrom":[makeQuery(id+"F1.opExtrude","SWEPT_FACE",FACE,{"disambiguationData":[OSD([sQuery(id+"F0.wireOp",EDGE,"E0")])]}),makeQuery(id+"F12.opExtrude","SWEPT_FACE",FACE,{"disambiguationData":[OSD([sQuery(id+"F11.wireOp",EDGE,"7c64193d-17ad-41bb-b9d3-a3518e0933f7")])]})]});
            var Q283;
            Q283=makeQuery(id+"F12.boolean.opBoolean","INTERSECT",EDGE,{"derivedFrom":[makeQuery(id+"F1.opExtrude","SWEPT_FACE",FACE,{"disambiguationData":[OSD([sQuery(id+"F0.wireOp",EDGE,"E0")])]}),makeQuery(id+"F12.opExtrude","SWEPT_FACE",FACE,{"disambiguationData":[OSD([sQuery(id+"F11.wireOp",EDGE,"91067103-e956-4587-aab7-dd29d1236ccd")])]})]});
            var Q284;
            Q284=makeQuery(id+"F12.boolean.opBoolean","INTERSECT",EDGE,{"derivedFrom":[makeQuery(id+"F1.opExtrude","SWEPT_FACE",FACE,{"disambiguationData":[OSD([sQuery(id+"F0.wireOp",EDGE,"E0")])]}),makeQuery(id+"F12.opExtrude","SWEPT_FACE",FACE,{"disambiguationData":[OSD([sQuery(id+"F11.wireOp",EDGE,"fc0b8eb2-9f5c-4d82-8077-afb5bb214ae3")])]})]});
            var Q285;
            Q285=makeQuery(id+"F12.boolean.opBoolean","INTERSECT",EDGE,{"derivedFrom":[makeQuery(id+"F1.opExtrude","SWEPT_FACE",FACE,{"disambiguationData":[OSD([sQuery(id+"F0.wireOp",EDGE,"E0")])]}),makeQuery(id+"F12.opExtrude","SWEPT_FACE",FACE,{"disambiguationData":[OSD([sQuery(id+"F11.wireOp",EDGE,"e95ff990-42a6-4aed-a23e-eecf14f33a02")])]})]});
            var Q286;
            Q286=makeQuery(id+"F12.boolean.opBoolean","INTERSECT",EDGE,{"derivedFrom":[makeQuery(id+"F1.opExtrude","SWEPT_FACE",FACE,{"disambiguationData":[OSD([sQuery(id+"F0.wireOp",EDGE,"E0")])]}),makeQuery(id+"F12.opExtrude","SWEPT_FACE",FACE,{"disambiguationData":[OSD([sQuery(id+"F11.wireOp",EDGE,"3114f84d-6bbb-4589-be9f-9912665327ea")])]})]});
            var Q287;
            Q287=makeQuery(id+"F12.boolean.opBoolean","INTERSECT",EDGE,{"derivedFrom":[makeQuery(id+"F1.opExtrude","SWEPT_FACE",FACE,{"disambiguationData":[OSD([sQuery(id+"F0.wireOp",EDGE,"E0")])]}),makeQuery(id+"F12.opExtrude","SWEPT_FACE",FACE,{"disambiguationData":[OSD([sQuery(id+"F11.wireOp",EDGE,"f2340e13-a843-4688-b504-44fa6c1fe9ea")])]})]});
            var Q288;
            Q288=makeQuery(id+"F12.boolean.opBoolean","INTERSECT",EDGE,{"derivedFrom":[makeQuery(id+"F1.opExtrude","SWEPT_FACE",FACE,{"disambiguationData":[OSD([sQuery(id+"F0.wireOp",EDGE,"E0")])]}),makeQuery(id+"F12.opExtrude","SWEPT_FACE",FACE,{"disambiguationData":[OSD([sQuery(id+"F11.wireOp",EDGE,"d5fa8afd-5d24-4741-81ec-8e0d84c4d4eb")])]})]});
            var Q289;
            Q289=makeQuery(id+"F12.boolean.opBoolean","INTERSECT",EDGE,{"derivedFrom":[makeQuery(id+"F1.opExtrude","SWEPT_FACE",FACE,{"disambiguationData":[OSD([sQuery(id+"F0.wireOp",EDGE,"E0")])]}),makeQuery(id+"F12.opExtrude","SWEPT_FACE",FACE,{"disambiguationData":[OSD([sQuery(id+"F11.wireOp",EDGE,"327d9c5f-6637-4679-a359-34eeb01f4f77")])]})]});
            var Q290;
            Q290=makeQuery(id+"F12.boolean.opBoolean","INTERSECT",EDGE,{"derivedFrom":[makeQuery(id+"F1.opExtrude","SWEPT_FACE",FACE,{"disambiguationData":[OSD([sQuery(id+"F0.wireOp",EDGE,"E0")])]}),makeQuery(id+"F12.opExtrude","SWEPT_FACE",FACE,{"disambiguationData":[OSD([sQuery(id+"F11.wireOp",EDGE,"6b576242-fc7a-4995-9b13-030333e3f8fe")])]})]});
            var Q291;
            Q291=makeQuery(id+"F12.boolean.opBoolean","INTERSECT",EDGE,{"derivedFrom":[makeQuery(id+"F1.opExtrude","SWEPT_FACE",FACE,{"disambiguationData":[OSD([sQuery(id+"F0.wireOp",EDGE,"E0")])]}),makeQuery(id+"F12.opExtrude","SWEPT_FACE",FACE,{"disambiguationData":[OSD([sQuery(id+"F11.wireOp",EDGE,"17310e35-f0b1-47c9-b996-b18cdb21126f")])]})]});
            var Q292;
            Q292=makeQuery(id+"F12.boolean.opBoolean","INTERSECT",EDGE,{"derivedFrom":[makeQuery(id+"F1.opExtrude","SWEPT_FACE",FACE,{"disambiguationData":[OSD([sQuery(id+"F0.wireOp",EDGE,"E0")])]}),makeQuery(id+"F12.opExtrude","SWEPT_FACE",FACE,{"disambiguationData":[OSD([sQuery(id+"F11.wireOp",EDGE,"1bea7e44-a00f-4ef5-bca6-2bec41b80301")])]})]});
            var Q293;
            Q293=makeQuery(id+"F12.boolean.opBoolean","INTERSECT",EDGE,{"derivedFrom":[makeQuery(id+"F1.opExtrude","SWEPT_FACE",FACE,{"disambiguationData":[OSD([sQuery(id+"F0.wireOp",EDGE,"E0")])]}),makeQuery(id+"F12.opExtrude","SWEPT_FACE",FACE,{"disambiguationData":[OSD([sQuery(id+"F11.wireOp",EDGE,"200c0ae8-db39-47c0-8c74-e07b8066f8af")])]})]});
            var Q294;
            Q294=makeQuery(id+"F12.boolean.opBoolean","INTERSECT",EDGE,{"derivedFrom":[makeQuery(id+"F1.opExtrude","SWEPT_FACE",FACE,{"disambiguationData":[OSD([sQuery(id+"F0.wireOp",EDGE,"E0")])]}),makeQuery(id+"F12.opExtrude","SWEPT_FACE",FACE,{"disambiguationData":[OSD([sQuery(id+"F11.wireOp",EDGE,"e97e0156-3522-47dd-9f51-3a33e541eac2")])]})]});
            var Q295;
            Q295=makeQuery(id+"F12.boolean.opBoolean","INTERSECT",EDGE,{"derivedFrom":[makeQuery(id+"F1.opExtrude","SWEPT_FACE",FACE,{"disambiguationData":[OSD([sQuery(id+"F0.wireOp",EDGE,"E0")])]}),makeQuery(id+"F12.opExtrude","SWEPT_FACE",FACE,{"disambiguationData":[OSD([sQuery(id+"F11.wireOp",EDGE,"adce909b-9e2c-4011-806a-5ba738e49197")])]})]});
            var Q296;
            Q296=makeQuery(id+"F12.boolean.opBoolean","INTERSECT",EDGE,{"derivedFrom":[makeQuery(id+"F1.opExtrude","SWEPT_FACE",FACE,{"disambiguationData":[OSD([sQuery(id+"F0.wireOp",EDGE,"E0")])]}),makeQuery(id+"F12.opExtrude","SWEPT_FACE",FACE,{"disambiguationData":[OSD([sQuery(id+"F11.wireOp",EDGE,"cd0ca915-f2ce-4b21-a4ef-a866892009df")])]})]});
            var Q297;
            Q297=makeQuery(id+"F12.boolean.opBoolean","INTERSECT",EDGE,{"derivedFrom":[makeQuery(id+"F1.opExtrude","SWEPT_FACE",FACE,{"disambiguationData":[OSD([sQuery(id+"F0.wireOp",EDGE,"E0")])]}),makeQuery(id+"F12.opExtrude","SWEPT_FACE",FACE,{"disambiguationData":[OSD([sQuery(id+"F11.wireOp",EDGE,"566c1776-e442-4c1a-8a27-e67b73d4de07")])]})]});
            var Q298;
            Q298=makeQuery(id+"F12.boolean.opBoolean","INTERSECT",EDGE,{"derivedFrom":[makeQuery(id+"F1.opExtrude","SWEPT_FACE",FACE,{"disambiguationData":[OSD([sQuery(id+"F0.wireOp",EDGE,"E0")])]}),makeQuery(id+"F12.opExtrude","SWEPT_FACE",FACE,{"disambiguationData":[OSD([sQuery(id+"F11.wireOp",EDGE,"b2e68df8-0d34-48a2-85ed-ba0c7cba7b83")])]})]});
            var Q299;
            Q299=makeQuery(id+"F12.boolean.opBoolean","INTERSECT",EDGE,{"derivedFrom":[makeQuery(id+"F1.opExtrude","SWEPT_FACE",FACE,{"disambiguationData":[OSD([sQuery(id+"F0.wireOp",EDGE,"E0")])]}),makeQuery(id+"F12.opExtrude","SWEPT_FACE",FACE,{"disambiguationData":[OSD([sQuery(id+"F11.wireOp",EDGE,"a95edd79-1df3-4cd4-b19e-80dde6a9dddc")])]})]});
            var Q300;
            Q300=makeQuery(id+"F12.boolean.opBoolean","INTERSECT",EDGE,{"derivedFrom":[makeQuery(id+"F1.opExtrude","SWEPT_FACE",FACE,{"disambiguationData":[OSD([sQuery(id+"F0.wireOp",EDGE,"E0")])]}),makeQuery(id+"F12.opExtrude","SWEPT_FACE",FACE,{"disambiguationData":[OSD([sQuery(id+"F11.wireOp",EDGE,"7bac7bb8-7502-49c0-8bc5-64d494245f90")])]})]});
            var Q301;
            Q301=makeQuery(id+"F12.boolean.opBoolean","INTERSECT",EDGE,{"derivedFrom":[makeQuery(id+"F1.opExtrude","SWEPT_FACE",FACE,{"disambiguationData":[OSD([sQuery(id+"F0.wireOp",EDGE,"E0")])]}),makeQuery(id+"F12.opExtrude","SWEPT_FACE",FACE,{"disambiguationData":[OSD([sQuery(id+"F11.wireOp",EDGE,"0a6e00ce-b892-4f90-b503-7d4f459e09b7")])]})]});
            var Q302;
            Q302=makeQuery(id+"F12.boolean.opBoolean","INTERSECT",EDGE,{"derivedFrom":[makeQuery(id+"F1.opExtrude","SWEPT_FACE",FACE,{"disambiguationData":[OSD([sQuery(id+"F0.wireOp",EDGE,"E0")])]}),makeQuery(id+"F12.opExtrude","SWEPT_FACE",FACE,{"disambiguationData":[OSD([sQuery(id+"F11.wireOp",EDGE,"1c4190f5-12c8-4d12-a8ea-2983d30e1d65")])]})]});
            var Q303;
            Q303=makeQuery(id+"F12.boolean.opBoolean","INTERSECT",EDGE,{"derivedFrom":[makeQuery(id+"F1.opExtrude","SWEPT_FACE",FACE,{"disambiguationData":[OSD([sQuery(id+"F0.wireOp",EDGE,"E0")])]}),makeQuery(id+"F12.opExtrude","SWEPT_FACE",FACE,{"disambiguationData":[OSD([sQuery(id+"F11.wireOp",EDGE,"8c0447c6-60ba-4edd-8488-664759495711")])]})]});
            var Q304;
            Q304=makeQuery(id+"F12.boolean.opBoolean","INTERSECT",EDGE,{"derivedFrom":[makeQuery(id+"F1.opExtrude","SWEPT_FACE",FACE,{"disambiguationData":[OSD([sQuery(id+"F0.wireOp",EDGE,"E0")])]}),makeQuery(id+"F12.opExtrude","SWEPT_FACE",FACE,{"disambiguationData":[OSD([sQuery(id+"F11.wireOp",EDGE,"5dfe9654-666d-4f3e-bb59-82f642316b6d")])]})]});
            var Q305;
            Q305=makeQuery(id+"F12.boolean.opBoolean","INTERSECT",EDGE,{"derivedFrom":[makeQuery(id+"F1.opExtrude","SWEPT_FACE",FACE,{"disambiguationData":[OSD([sQuery(id+"F0.wireOp",EDGE,"E0")])]}),makeQuery(id+"F12.opExtrude","SWEPT_FACE",FACE,{"disambiguationData":[OSD([sQuery(id+"F11.wireOp",EDGE,"841d8487-d472-43f1-bdbd-e7ff6b45cd41")])]})]});
            var Q306;
            Q306=makeQuery(id+"F12.boolean.opBoolean","INTERSECT",EDGE,{"derivedFrom":[makeQuery(id+"F1.opExtrude","SWEPT_FACE",FACE,{"disambiguationData":[OSD([sQuery(id+"F0.wireOp",EDGE,"E0")])]}),makeQuery(id+"F12.opExtrude","SWEPT_FACE",FACE,{"disambiguationData":[OSD([sQuery(id+"F11.wireOp",EDGE,"6e0252a6-974a-4586-a4a8-83f366333a88")])]})]});
            var Q307;
            Q307=makeQuery(id+"F12.boolean.opBoolean","INTERSECT",EDGE,{"derivedFrom":[makeQuery(id+"F1.opExtrude","SWEPT_FACE",FACE,{"disambiguationData":[OSD([sQuery(id+"F0.wireOp",EDGE,"E0")])]}),makeQuery(id+"F12.opExtrude","SWEPT_FACE",FACE,{"disambiguationData":[OSD([sQuery(id+"F11.wireOp",EDGE,"30b1511e-e2ca-4772-9673-cf06763b7aad")])]})]});
            var Q308;
            Q308=makeQuery(id+"F12.boolean.opBoolean","INTERSECT",EDGE,{"derivedFrom":[makeQuery(id+"F1.opExtrude","SWEPT_FACE",FACE,{"disambiguationData":[OSD([sQuery(id+"F0.wireOp",EDGE,"E0")])]}),makeQuery(id+"F12.opExtrude","SWEPT_FACE",FACE,{"disambiguationData":[OSD([sQuery(id+"F11.wireOp",EDGE,"6ca8cd86-5e60-4f71-aece-58a5cefb0301")])]})]});
            var Q309;
            Q309=makeQuery(id+"F12.boolean.opBoolean","INTERSECT",EDGE,{"derivedFrom":[makeQuery(id+"F1.opExtrude","SWEPT_FACE",FACE,{"disambiguationData":[OSD([sQuery(id+"F0.wireOp",EDGE,"E0")])]}),makeQuery(id+"F12.opExtrude","SWEPT_FACE",FACE,{"disambiguationData":[OSD([sQuery(id+"F11.wireOp",EDGE,"66b1be52-5d7b-488e-ab88-be7fc1489788")])]})]});
            var Q310;
            Q310=makeQuery(id+"F12.boolean.opBoolean","INTERSECT",EDGE,{"derivedFrom":[makeQuery(id+"F1.opExtrude","SWEPT_FACE",FACE,{"disambiguationData":[OSD([sQuery(id+"F0.wireOp",EDGE,"E0")])]}),makeQuery(id+"F12.opExtrude","SWEPT_FACE",FACE,{"disambiguationData":[OSD([sQuery(id+"F11.wireOp",EDGE,"a826e480-ba9d-454b-a154-b724fcca502a")])]})]});
            var Q311;
            Q311=makeQuery(id+"F12.boolean.opBoolean","INTERSECT",EDGE,{"derivedFrom":[makeQuery(id+"F1.opExtrude","SWEPT_FACE",FACE,{"disambiguationData":[OSD([sQuery(id+"F0.wireOp",EDGE,"E0")])]}),makeQuery(id+"F12.opExtrude","SWEPT_FACE",FACE,{"disambiguationData":[OSD([sQuery(id+"F11.wireOp",EDGE,"07a74ef0-9ede-4776-8ebf-e754756c114a")])]})]});
            var Q312;
            Q312=makeQuery(id+"F12.boolean.opBoolean","INTERSECT",EDGE,{"derivedFrom":[makeQuery(id+"F1.opExtrude","SWEPT_FACE",FACE,{"disambiguationData":[OSD([sQuery(id+"F0.wireOp",EDGE,"E0")])]}),makeQuery(id+"F12.opExtrude","SWEPT_FACE",FACE,{"disambiguationData":[OSD([sQuery(id+"F11.wireOp",EDGE,"092ed403-3d4f-4c15-960d-c10ef8789eb5")])]})]});
            var Q313;
            Q313=makeQuery(id+"F12.boolean.opBoolean","INTERSECT",EDGE,{"derivedFrom":[makeQuery(id+"F1.opExtrude","SWEPT_FACE",FACE,{"disambiguationData":[OSD([sQuery(id+"F0.wireOp",EDGE,"E0")])]}),makeQuery(id+"F12.opExtrude","SWEPT_FACE",FACE,{"disambiguationData":[OSD([sQuery(id+"F11.wireOp",EDGE,"acb8dcbc-daed-461c-af8b-853c71a07eac")])]})]});
            var Q314;
            Q314=makeQuery(id+"F12.boolean.opBoolean","INTERSECT",EDGE,{"derivedFrom":[makeQuery(id+"F1.opExtrude","SWEPT_FACE",FACE,{"disambiguationData":[OSD([sQuery(id+"F0.wireOp",EDGE,"E0")])]}),makeQuery(id+"F12.opExtrude","SWEPT_FACE",FACE,{"disambiguationData":[OSD([sQuery(id+"F11.wireOp",EDGE,"76158571-8428-4aec-bd47-33adf174f2a4")])]})]});
            var Q315;
            Q315=makeQuery(id+"F12.boolean.opBoolean","INTERSECT",EDGE,{"derivedFrom":[makeQuery(id+"F1.opExtrude","SWEPT_FACE",FACE,{"disambiguationData":[OSD([sQuery(id+"F0.wireOp",EDGE,"E0")])]}),makeQuery(id+"F12.opExtrude","SWEPT_FACE",FACE,{"disambiguationData":[OSD([sQuery(id+"F11.wireOp",EDGE,"2e92792f-4c7e-4468-9ae2-ab93ba844d4b")])]})]});
            var Q316;
            Q316=makeQuery(id+"F12.boolean.opBoolean","INTERSECT",EDGE,{"derivedFrom":[makeQuery(id+"F1.opExtrude","SWEPT_FACE",FACE,{"disambiguationData":[OSD([sQuery(id+"F0.wireOp",EDGE,"E0")])]}),makeQuery(id+"F12.opExtrude","SWEPT_FACE",FACE,{"disambiguationData":[OSD([sQuery(id+"F11.wireOp",EDGE,"b0197f1f-3212-4fe7-853f-974a1a9ee185")])]})]});
            var Q317;
            Q317=makeQuery(id+"F12.boolean.opBoolean","INTERSECT",EDGE,{"derivedFrom":[makeQuery(id+"F1.opExtrude","SWEPT_FACE",FACE,{"disambiguationData":[OSD([sQuery(id+"F0.wireOp",EDGE,"E0")])]}),makeQuery(id+"F12.opExtrude","SWEPT_FACE",FACE,{"disambiguationData":[OSD([sQuery(id+"F11.wireOp",EDGE,"faa93db1-9b94-4bc8-a4df-a69461af7118")])]})]});
            var Q318;
            Q318=makeQuery(id+"F12.boolean.opBoolean","INTERSECT",EDGE,{"derivedFrom":[makeQuery(id+"F1.opExtrude","SWEPT_FACE",FACE,{"disambiguationData":[OSD([sQuery(id+"F0.wireOp",EDGE,"E0")])]}),makeQuery(id+"F12.opExtrude","SWEPT_FACE",FACE,{"disambiguationData":[OSD([sQuery(id+"F11.wireOp",EDGE,"bf553eab-f362-4974-a638-a7733928a928")])]})]});
            var Q319;
            Q319=makeQuery(id+"F12.boolean.opBoolean","INTERSECT",EDGE,{"derivedFrom":[makeQuery(id+"F1.opExtrude","SWEPT_FACE",FACE,{"disambiguationData":[OSD([sQuery(id+"F0.wireOp",EDGE,"E0")])]}),makeQuery(id+"F12.opExtrude","SWEPT_FACE",FACE,{"disambiguationData":[OSD([sQuery(id+"F11.wireOp",EDGE,"80697549-b82d-4dee-9442-59f5951ca8b8")])]})]});
            var Q320;
            Q320=makeQuery(id+"F12.boolean.opBoolean","INTERSECT",EDGE,{"derivedFrom":[makeQuery(id+"F1.opExtrude","SWEPT_FACE",FACE,{"disambiguationData":[OSD([sQuery(id+"F0.wireOp",EDGE,"E0")])]}),makeQuery(id+"F12.opExtrude","SWEPT_FACE",FACE,{"disambiguationData":[OSD([sQuery(id+"F11.wireOp",EDGE,"0e8c3faf-8d29-4084-8698-73abd46cf39c")])]})]});
            var Q321;
            Q321=makeQuery(id+"F12.boolean.opBoolean","INTERSECT",EDGE,{"derivedFrom":[makeQuery(id+"F1.opExtrude","SWEPT_FACE",FACE,{"disambiguationData":[OSD([sQuery(id+"F0.wireOp",EDGE,"E0")])]}),makeQuery(id+"F12.opExtrude","SWEPT_FACE",FACE,{"disambiguationData":[OSD([sQuery(id+"F11.wireOp",EDGE,"2d858d98-3365-4601-99b5-01ed8230ce64")])]})]});
            var Q322;
            Q322=makeQuery(id+"F12.boolean.opBoolean","INTERSECT",EDGE,{"derivedFrom":[makeQuery(id+"F1.opExtrude","SWEPT_FACE",FACE,{"disambiguationData":[OSD([sQuery(id+"F0.wireOp",EDGE,"E0")])]}),makeQuery(id+"F12.opExtrude","SWEPT_FACE",FACE,{"disambiguationData":[OSD([sQuery(id+"F11.wireOp",EDGE,"6bbfbd9f-83cf-4e5a-8c48-5f02fa0a9c69")])]})]});
            var Q323;
            Q323=makeQuery(id+"F12.boolean.opBoolean","INTERSECT",EDGE,{"derivedFrom":[makeQuery(id+"F1.opExtrude","SWEPT_FACE",FACE,{"disambiguationData":[OSD([sQuery(id+"F0.wireOp",EDGE,"E0")])]}),makeQuery(id+"F12.opExtrude","SWEPT_FACE",FACE,{"disambiguationData":[OSD([sQuery(id+"F11.wireOp",EDGE,"8a950ba1-a090-4c8d-82b9-cd5225b2b9e3")])]})]});
            var Q324;
            Q324=makeQuery(id+"F12.boolean.opBoolean","INTERSECT",EDGE,{"derivedFrom":[makeQuery(id+"F1.opExtrude","SWEPT_FACE",FACE,{"disambiguationData":[OSD([sQuery(id+"F0.wireOp",EDGE,"E0")])]}),makeQuery(id+"F12.opExtrude","SWEPT_FACE",FACE,{"disambiguationData":[OSD([sQuery(id+"F11.wireOp",EDGE,"de11c3ef-7a1d-4805-b947-306e5608d462")])]})]});
            var Q325;
            Q325=makeQuery(id+"F12.boolean.opBoolean","INTERSECT",EDGE,{"derivedFrom":[makeQuery(id+"F1.opExtrude","SWEPT_FACE",FACE,{"disambiguationData":[OSD([sQuery(id+"F0.wireOp",EDGE,"E0")])]}),makeQuery(id+"F12.opExtrude","SWEPT_FACE",FACE,{"disambiguationData":[OSD([sQuery(id+"F11.wireOp",EDGE,"5fc31a4b-0bb3-428e-9063-e62cabce7d17")])]})]});
            var Q326;
            Q326=makeQuery(id+"F12.boolean.opBoolean","INTERSECT",EDGE,{"derivedFrom":[makeQuery(id+"F1.opExtrude","SWEPT_FACE",FACE,{"disambiguationData":[OSD([sQuery(id+"F0.wireOp",EDGE,"E0")])]}),makeQuery(id+"F12.opExtrude","SWEPT_FACE",FACE,{"disambiguationData":[OSD([sQuery(id+"F11.wireOp",EDGE,"2fde0330-21a3-47f8-95e4-c6b2125bc28d")])]})]});
            var Q327;
            Q327=makeQuery(id+"F12.boolean.opBoolean","INTERSECT",EDGE,{"derivedFrom":[makeQuery(id+"F1.opExtrude","SWEPT_FACE",FACE,{"disambiguationData":[OSD([sQuery(id+"F0.wireOp",EDGE,"E0")])]}),makeQuery(id+"F12.opExtrude","SWEPT_FACE",FACE,{"disambiguationData":[OSD([sQuery(id+"F11.wireOp",EDGE,"39ea25aa-dc9d-413d-aca9-5b751d16431b")])]})]});
            var Q328;
            Q328=makeQuery(id+"F12.boolean.opBoolean","INTERSECT",EDGE,{"derivedFrom":[makeQuery(id+"F1.opExtrude","SWEPT_FACE",FACE,{"disambiguationData":[OSD([sQuery(id+"F0.wireOp",EDGE,"E0")])]}),makeQuery(id+"F12.opExtrude","SWEPT_FACE",FACE,{"disambiguationData":[OSD([sQuery(id+"F11.wireOp",EDGE,"45a08d57-ac6c-4e91-8221-61a5d03ef4d8")])]})]});
            var Q329;
            Q329=makeQuery(id+"F12.boolean.opBoolean","INTERSECT",EDGE,{"derivedFrom":[makeQuery(id+"F1.opExtrude","SWEPT_FACE",FACE,{"disambiguationData":[OSD([sQuery(id+"F0.wireOp",EDGE,"E0")])]}),makeQuery(id+"F12.opExtrude","SWEPT_FACE",FACE,{"disambiguationData":[OSD([sQuery(id+"F11.wireOp",EDGE,"ae00799b-1def-4a87-a375-c2745601d105")])]})]});
            var Q330;
            Q330=makeQuery(id+"F12.boolean.opBoolean","INTERSECT",EDGE,{"derivedFrom":[makeQuery(id+"F1.opExtrude","SWEPT_FACE",FACE,{"disambiguationData":[OSD([sQuery(id+"F0.wireOp",EDGE,"E0")])]}),makeQuery(id+"F12.opExtrude","SWEPT_FACE",FACE,{"disambiguationData":[OSD([sQuery(id+"F11.wireOp",EDGE,"04f7a225-5764-4d5d-9f0d-af1fe46beb71")])]})]});
            var Q331;
            Q331=makeQuery(id+"F12.boolean.opBoolean","INTERSECT",EDGE,{"derivedFrom":[makeQuery(id+"F1.opExtrude","SWEPT_FACE",FACE,{"disambiguationData":[OSD([sQuery(id+"F0.wireOp",EDGE,"E0")])]}),makeQuery(id+"F12.opExtrude","SWEPT_FACE",FACE,{"disambiguationData":[OSD([sQuery(id+"F11.wireOp",EDGE,"874c3c57-a6bb-4400-9591-b6c49b54f0d5")])]})]});
            var Q332;
            Q332=makeQuery(id+"F12.boolean.opBoolean","INTERSECT",EDGE,{"derivedFrom":[makeQuery(id+"F1.opExtrude","SWEPT_FACE",FACE,{"disambiguationData":[OSD([sQuery(id+"F0.wireOp",EDGE,"E0")])]}),makeQuery(id+"F12.opExtrude","SWEPT_FACE",FACE,{"disambiguationData":[OSD([sQuery(id+"F11.wireOp",EDGE,"46c9ed28-b344-407f-a562-7c22284d55fe")])]})]});
            var Q333;
            Q333=makeQuery(id+"F12.boolean.opBoolean","INTERSECT",EDGE,{"derivedFrom":[makeQuery(id+"F1.opExtrude","SWEPT_FACE",FACE,{"disambiguationData":[OSD([sQuery(id+"F0.wireOp",EDGE,"E0")])]}),makeQuery(id+"F12.opExtrude","SWEPT_FACE",FACE,{"disambiguationData":[OSD([sQuery(id+"F11.wireOp",EDGE,"62da7513-9491-427f-938b-696b47152ffd")])]})]});
            var Q334;
            Q334=makeQuery(id+"F12.boolean.opBoolean","INTERSECT",EDGE,{"derivedFrom":[makeQuery(id+"F1.opExtrude","SWEPT_FACE",FACE,{"disambiguationData":[OSD([sQuery(id+"F0.wireOp",EDGE,"E0")])]}),makeQuery(id+"F12.opExtrude","SWEPT_FACE",FACE,{"disambiguationData":[OSD([sQuery(id+"F11.wireOp",EDGE,"aa06bcb9-a86b-4f86-a9b4-85c86a1af446")])]})]});
            var Q335;
            Q335=makeQuery(id+"F12.boolean.opBoolean","INTERSECT",EDGE,{"derivedFrom":[makeQuery(id+"F1.opExtrude","SWEPT_FACE",FACE,{"disambiguationData":[OSD([sQuery(id+"F0.wireOp",EDGE,"E0")])]}),makeQuery(id+"F12.opExtrude","SWEPT_FACE",FACE,{"disambiguationData":[OSD([sQuery(id+"F11.wireOp",EDGE,"39fdaf24-626d-4be9-ae9c-25e924fe0a02")])]})]});
            var Q336;
            Q336=makeQuery(id+"F12.boolean.opBoolean","INTERSECT",EDGE,{"derivedFrom":[makeQuery(id+"F1.opExtrude","SWEPT_FACE",FACE,{"disambiguationData":[OSD([sQuery(id+"F0.wireOp",EDGE,"E0")])]}),makeQuery(id+"F12.opExtrude","SWEPT_FACE",FACE,{"disambiguationData":[OSD([sQuery(id+"F11.wireOp",EDGE,"25193117-9b4b-42b4-a85a-958f9bb3fb66")])]})]});
            var Q337;
            Q337=makeQuery(id+"F12.boolean.opBoolean","INTERSECT",EDGE,{"derivedFrom":[makeQuery(id+"F1.opExtrude","SWEPT_FACE",FACE,{"disambiguationData":[OSD([sQuery(id+"F0.wireOp",EDGE,"E0")])]}),makeQuery(id+"F12.opExtrude","SWEPT_FACE",FACE,{"disambiguationData":[OSD([sQuery(id+"F11.wireOp",EDGE,"2c336ab2-bfc0-43d3-a329-a216c8d1b87b")])]})]});
            var Q338;
            Q338=makeQuery(id+"F12.boolean.opBoolean","INTERSECT",EDGE,{"derivedFrom":[makeQuery(id+"F1.opExtrude","SWEPT_FACE",FACE,{"disambiguationData":[OSD([sQuery(id+"F0.wireOp",EDGE,"E0")])]}),makeQuery(id+"F12.opExtrude","SWEPT_FACE",FACE,{"disambiguationData":[OSD([sQuery(id+"F11.wireOp",EDGE,"64d6da3b-8a0c-46ea-a12b-d14f425ae2f6")])]})]});
            var Q339;
            Q339=makeQuery(id+"F12.boolean.opBoolean","INTERSECT",EDGE,{"derivedFrom":[makeQuery(id+"F1.opExtrude","SWEPT_FACE",FACE,{"disambiguationData":[OSD([sQuery(id+"F0.wireOp",EDGE,"E0")])]}),makeQuery(id+"F12.opExtrude","SWEPT_FACE",FACE,{"disambiguationData":[OSD([sQuery(id+"F11.wireOp",EDGE,"d1064973-f400-4dc1-ab4f-e9b9d72f416c")])]})]});
            var Q340;
            Q340=makeQuery(id+"F12.boolean.opBoolean","INTERSECT",EDGE,{"derivedFrom":[makeQuery(id+"F1.opExtrude","SWEPT_FACE",FACE,{"disambiguationData":[OSD([sQuery(id+"F0.wireOp",EDGE,"E0")])]}),makeQuery(id+"F12.opExtrude","SWEPT_FACE",FACE,{"disambiguationData":[OSD([sQuery(id+"F11.wireOp",EDGE,"368e7495-1394-477b-bb01-d5cedc0a1b70")])]})]});
            var Q341;
            Q341=makeQuery(id+"F12.boolean.opBoolean","INTERSECT",EDGE,{"derivedFrom":[makeQuery(id+"F1.opExtrude","SWEPT_FACE",FACE,{"disambiguationData":[OSD([sQuery(id+"F0.wireOp",EDGE,"E0")])]}),makeQuery(id+"F12.opExtrude","SWEPT_FACE",FACE,{"disambiguationData":[OSD([sQuery(id+"F11.wireOp",EDGE,"50bbaaba-c4f5-4406-8380-98ff907eccc0")])]})]});
            var Q342;
            Q342=makeQuery(id+"F12.boolean.opBoolean","INTERSECT",EDGE,{"derivedFrom":[makeQuery(id+"F1.opExtrude","SWEPT_FACE",FACE,{"disambiguationData":[OSD([sQuery(id+"F0.wireOp",EDGE,"E0")])]}),makeQuery(id+"F12.opExtrude","SWEPT_FACE",FACE,{"disambiguationData":[OSD([sQuery(id+"F11.wireOp",EDGE,"252ab781-f89f-493a-a601-3851de4bca54")])]})]});
            var Q343;
            Q343=makeQuery(id+"F12.boolean.opBoolean","INTERSECT",EDGE,{"derivedFrom":[makeQuery(id+"F1.opExtrude","SWEPT_FACE",FACE,{"disambiguationData":[OSD([sQuery(id+"F0.wireOp",EDGE,"E0")])]}),makeQuery(id+"F12.opExtrude","SWEPT_FACE",FACE,{"disambiguationData":[OSD([sQuery(id+"F11.wireOp",EDGE,"077e507b-792a-4822-bd42-40c28a37b443")])]})]});
            var Q344;
            Q344=makeQuery(id+"F12.boolean.opBoolean","INTERSECT",EDGE,{"derivedFrom":[makeQuery(id+"F1.opExtrude","SWEPT_FACE",FACE,{"disambiguationData":[OSD([sQuery(id+"F0.wireOp",EDGE,"E0")])]}),makeQuery(id+"F12.opExtrude","SWEPT_FACE",FACE,{"disambiguationData":[OSD([sQuery(id+"F11.wireOp",EDGE,"041bb2eb-ae03-41b4-8679-2ee14c3b35eb")])]})]});
            var Q345;
            Q345=makeQuery(id+"F12.boolean.opBoolean","INTERSECT",EDGE,{"derivedFrom":[makeQuery(id+"F1.opExtrude","SWEPT_FACE",FACE,{"disambiguationData":[OSD([sQuery(id+"F0.wireOp",EDGE,"E0")])]}),makeQuery(id+"F12.opExtrude","SWEPT_FACE",FACE,{"disambiguationData":[OSD([sQuery(id+"F11.wireOp",EDGE,"e56254bb-4933-495c-a375-924da8ba2d97"),sQuery(id+"F11.wireOp",EDGE,"2da46073-95db-4ae7-83f6-e80e428f4fd1")])]})]});
            var Q346;
            Q346=makeQuery(id+"F12.boolean.opBoolean","INTERSECT",EDGE,{"derivedFrom":[makeQuery(id+"F1.opExtrude","SWEPT_FACE",FACE,{"disambiguationData":[OSD([sQuery(id+"F0.wireOp",EDGE,"E0")])]}),makeQuery(id+"F12.opExtrude","SWEPT_FACE",FACE,{"disambiguationData":[OSD([sQuery(id+"F11.wireOp",EDGE,"09fa856f-861a-4983-bd95-702295a2dd2e")])]})]});
            var Q347;
            Q347=makeQuery(id+"F10.boolean.opBoolean","INTERSECT",EDGE,{"disambiguationData":[OD(1.0)],"derivedFrom":[makeQuery(id+"F1.opExtrude","SWEPT_FACE",FACE,{"disambiguationData":[OSD([sQuery(id+"F0.wireOp",EDGE,"E0")])]}),makeQuery(id+"F10.opExtrude","SWEPT_FACE",FACE,{"disambiguationData":[OSD([sQuery(id+"F9.wireOp",EDGE,"2e52e4ba-a856-43cc-8b69-bc95ae584be1")])]})]});
            var Q348;
            Q348=makeQuery(id+"F10.boolean.opBoolean","INTERSECT",EDGE,{"disambiguationData":[OD(1.0)],"derivedFrom":[makeQuery(id+"F1.opExtrude","SWEPT_FACE",FACE,{"disambiguationData":[OSD([sQuery(id+"F0.wireOp",EDGE,"E0")])]}),makeQuery(id+"F10.opExtrude","SWEPT_FACE",FACE,{"disambiguationData":[OSD([sQuery(id+"F9.wireOp",EDGE,"d68f23c5-fa44-4f68-a5e1-914856eae846")])]})]});
            var Q349;
            Q349=makeQuery(id+"F10.boolean.opBoolean","INTERSECT",EDGE,{"disambiguationData":[OD(1.0)],"derivedFrom":[makeQuery(id+"F1.opExtrude","SWEPT_FACE",FACE,{"disambiguationData":[OSD([sQuery(id+"F0.wireOp",EDGE,"E0")])]}),makeQuery(id+"F10.opExtrude","SWEPT_FACE",FACE,{"disambiguationData":[OSD([sQuery(id+"F9.wireOp",EDGE,"3921cf77-2c7d-4081-b0dc-8dd1674662ff")])]})]});
            var Q350;
            Q350=makeQuery(id+"F7.boolean.opBoolean","INTERSECT",EDGE,{"disambiguationData":[OD(0.0)],"derivedFrom":[makeQuery(id+"F1.opExtrude","SWEPT_FACE",FACE,{"disambiguationData":[OSD([sQuery(id+"F0.wireOp",EDGE,"E0")])]}),makeQuery(id+"F7.opExtrude","SWEPT_FACE",FACE,{"disambiguationData":[OSD([sQuery(id+"F6.wireOp",EDGE,"E8.0")])]})]});
            var Q351;
            Q351=makeQuery(id+"F7.boolean.opBoolean","INTERSECT",EDGE,{"disambiguationData":[OD(0.0)],"derivedFrom":[makeQuery(id+"F1.opExtrude","SWEPT_FACE",FACE,{"disambiguationData":[OSD([sQuery(id+"F0.wireOp",EDGE,"E0")])]}),makeQuery(id+"F7.opExtrude","SWEPT_FACE",FACE,{"disambiguationData":[OSD([sQuery(id+"F6.wireOp",EDGE,"E8.5")])]})]});
            fillet(context, id + "F14", {"entities" : qUnion([Q0, Q1, Q2, Q3, Q4, Q5, Q6, Q7, Q8, Q9, Q10, Q11, Q12, Q13, Q14, Q15, Q16, Q17, Q18, Q19, Q20, Q21, Q22, Q23, Q24, Q25, Q26, Q27, Q28, Q29, Q30, Q31, Q32, Q33, Q34, Q35, Q36, Q37, Q38, Q39, Q40, Q41, Q42, Q43, Q44, Q45, Q46, Q47, Q48, Q49, Q50, Q51, Q52, Q53, Q54, Q55, Q56, Q57, Q58, Q59, Q60, Q61, Q62, Q63, Q64, Q65, Q66, Q67, Q68, Q69, Q70, Q71, Q72, Q73, Q74, Q75, Q76, Q77, Q78, Q79, Q80, Q81, Q82, Q83, Q84, Q85, Q86, Q87, Q88, Q89, Q90, Q91, Q92, Q93, Q94, Q95, Q96, Q97, Q98, Q99, Q100, Q101, Q102, Q103, Q104, Q105, Q106, Q107, Q108, Q109, Q110, Q111, Q112, Q113, Q114, Q115, Q116, Q117, Q118, Q119, Q120, Q121, Q122, Q123, Q124, Q125, Q126, Q127, Q128, Q129, Q130, Q131, Q132, Q133, Q134, Q135, Q136, Q137, Q138, Q139, Q140, Q141, Q142, Q143, Q144, Q145, Q146, Q147, Q148, Q149, Q150, Q151, Q152, Q153, Q154, Q155, Q156, Q157, Q158, Q159, Q160, Q161, Q162, Q163, Q164, Q165, Q166, Q167, Q168, Q169, Q170, Q171, Q172, Q173, Q174, Q175, Q176, Q177, Q178, Q179, Q180, Q181, Q182, Q183, Q184, Q185, Q186, Q187, Q188, Q189, Q190, Q191, Q192, Q193, Q194, Q195, Q196, Q197, Q198, Q199, Q200, Q201, Q202, Q203, Q204, Q205, Q206, Q207, Q208, Q209, Q210, Q211, Q212, Q213, Q214, Q215, Q216, Q217, Q218, Q219, Q220, Q221, Q222, Q223, Q224, Q225, Q226, Q227, Q228, Q229, Q230, Q231, Q232, Q233, Q234, Q235, Q236, Q237, Q238, Q239, Q240, Q241, Q242, Q243, Q244, Q245, Q246, Q247, Q248, Q249, Q250, Q251, Q252, Q253, Q254, Q255, Q256, Q257, Q258, Q259, Q260, Q261, Q262, Q263, Q264, Q265, Q266, Q267, Q268, Q269, Q270, Q271, Q272, Q273, Q274, Q275, Q276, Q277, Q278, Q279, Q280, Q281, Q282, Q283, Q284, Q285, Q286, Q287, Q288, Q289, Q290, Q291, Q292, Q293, Q294, Q295, Q296, Q297, Q298, Q299, Q300, Q301, Q302, Q303, Q304, Q305, Q306, Q307, Q308, Q309, Q310, Q311, Q312, Q313, Q314, Q315, Q316, Q317, Q318, Q319, Q320, Q321, Q322, Q323, Q324, Q325, Q326, Q327, Q328, Q329, Q330, Q331, Q332, Q333, Q334, Q335, Q336, Q337, Q338, Q339, Q340, Q341, Q342, Q343, Q344, Q345, Q346, Q347, Q348, Q349, Q350, Q351]), "radius" : 0.7 * mm, "tangentPropagation" : true, "defaultsChanged" : true, "vertexSettings" : [], "allowEdgeOverflow" : false});
        }
        {
            var Q0;
            Q0=makeQuery(id+"F10.boolean.opBoolean","INTERSECT",EDGE,{"disambiguationData":[OD(0.0)],"derivedFrom":[makeQuery(id+"F1.opExtrude","SWEPT_FACE",FACE,{"disambiguationData":[OSD([sQuery(id+"F0.wireOp",EDGE,"E0")])]}),makeQuery(id+"F10.opExtrude","SWEPT_FACE",FACE,{"disambiguationData":[OSD([sQuery(id+"F9.wireOp",EDGE,"E28")])]})]});
            var Q1;
            Q1=makeQuery(id+"F10.boolean.opBoolean","INTERSECT",EDGE,{"disambiguationData":[OD(0.0)],"derivedFrom":[makeQuery(id+"F1.opExtrude","SWEPT_FACE",FACE,{"disambiguationData":[OSD([sQuery(id+"F0.wireOp",EDGE,"E0")])]}),makeQuery(id+"F10.opExtrude","SWEPT_FACE",FACE,{"disambiguationData":[OSD([sQuery(id+"F9.wireOp",EDGE,"E26"),sQuery(id+"F9.wireOp",EDGE,"E27")])]})]});
            var Q2;
            Q2=makeQuery(id+"F10.boolean.opBoolean","INTERSECT",EDGE,{"disambiguationData":[OD(0.0)],"derivedFrom":[makeQuery(id+"F1.opExtrude","SWEPT_FACE",FACE,{"disambiguationData":[OSD([sQuery(id+"F0.wireOp",EDGE,"E0")])]}),makeQuery(id+"F10.opExtrude","SWEPT_FACE",FACE,{"disambiguationData":[OSD([sQuery(id+"F9.wireOp",EDGE,"E29")])]})]});
            var Q3;
            Q3=makeQuery(id+"F10.boolean.opBoolean","INTERSECT",EDGE,{"disambiguationData":[OD(0.0)],"derivedFrom":[makeQuery(id+"F1.opExtrude","SWEPT_FACE",FACE,{"disambiguationData":[OSD([sQuery(id+"F0.wireOp",EDGE,"E0")])]}),makeQuery(id+"F10.opExtrude","SWEPT_FACE",FACE,{"disambiguationData":[OSD([sQuery(id+"F9.wireOp",EDGE,"E14.3")])]})]});
            var Q4;
            Q4=makeQuery(id+"F10.boolean.opBoolean","INTERSECT",EDGE,{"disambiguationData":[OD(0.0)],"derivedFrom":[makeQuery(id+"F1.opExtrude","SWEPT_FACE",FACE,{"disambiguationData":[OSD([sQuery(id+"F0.wireOp",EDGE,"E0")])]}),makeQuery(id+"F10.opExtrude","SWEPT_FACE",FACE,{"disambiguationData":[OSD([sQuery(id+"F9.wireOp",EDGE,"E14.2")])]})]});
            var Q5;
            Q5=makeQuery(id+"F10.boolean.opBoolean","INTERSECT",EDGE,{"disambiguationData":[OD(0.0)],"derivedFrom":[makeQuery(id+"F1.opExtrude","SWEPT_FACE",FACE,{"disambiguationData":[OSD([sQuery(id+"F0.wireOp",EDGE,"E0")])]}),makeQuery(id+"F10.opExtrude","SWEPT_FACE",FACE,{"disambiguationData":[OSD([sQuery(id+"F9.wireOp",EDGE,"E14.1")])]})]});
            var Q6;
            Q6=makeQuery(id+"F10.boolean.opBoolean","INTERSECT",EDGE,{"disambiguationData":[OD(0.0)],"derivedFrom":[makeQuery(id+"F1.opExtrude","SWEPT_FACE",FACE,{"disambiguationData":[OSD([sQuery(id+"F0.wireOp",EDGE,"E0")])]}),makeQuery(id+"F10.opExtrude","SWEPT_FACE",FACE,{"disambiguationData":[OSD([sQuery(id+"F9.wireOp",EDGE,"E14.0")])]})]});
            var Q7;
            Q7=makeQuery(id+"F10.boolean.opBoolean","INTERSECT",EDGE,{"disambiguationData":[OD(0.0)],"derivedFrom":[makeQuery(id+"F1.opExtrude","SWEPT_FACE",FACE,{"disambiguationData":[OSD([sQuery(id+"F0.wireOp",EDGE,"E0")])]}),makeQuery(id+"F10.opExtrude","SWEPT_FACE",FACE,{"disambiguationData":[OSD([sQuery(id+"F9.wireOp",EDGE,"E14.5")])]})]});
            var Q8;
            Q8=makeQuery(id+"F10.boolean.opBoolean","INTERSECT",EDGE,{"disambiguationData":[OD(0.0)],"derivedFrom":[makeQuery(id+"F1.opExtrude","SWEPT_FACE",FACE,{"disambiguationData":[OSD([sQuery(id+"F0.wireOp",EDGE,"E0")])]}),makeQuery(id+"F10.opExtrude","SWEPT_FACE",FACE,{"disambiguationData":[OSD([sQuery(id+"F9.wireOp",EDGE,"E14.4")])]})]});
            var Q9;
            Q9=makeQuery(id+"F10.boolean.opBoolean","INTERSECT",EDGE,{"disambiguationData":[OD(0.0)],"derivedFrom":[makeQuery(id+"F1.opExtrude","SWEPT_FACE",FACE,{"disambiguationData":[OSD([sQuery(id+"F0.wireOp",EDGE,"E0")])]}),makeQuery(id+"F10.opExtrude","SWEPT_FACE",FACE,{"disambiguationData":[OSD([sQuery(id+"F9.wireOp",EDGE,"E15.0.1.4")])]})]});
            var Q10;
            Q10=makeQuery(id+"F10.boolean.opBoolean","INTERSECT",EDGE,{"disambiguationData":[OD(0.0)],"derivedFrom":[makeQuery(id+"F1.opExtrude","SWEPT_FACE",FACE,{"disambiguationData":[OSD([sQuery(id+"F0.wireOp",EDGE,"E0")])]}),makeQuery(id+"F10.opExtrude","SWEPT_FACE",FACE,{"disambiguationData":[OSD([sQuery(id+"F9.wireOp",EDGE,"E15.0.1.7")])]})]});
            var Q11;
            Q11=makeQuery(id+"F10.boolean.opBoolean","INTERSECT",EDGE,{"disambiguationData":[OD(0.0)],"derivedFrom":[makeQuery(id+"F1.opExtrude","SWEPT_FACE",FACE,{"disambiguationData":[OSD([sQuery(id+"F0.wireOp",EDGE,"E0")])]}),makeQuery(id+"F10.opExtrude","SWEPT_FACE",FACE,{"disambiguationData":[OSD([sQuery(id+"F9.wireOp",EDGE,"E15.0.1.3")])]})]});
            var Q12;
            Q12=makeQuery(id+"F10.boolean.opBoolean","INTERSECT",EDGE,{"disambiguationData":[OD(0.0)],"derivedFrom":[makeQuery(id+"F1.opExtrude","SWEPT_FACE",FACE,{"disambiguationData":[OSD([sQuery(id+"F0.wireOp",EDGE,"E0")])]}),makeQuery(id+"F10.opExtrude","SWEPT_FACE",FACE,{"disambiguationData":[OSD([sQuery(id+"F9.wireOp",EDGE,"E15.0.1.2")])]})]});
            var Q13;
            Q13=makeQuery(id+"F10.boolean.opBoolean","INTERSECT",EDGE,{"disambiguationData":[OD(0.0)],"derivedFrom":[makeQuery(id+"F1.opExtrude","SWEPT_FACE",FACE,{"disambiguationData":[OSD([sQuery(id+"F0.wireOp",EDGE,"E0")])]}),makeQuery(id+"F10.opExtrude","SWEPT_FACE",FACE,{"disambiguationData":[OSD([sQuery(id+"F9.wireOp",EDGE,"E15.0.1.6")])]})]});
            var Q14;
            Q14=makeQuery(id+"F10.boolean.opBoolean","INTERSECT",EDGE,{"disambiguationData":[OD(0.0)],"derivedFrom":[makeQuery(id+"F1.opExtrude","SWEPT_FACE",FACE,{"disambiguationData":[OSD([sQuery(id+"F0.wireOp",EDGE,"E0")])]}),makeQuery(id+"F10.opExtrude","SWEPT_FACE",FACE,{"disambiguationData":[OSD([sQuery(id+"F9.wireOp",EDGE,"E15.0.1.5")])]})]});
            var Q15;
            Q15=makeQuery(id+"F10.boolean.opBoolean","INTERSECT",EDGE,{"disambiguationData":[OD(0.0)],"derivedFrom":[makeQuery(id+"F1.opExtrude","SWEPT_FACE",FACE,{"disambiguationData":[OSD([sQuery(id+"F0.wireOp",EDGE,"E0")])]}),makeQuery(id+"F10.opExtrude","SWEPT_FACE",FACE,{"disambiguationData":[OSD([sQuery(id+"F9.wireOp",EDGE,"E15.0.2.2")])]})]});
            var Q16;
            Q16=makeQuery(id+"F10.boolean.opBoolean","INTERSECT",EDGE,{"disambiguationData":[OD(0.0)],"derivedFrom":[makeQuery(id+"F1.opExtrude","SWEPT_FACE",FACE,{"disambiguationData":[OSD([sQuery(id+"F0.wireOp",EDGE,"E0")])]}),makeQuery(id+"F10.opExtrude","SWEPT_FACE",FACE,{"disambiguationData":[OSD([sQuery(id+"F9.wireOp",EDGE,"E15.0.2.6")])]})]});
            var Q17;
            Q17=makeQuery(id+"F10.boolean.opBoolean","COPY",EDGE,{"disambiguationData":[OD(0.0)],"derivedFrom":makeQuery(id+"F10.opExtrude","SWEPT_EDGE",EDGE,{"disambiguationData":[OSD([sQuery(id+"F9.wireOp",EDGE,"E15.0.2.6"),sQuery(id+"F9.wireOp",EDGE,"E15.0.2.7")])]})});
            var Q18;
            Q18=makeQuery(id+"F10.boolean.opBoolean","INTERSECT",EDGE,{"disambiguationData":[OD(0.0)],"derivedFrom":[makeQuery(id+"F1.opExtrude","SWEPT_FACE",FACE,{"disambiguationData":[OSD([sQuery(id+"F0.wireOp",EDGE,"E0")])]}),makeQuery(id+"F10.opExtrude","SWEPT_FACE",FACE,{"disambiguationData":[OSD([sQuery(id+"F9.wireOp",EDGE,"E15.0.2.5")])]})]});
            var Q19;
            Q19=makeQuery(id+"F10.boolean.opBoolean","INTERSECT",EDGE,{"disambiguationData":[OD(0.0)],"derivedFrom":[makeQuery(id+"F1.opExtrude","SWEPT_FACE",FACE,{"disambiguationData":[OSD([sQuery(id+"F0.wireOp",EDGE,"E0")])]}),makeQuery(id+"F10.opExtrude","SWEPT_FACE",FACE,{"disambiguationData":[OSD([sQuery(id+"F9.wireOp",EDGE,"E15.0.2.4")])]})]});
            var Q20;
            Q20=makeQuery(id+"F10.boolean.opBoolean","INTERSECT",EDGE,{"disambiguationData":[OD(0.0)],"derivedFrom":[makeQuery(id+"F1.opExtrude","SWEPT_FACE",FACE,{"disambiguationData":[OSD([sQuery(id+"F0.wireOp",EDGE,"E0")])]}),makeQuery(id+"F10.opExtrude","SWEPT_FACE",FACE,{"disambiguationData":[OSD([sQuery(id+"F9.wireOp",EDGE,"E15.0.2.3")])]})]});
            var Q21;
            Q21=makeQuery(id+"F10.boolean.opBoolean","INTERSECT",EDGE,{"disambiguationData":[OD(0.0)],"derivedFrom":[makeQuery(id+"F1.opExtrude","SWEPT_FACE",FACE,{"disambiguationData":[OSD([sQuery(id+"F0.wireOp",EDGE,"E0")])]}),makeQuery(id+"F10.opExtrude","SWEPT_FACE",FACE,{"disambiguationData":[OSD([sQuery(id+"F9.wireOp",EDGE,"E15.0.3.2")])]})]});
            var Q22;
            Q22=makeQuery(id+"F10.boolean.opBoolean","INTERSECT",EDGE,{"disambiguationData":[OD(0.0)],"derivedFrom":[makeQuery(id+"F1.opExtrude","SWEPT_FACE",FACE,{"disambiguationData":[OSD([sQuery(id+"F0.wireOp",EDGE,"E0")])]}),makeQuery(id+"F10.opExtrude","SWEPT_FACE",FACE,{"disambiguationData":[OSD([sQuery(id+"F9.wireOp",EDGE,"E15.0.3.6")])]})]});
            var Q23;
            Q23=makeQuery(id+"F10.boolean.opBoolean","COPY",EDGE,{"disambiguationData":[OD(0.0)],"derivedFrom":makeQuery(id+"F10.opExtrude","SWEPT_EDGE",EDGE,{"disambiguationData":[OSD([sQuery(id+"F9.wireOp",EDGE,"E15.0.3.6"),sQuery(id+"F9.wireOp",EDGE,"E15.0.3.7")])]})});
            var Q24;
            Q24=makeQuery(id+"F10.boolean.opBoolean","INTERSECT",EDGE,{"disambiguationData":[OD(0.0)],"derivedFrom":[makeQuery(id+"F1.opExtrude","SWEPT_FACE",FACE,{"disambiguationData":[OSD([sQuery(id+"F0.wireOp",EDGE,"E0")])]}),makeQuery(id+"F10.opExtrude","SWEPT_FACE",FACE,{"disambiguationData":[OSD([sQuery(id+"F9.wireOp",EDGE,"E15.0.3.5")])]})]});
            var Q25;
            Q25=makeQuery(id+"F10.boolean.opBoolean","INTERSECT",EDGE,{"disambiguationData":[OD(0.0)],"derivedFrom":[makeQuery(id+"F1.opExtrude","SWEPT_FACE",FACE,{"disambiguationData":[OSD([sQuery(id+"F0.wireOp",EDGE,"E0")])]}),makeQuery(id+"F10.opExtrude","SWEPT_FACE",FACE,{"disambiguationData":[OSD([sQuery(id+"F9.wireOp",EDGE,"E15.0.3.4")])]})]});
            var Q26;
            Q26=makeQuery(id+"F10.boolean.opBoolean","INTERSECT",EDGE,{"disambiguationData":[OD(0.0)],"derivedFrom":[makeQuery(id+"F1.opExtrude","SWEPT_FACE",FACE,{"disambiguationData":[OSD([sQuery(id+"F0.wireOp",EDGE,"E0")])]}),makeQuery(id+"F10.opExtrude","SWEPT_FACE",FACE,{"disambiguationData":[OSD([sQuery(id+"F9.wireOp",EDGE,"E15.0.3.3")])]})]});
            var Q27;
            Q27=makeQuery(id+"F10.boolean.opBoolean","INTERSECT",EDGE,{"disambiguationData":[OD(0.0)],"derivedFrom":[makeQuery(id+"F1.opExtrude","SWEPT_FACE",FACE,{"disambiguationData":[OSD([sQuery(id+"F0.wireOp",EDGE,"E0")])]}),makeQuery(id+"F10.opExtrude","SWEPT_FACE",FACE,{"disambiguationData":[OSD([sQuery(id+"F9.wireOp",EDGE,"E15.0.4.2")])]})]});
            var Q28;
            Q28=makeQuery(id+"F10.boolean.opBoolean","INTERSECT",EDGE,{"disambiguationData":[OD(0.0)],"derivedFrom":[makeQuery(id+"F1.opExtrude","SWEPT_FACE",FACE,{"disambiguationData":[OSD([sQuery(id+"F0.wireOp",EDGE,"E0")])]}),makeQuery(id+"F10.opExtrude","SWEPT_FACE",FACE,{"disambiguationData":[OSD([sQuery(id+"F9.wireOp",EDGE,"E15.0.5.2")])]})]});
            var Q29;
            Q29=makeQuery(id+"F10.boolean.opBoolean","INTERSECT",EDGE,{"disambiguationData":[OD(0.0)],"derivedFrom":[makeQuery(id+"F1.opExtrude","SWEPT_FACE",FACE,{"disambiguationData":[OSD([sQuery(id+"F0.wireOp",EDGE,"E0")])]}),makeQuery(id+"F10.opExtrude","SWEPT_FACE",FACE,{"disambiguationData":[OSD([sQuery(id+"F9.wireOp",EDGE,"E15.0.6.2")])]})]});
            var Q30;
            Q30=makeQuery(id+"F10.boolean.opBoolean","INTERSECT",EDGE,{"disambiguationData":[OD(0.0)],"derivedFrom":[makeQuery(id+"F1.opExtrude","SWEPT_FACE",FACE,{"disambiguationData":[OSD([sQuery(id+"F0.wireOp",EDGE,"E0")])]}),makeQuery(id+"F10.opExtrude","SWEPT_FACE",FACE,{"disambiguationData":[OSD([sQuery(id+"F9.wireOp",EDGE,"E15.0.7.2")])]})]});
            var Q31;
            Q31=makeQuery(id+"F10.boolean.opBoolean","INTERSECT",EDGE,{"disambiguationData":[OD(0.0)],"derivedFrom":[makeQuery(id+"F1.opExtrude","SWEPT_FACE",FACE,{"disambiguationData":[OSD([sQuery(id+"F0.wireOp",EDGE,"E0")])]}),makeQuery(id+"F10.opExtrude","SWEPT_FACE",FACE,{"disambiguationData":[OSD([sQuery(id+"F9.wireOp",EDGE,"E15.0.4.3")])]})]});
            var Q32;
            Q32=makeQuery(id+"F10.boolean.opBoolean","INTERSECT",EDGE,{"disambiguationData":[OD(0.0)],"derivedFrom":[makeQuery(id+"F1.opExtrude","SWEPT_FACE",FACE,{"disambiguationData":[OSD([sQuery(id+"F0.wireOp",EDGE,"E0")])]}),makeQuery(id+"F10.opExtrude","SWEPT_FACE",FACE,{"disambiguationData":[OSD([sQuery(id+"F9.wireOp",EDGE,"E15.0.4.6")])]})]});
            var Q33;
            Q33=makeQuery(id+"F10.boolean.opBoolean","INTERSECT",EDGE,{"disambiguationData":[OD(0.0)],"derivedFrom":[makeQuery(id+"F1.opExtrude","SWEPT_FACE",FACE,{"disambiguationData":[OSD([sQuery(id+"F0.wireOp",EDGE,"E0")])]}),makeQuery(id+"F10.opExtrude","SWEPT_FACE",FACE,{"disambiguationData":[OSD([sQuery(id+"F9.wireOp",EDGE,"E15.0.4.7")])]})]});
            var Q34;
            Q34=makeQuery(id+"F10.boolean.opBoolean","INTERSECT",EDGE,{"disambiguationData":[OD(0.0)],"derivedFrom":[makeQuery(id+"F1.opExtrude","SWEPT_FACE",FACE,{"disambiguationData":[OSD([sQuery(id+"F0.wireOp",EDGE,"E0")])]}),makeQuery(id+"F10.opExtrude","SWEPT_FACE",FACE,{"disambiguationData":[OSD([sQuery(id+"F9.wireOp",EDGE,"E15.0.4.5")])]})]});
            var Q35;
            Q35=makeQuery(id+"F10.boolean.opBoolean","INTERSECT",EDGE,{"disambiguationData":[OD(0.0)],"derivedFrom":[makeQuery(id+"F1.opExtrude","SWEPT_FACE",FACE,{"disambiguationData":[OSD([sQuery(id+"F0.wireOp",EDGE,"E0")])]}),makeQuery(id+"F10.opExtrude","SWEPT_FACE",FACE,{"disambiguationData":[OSD([sQuery(id+"F9.wireOp",EDGE,"E15.0.4.4")])]})]});
            var Q36;
            Q36=makeQuery(id+"F10.boolean.opBoolean","INTERSECT",EDGE,{"disambiguationData":[OD(0.0)],"derivedFrom":[makeQuery(id+"F1.opExtrude","SWEPT_FACE",FACE,{"disambiguationData":[OSD([sQuery(id+"F0.wireOp",EDGE,"E0")])]}),makeQuery(id+"F10.opExtrude","SWEPT_FACE",FACE,{"disambiguationData":[OSD([sQuery(id+"F9.wireOp",EDGE,"E15.0.5.3")])]})]});
            var Q37;
            Q37=makeQuery(id+"F10.boolean.opBoolean","INTERSECT",EDGE,{"disambiguationData":[OD(0.0)],"derivedFrom":[makeQuery(id+"F1.opExtrude","SWEPT_FACE",FACE,{"disambiguationData":[OSD([sQuery(id+"F0.wireOp",EDGE,"E0")])]}),makeQuery(id+"F10.opExtrude","SWEPT_FACE",FACE,{"disambiguationData":[OSD([sQuery(id+"F9.wireOp",EDGE,"E15.0.5.6")])]})]});
            var Q38;
            Q38=makeQuery(id+"F10.boolean.opBoolean","COPY",EDGE,{"disambiguationData":[OD(0.0)],"derivedFrom":makeQuery(id+"F10.opExtrude","SWEPT_EDGE",EDGE,{"disambiguationData":[OSD([sQuery(id+"F9.wireOp",EDGE,"E15.0.5.6"),sQuery(id+"F9.wireOp",EDGE,"E15.0.5.7")])]})});
            var Q39;
            Q39=makeQuery(id+"F10.boolean.opBoolean","INTERSECT",EDGE,{"disambiguationData":[OD(0.0)],"derivedFrom":[makeQuery(id+"F1.opExtrude","SWEPT_FACE",FACE,{"disambiguationData":[OSD([sQuery(id+"F0.wireOp",EDGE,"E0")])]}),makeQuery(id+"F10.opExtrude","SWEPT_FACE",FACE,{"disambiguationData":[OSD([sQuery(id+"F9.wireOp",EDGE,"E15.0.5.5")])]})]});
            var Q40;
            Q40=makeQuery(id+"F10.boolean.opBoolean","INTERSECT",EDGE,{"disambiguationData":[OD(0.0)],"derivedFrom":[makeQuery(id+"F1.opExtrude","SWEPT_FACE",FACE,{"disambiguationData":[OSD([sQuery(id+"F0.wireOp",EDGE,"E0")])]}),makeQuery(id+"F10.opExtrude","SWEPT_FACE",FACE,{"disambiguationData":[OSD([sQuery(id+"F9.wireOp",EDGE,"E15.0.5.4")])]})]});
            var Q41;
            Q41=makeQuery(id+"F10.boolean.opBoolean","INTERSECT",EDGE,{"disambiguationData":[OD(0.0)],"derivedFrom":[makeQuery(id+"F1.opExtrude","SWEPT_FACE",FACE,{"disambiguationData":[OSD([sQuery(id+"F0.wireOp",EDGE,"E0")])]}),makeQuery(id+"F10.opExtrude","SWEPT_FACE",FACE,{"disambiguationData":[OSD([sQuery(id+"F9.wireOp",EDGE,"E15.0.6.6")])]})]});
            var Q42;
            Q42=makeQuery(id+"F7.boolean.opBoolean","INTERSECT",EDGE,{"disambiguationData":[OD(0.0)],"derivedFrom":[makeQuery(id+"F1.opExtrude","SWEPT_FACE",FACE,{"disambiguationData":[OSD([sQuery(id+"F0.wireOp",EDGE,"E0")])]}),makeQuery(id+"F7.opExtrude","SWEPT_FACE",FACE,{"disambiguationData":[OSD([sQuery(id+"F6.wireOp",EDGE,"cfdfa16a-de7a-4601-9022-5211aa514822.4")])]})]});
            var Q43;
            Q43=makeQuery(id+"F7.boolean.opBoolean","INTERSECT",EDGE,{"disambiguationData":[OD(0.0)],"derivedFrom":[makeQuery(id+"F1.opExtrude","SWEPT_FACE",FACE,{"disambiguationData":[OSD([sQuery(id+"F0.wireOp",EDGE,"E0")])]}),makeQuery(id+"F7.opExtrude","SWEPT_FACE",FACE,{"disambiguationData":[OSD([sQuery(id+"F6.wireOp",EDGE,"09c30c40-169e-4e38-bf91-241d7524808d.5")])]})]});
            var Q44;
            Q44=makeQuery(id+"F10.boolean.opBoolean","INTERSECT",EDGE,{"disambiguationData":[OD(0.0)],"derivedFrom":[makeQuery(id+"F1.opExtrude","SWEPT_FACE",FACE,{"disambiguationData":[OSD([sQuery(id+"F0.wireOp",EDGE,"E0")])]}),makeQuery(id+"F10.opExtrude","SWEPT_FACE",FACE,{"disambiguationData":[OSD([sQuery(id+"F9.wireOp",EDGE,"E15.0.6.5")])]})]});
            var Q45;
            Q45=makeQuery(id+"F10.boolean.opBoolean","INTERSECT",EDGE,{"disambiguationData":[OD(0.0)],"derivedFrom":[makeQuery(id+"F1.opExtrude","SWEPT_FACE",FACE,{"disambiguationData":[OSD([sQuery(id+"F0.wireOp",EDGE,"E0")])]}),makeQuery(id+"F10.opExtrude","SWEPT_FACE",FACE,{"disambiguationData":[OSD([sQuery(id+"F9.wireOp",EDGE,"E15.0.6.7")])]})]});
            var Q46;
            Q46=makeQuery(id+"F10.boolean.opBoolean","INTERSECT",EDGE,{"disambiguationData":[OD(0.0)],"derivedFrom":[makeQuery(id+"F1.opExtrude","SWEPT_FACE",FACE,{"disambiguationData":[OSD([sQuery(id+"F0.wireOp",EDGE,"E0")])]}),makeQuery(id+"F10.opExtrude","SWEPT_FACE",FACE,{"disambiguationData":[OSD([sQuery(id+"F9.wireOp",EDGE,"E15.0.6.4")])]})]});
            var Q47;
            Q47=makeQuery(id+"F10.boolean.opBoolean","INTERSECT",EDGE,{"disambiguationData":[OD(0.0)],"derivedFrom":[makeQuery(id+"F1.opExtrude","SWEPT_FACE",FACE,{"disambiguationData":[OSD([sQuery(id+"F0.wireOp",EDGE,"E0")])]}),makeQuery(id+"F10.opExtrude","SWEPT_FACE",FACE,{"disambiguationData":[OSD([sQuery(id+"F9.wireOp",EDGE,"E15.0.6.3")])]})]});
            var Q48;
            Q48=makeQuery(id+"F10.boolean.opBoolean","INTERSECT",EDGE,{"disambiguationData":[OD(0.0)],"derivedFrom":[makeQuery(id+"F1.opExtrude","SWEPT_FACE",FACE,{"disambiguationData":[OSD([sQuery(id+"F0.wireOp",EDGE,"E0")])]}),makeQuery(id+"F10.opExtrude","SWEPT_FACE",FACE,{"disambiguationData":[OSD([sQuery(id+"F9.wireOp",EDGE,"E15.0.7.3")])]})]});
            var Q49;
            Q49=makeQuery(id+"F10.boolean.opBoolean","INTERSECT",EDGE,{"disambiguationData":[OD(0.0)],"derivedFrom":[makeQuery(id+"F1.opExtrude","SWEPT_FACE",FACE,{"disambiguationData":[OSD([sQuery(id+"F0.wireOp",EDGE,"E0")])]}),makeQuery(id+"F10.opExtrude","SWEPT_FACE",FACE,{"disambiguationData":[OSD([sQuery(id+"F9.wireOp",EDGE,"E15.0.7.6")])]})]});
            var Q50;
            Q50=makeQuery(id+"F10.boolean.opBoolean","INTERSECT",EDGE,{"disambiguationData":[OD(0.0)],"derivedFrom":[makeQuery(id+"F1.opExtrude","SWEPT_FACE",FACE,{"disambiguationData":[OSD([sQuery(id+"F0.wireOp",EDGE,"E0")])]}),makeQuery(id+"F10.opExtrude","SWEPT_FACE",FACE,{"disambiguationData":[OSD([sQuery(id+"F9.wireOp",EDGE,"E15.0.7.7")])]})]});
            var Q51;
            Q51=makeQuery(id+"F10.boolean.opBoolean","INTERSECT",EDGE,{"disambiguationData":[OD(0.0)],"derivedFrom":[makeQuery(id+"F1.opExtrude","SWEPT_FACE",FACE,{"disambiguationData":[OSD([sQuery(id+"F0.wireOp",EDGE,"E0")])]}),makeQuery(id+"F10.opExtrude","SWEPT_FACE",FACE,{"disambiguationData":[OSD([sQuery(id+"F9.wireOp",EDGE,"E15.0.7.5")])]})]});
            var Q52;
            Q52=makeQuery(id+"F10.boolean.opBoolean","INTERSECT",EDGE,{"disambiguationData":[OD(0.0)],"derivedFrom":[makeQuery(id+"F1.opExtrude","SWEPT_FACE",FACE,{"disambiguationData":[OSD([sQuery(id+"F0.wireOp",EDGE,"E0")])]}),makeQuery(id+"F10.opExtrude","SWEPT_FACE",FACE,{"disambiguationData":[OSD([sQuery(id+"F9.wireOp",EDGE,"E15.0.7.4")])]})]});
            var Q53;
            Q53=makeQuery(id+"F10.boolean.opBoolean","INTERSECT",EDGE,{"disambiguationData":[OD(0.0)],"derivedFrom":[makeQuery(id+"F1.opExtrude","SWEPT_FACE",FACE,{"disambiguationData":[OSD([sQuery(id+"F0.wireOp",EDGE,"E0")])]}),makeQuery(id+"F10.opExtrude","SWEPT_FACE",FACE,{"disambiguationData":[OSD([sQuery(id+"F9.wireOp",EDGE,"E15.0.8.2")])]})]});
            var Q54;
            Q54=makeQuery(id+"F10.boolean.opBoolean","INTERSECT",EDGE,{"disambiguationData":[OD(0.0)],"derivedFrom":[makeQuery(id+"F1.opExtrude","SWEPT_FACE",FACE,{"disambiguationData":[OSD([sQuery(id+"F0.wireOp",EDGE,"E0")])]}),makeQuery(id+"F10.opExtrude","SWEPT_FACE",FACE,{"disambiguationData":[OSD([sQuery(id+"F9.wireOp",EDGE,"E15.0.8.6")])]})]});
            var Q55;
            Q55=makeQuery(id+"F10.boolean.opBoolean","INTERSECT",EDGE,{"disambiguationData":[OD(0.0)],"derivedFrom":[makeQuery(id+"F1.opExtrude","SWEPT_FACE",FACE,{"disambiguationData":[OSD([sQuery(id+"F0.wireOp",EDGE,"E0")])]}),makeQuery(id+"F10.opExtrude","SWEPT_FACE",FACE,{"disambiguationData":[OSD([sQuery(id+"F9.wireOp",EDGE,"E15.0.8.7")])]})]});
            var Q56;
            Q56=makeQuery(id+"F10.boolean.opBoolean","INTERSECT",EDGE,{"disambiguationData":[OD(0.0)],"derivedFrom":[makeQuery(id+"F1.opExtrude","SWEPT_FACE",FACE,{"disambiguationData":[OSD([sQuery(id+"F0.wireOp",EDGE,"E0")])]}),makeQuery(id+"F10.opExtrude","SWEPT_FACE",FACE,{"disambiguationData":[OSD([sQuery(id+"F9.wireOp",EDGE,"E15.0.8.5")])]})]});
            var Q57;
            Q57=makeQuery(id+"F10.boolean.opBoolean","INTERSECT",EDGE,{"disambiguationData":[OD(0.0)],"derivedFrom":[makeQuery(id+"F1.opExtrude","SWEPT_FACE",FACE,{"disambiguationData":[OSD([sQuery(id+"F0.wireOp",EDGE,"E0")])]}),makeQuery(id+"F10.opExtrude","SWEPT_FACE",FACE,{"disambiguationData":[OSD([sQuery(id+"F9.wireOp",EDGE,"E15.0.8.4")])]})]});
            var Q58;
            Q58=makeQuery(id+"F10.boolean.opBoolean","INTERSECT",EDGE,{"disambiguationData":[OD(0.0)],"derivedFrom":[makeQuery(id+"F1.opExtrude","SWEPT_FACE",FACE,{"disambiguationData":[OSD([sQuery(id+"F0.wireOp",EDGE,"E0")])]}),makeQuery(id+"F10.opExtrude","SWEPT_FACE",FACE,{"disambiguationData":[OSD([sQuery(id+"F9.wireOp",EDGE,"E15.0.8.3")])]})]});
            var Q59;
            Q59=makeQuery(id+"F10.boolean.opBoolean","INTERSECT",EDGE,{"disambiguationData":[OD(0.0)],"derivedFrom":[makeQuery(id+"F1.opExtrude","SWEPT_FACE",FACE,{"disambiguationData":[OSD([sQuery(id+"F0.wireOp",EDGE,"E0")])]}),makeQuery(id+"F10.opExtrude","SWEPT_FACE",FACE,{"disambiguationData":[OSD([sQuery(id+"F9.wireOp",EDGE,"E15.0.9.6")])]})]});
            var Q60;
            Q60=makeQuery(id+"F10.boolean.opBoolean","INTERSECT",EDGE,{"disambiguationData":[OD(0.0)],"derivedFrom":[makeQuery(id+"F1.opExtrude","SWEPT_FACE",FACE,{"disambiguationData":[OSD([sQuery(id+"F0.wireOp",EDGE,"E0")])]}),makeQuery(id+"F10.opExtrude","SWEPT_FACE",FACE,{"disambiguationData":[OSD([sQuery(id+"F9.wireOp",EDGE,"E15.0.9.2")])]})]});
            var Q61;
            Q61=makeQuery(id+"F10.boolean.opBoolean","INTERSECT",EDGE,{"disambiguationData":[OD(0.0)],"derivedFrom":[makeQuery(id+"F1.opExtrude","SWEPT_FACE",FACE,{"disambiguationData":[OSD([sQuery(id+"F0.wireOp",EDGE,"E0")])]}),makeQuery(id+"F10.opExtrude","SWEPT_FACE",FACE,{"disambiguationData":[OSD([sQuery(id+"F9.wireOp",EDGE,"E15.0.9.3")])]})]});
            var Q62;
            Q62=makeQuery(id+"F10.boolean.opBoolean","INTERSECT",EDGE,{"disambiguationData":[OD(0.0)],"derivedFrom":[makeQuery(id+"F1.opExtrude","SWEPT_FACE",FACE,{"disambiguationData":[OSD([sQuery(id+"F0.wireOp",EDGE,"E0")])]}),makeQuery(id+"F10.opExtrude","SWEPT_FACE",FACE,{"disambiguationData":[OSD([sQuery(id+"F9.wireOp",EDGE,"E15.0.9.4")])]})]});
            var Q63;
            Q63=makeQuery(id+"F10.boolean.opBoolean","INTERSECT",EDGE,{"disambiguationData":[OD(0.0)],"derivedFrom":[makeQuery(id+"F1.opExtrude","SWEPT_FACE",FACE,{"disambiguationData":[OSD([sQuery(id+"F0.wireOp",EDGE,"E0")])]}),makeQuery(id+"F10.opExtrude","SWEPT_FACE",FACE,{"disambiguationData":[OSD([sQuery(id+"F9.wireOp",EDGE,"E15.0.9.5")])]})]});
            var Q64;
            Q64=makeQuery(id+"F10.boolean.opBoolean","INTERSECT",EDGE,{"disambiguationData":[OD(0.0)],"derivedFrom":[makeQuery(id+"F1.opExtrude","SWEPT_FACE",FACE,{"disambiguationData":[OSD([sQuery(id+"F0.wireOp",EDGE,"E0")])]}),makeQuery(id+"F10.opExtrude","SWEPT_FACE",FACE,{"disambiguationData":[OSD([sQuery(id+"F9.wireOp",EDGE,"E15.0.9.7")])]})]});
            var Q65;
            Q65=makeQuery(id+"F10.boolean.opBoolean","INTERSECT",EDGE,{"disambiguationData":[OD(0.0)],"derivedFrom":[makeQuery(id+"F1.opExtrude","SWEPT_FACE",FACE,{"disambiguationData":[OSD([sQuery(id+"F0.wireOp",EDGE,"E0")])]}),makeQuery(id+"F10.opExtrude","SWEPT_FACE",FACE,{"disambiguationData":[OSD([sQuery(id+"F9.wireOp",EDGE,"E15.0.10.6")])]})]});
            var Q66;
            Q66=makeQuery(id+"F10.boolean.opBoolean","INTERSECT",EDGE,{"disambiguationData":[OD(0.0)],"derivedFrom":[makeQuery(id+"F1.opExtrude","SWEPT_FACE",FACE,{"disambiguationData":[OSD([sQuery(id+"F0.wireOp",EDGE,"E0")])]}),makeQuery(id+"F10.opExtrude","SWEPT_FACE",FACE,{"disambiguationData":[OSD([sQuery(id+"F9.wireOp",EDGE,"E15.0.10.2")])]})]});
            var Q67;
            Q67=makeQuery(id+"F10.boolean.opBoolean","INTERSECT",EDGE,{"disambiguationData":[OD(0.0)],"derivedFrom":[makeQuery(id+"F1.opExtrude","SWEPT_FACE",FACE,{"disambiguationData":[OSD([sQuery(id+"F0.wireOp",EDGE,"E0")])]}),makeQuery(id+"F10.opExtrude","SWEPT_FACE",FACE,{"disambiguationData":[OSD([sQuery(id+"F9.wireOp",EDGE,"E15.0.10.3")])]})]});
            var Q68;
            Q68=makeQuery(id+"F10.boolean.opBoolean","INTERSECT",EDGE,{"disambiguationData":[OD(0.0)],"derivedFrom":[makeQuery(id+"F1.opExtrude","SWEPT_FACE",FACE,{"disambiguationData":[OSD([sQuery(id+"F0.wireOp",EDGE,"E0")])]}),makeQuery(id+"F10.opExtrude","SWEPT_FACE",FACE,{"disambiguationData":[OSD([sQuery(id+"F9.wireOp",EDGE,"E15.0.10.4")])]})]});
            var Q69;
            Q69=makeQuery(id+"F10.boolean.opBoolean","INTERSECT",EDGE,{"disambiguationData":[OD(0.0)],"derivedFrom":[makeQuery(id+"F1.opExtrude","SWEPT_FACE",FACE,{"disambiguationData":[OSD([sQuery(id+"F0.wireOp",EDGE,"E0")])]}),makeQuery(id+"F10.opExtrude","SWEPT_FACE",FACE,{"disambiguationData":[OSD([sQuery(id+"F9.wireOp",EDGE,"E15.0.10.5")])]})]});
            var Q70;
            Q70=makeQuery(id+"F10.boolean.opBoolean","COPY",EDGE,{"disambiguationData":[OD(0.0)],"derivedFrom":makeQuery(id+"F10.opExtrude","SWEPT_EDGE",EDGE,{"disambiguationData":[OSD([sQuery(id+"F9.wireOp",EDGE,"E15.0.10.6"),sQuery(id+"F9.wireOp",EDGE,"E15.0.10.7")])]})});
            var Q71;
            Q71=makeQuery(id+"F10.boolean.opBoolean","INTERSECT",EDGE,{"disambiguationData":[OD(0.0)],"derivedFrom":[makeQuery(id+"F1.opExtrude","SWEPT_FACE",FACE,{"disambiguationData":[OSD([sQuery(id+"F0.wireOp",EDGE,"E0")])]}),makeQuery(id+"F10.opExtrude","SWEPT_FACE",FACE,{"disambiguationData":[OSD([sQuery(id+"F9.wireOp",EDGE,"E15.0.11.6")])]})]});
            var Q72;
            Q72=makeQuery(id+"F10.boolean.opBoolean","INTERSECT",EDGE,{"disambiguationData":[OD(0.0)],"derivedFrom":[makeQuery(id+"F1.opExtrude","SWEPT_FACE",FACE,{"disambiguationData":[OSD([sQuery(id+"F0.wireOp",EDGE,"E0")])]}),makeQuery(id+"F10.opExtrude","SWEPT_FACE",FACE,{"disambiguationData":[OSD([sQuery(id+"F9.wireOp",EDGE,"E15.0.11.2")])]})]});
            var Q73;
            Q73=makeQuery(id+"F10.boolean.opBoolean","INTERSECT",EDGE,{"disambiguationData":[OD(0.0)],"derivedFrom":[makeQuery(id+"F1.opExtrude","SWEPT_FACE",FACE,{"disambiguationData":[OSD([sQuery(id+"F0.wireOp",EDGE,"E0")])]}),makeQuery(id+"F10.opExtrude","SWEPT_FACE",FACE,{"disambiguationData":[OSD([sQuery(id+"F9.wireOp",EDGE,"E15.0.11.3")])]})]});
            var Q74;
            Q74=makeQuery(id+"F10.boolean.opBoolean","INTERSECT",EDGE,{"disambiguationData":[OD(0.0)],"derivedFrom":[makeQuery(id+"F1.opExtrude","SWEPT_FACE",FACE,{"disambiguationData":[OSD([sQuery(id+"F0.wireOp",EDGE,"E0")])]}),makeQuery(id+"F10.opExtrude","SWEPT_FACE",FACE,{"disambiguationData":[OSD([sQuery(id+"F9.wireOp",EDGE,"E15.0.11.4")])]})]});
            var Q75;
            Q75=makeQuery(id+"F10.boolean.opBoolean","INTERSECT",EDGE,{"disambiguationData":[OD(0.0)],"derivedFrom":[makeQuery(id+"F1.opExtrude","SWEPT_FACE",FACE,{"disambiguationData":[OSD([sQuery(id+"F0.wireOp",EDGE,"E0")])]}),makeQuery(id+"F10.opExtrude","SWEPT_FACE",FACE,{"disambiguationData":[OSD([sQuery(id+"F9.wireOp",EDGE,"E15.0.11.5")])]})]});
            var Q76;
            Q76=makeQuery(id+"F10.boolean.opBoolean","INTERSECT",EDGE,{"disambiguationData":[OD(0.0)],"derivedFrom":[makeQuery(id+"F1.opExtrude","SWEPT_FACE",FACE,{"disambiguationData":[OSD([sQuery(id+"F0.wireOp",EDGE,"E0")])]}),makeQuery(id+"F10.opExtrude","SWEPT_FACE",FACE,{"disambiguationData":[OSD([sQuery(id+"F9.wireOp",EDGE,"E15.0.11.7")])]})]});
            var Q77;
            Q77=makeQuery(id+"F10.boolean.opBoolean","INTERSECT",EDGE,{"disambiguationData":[OD(0.0)],"derivedFrom":[makeQuery(id+"F1.opExtrude","SWEPT_FACE",FACE,{"disambiguationData":[OSD([sQuery(id+"F0.wireOp",EDGE,"E0")])]}),makeQuery(id+"F10.opExtrude","SWEPT_FACE",FACE,{"disambiguationData":[OSD([sQuery(id+"F9.wireOp",EDGE,"E15.0.12.6")])]})]});
            var Q78;
            Q78=makeQuery(id+"F10.boolean.opBoolean","INTERSECT",EDGE,{"disambiguationData":[OD(0.0)],"derivedFrom":[makeQuery(id+"F1.opExtrude","SWEPT_FACE",FACE,{"disambiguationData":[OSD([sQuery(id+"F0.wireOp",EDGE,"E0")])]}),makeQuery(id+"F10.opExtrude","SWEPT_FACE",FACE,{"disambiguationData":[OSD([sQuery(id+"F9.wireOp",EDGE,"E15.0.12.2")])]})]});
            var Q79;
            Q79=makeQuery(id+"F10.boolean.opBoolean","INTERSECT",EDGE,{"disambiguationData":[OD(0.0)],"derivedFrom":[makeQuery(id+"F1.opExtrude","SWEPT_FACE",FACE,{"disambiguationData":[OSD([sQuery(id+"F0.wireOp",EDGE,"E0")])]}),makeQuery(id+"F10.opExtrude","SWEPT_FACE",FACE,{"disambiguationData":[OSD([sQuery(id+"F9.wireOp",EDGE,"E15.0.12.3")])]})]});
            var Q80;
            Q80=makeQuery(id+"F10.boolean.opBoolean","INTERSECT",EDGE,{"disambiguationData":[OD(0.0)],"derivedFrom":[makeQuery(id+"F1.opExtrude","SWEPT_FACE",FACE,{"disambiguationData":[OSD([sQuery(id+"F0.wireOp",EDGE,"E0")])]}),makeQuery(id+"F10.opExtrude","SWEPT_FACE",FACE,{"disambiguationData":[OSD([sQuery(id+"F9.wireOp",EDGE,"E15.0.12.4")])]})]});
            var Q81;
            Q81=makeQuery(id+"F10.boolean.opBoolean","INTERSECT",EDGE,{"disambiguationData":[OD(0.0)],"derivedFrom":[makeQuery(id+"F1.opExtrude","SWEPT_FACE",FACE,{"disambiguationData":[OSD([sQuery(id+"F0.wireOp",EDGE,"E0")])]}),makeQuery(id+"F10.opExtrude","SWEPT_FACE",FACE,{"disambiguationData":[OSD([sQuery(id+"F9.wireOp",EDGE,"E15.0.12.5")])]})]});
            var Q82;
            Q82=makeQuery(id+"F10.boolean.opBoolean","INTERSECT",EDGE,{"disambiguationData":[OD(0.0)],"derivedFrom":[makeQuery(id+"F1.opExtrude","SWEPT_FACE",FACE,{"disambiguationData":[OSD([sQuery(id+"F0.wireOp",EDGE,"E0")])]}),makeQuery(id+"F10.opExtrude","SWEPT_FACE",FACE,{"disambiguationData":[OSD([sQuery(id+"F9.wireOp",EDGE,"E15.0.12.7")])]})]});
            var Q83;
            Q83=makeQuery(id+"F10.boolean.opBoolean","INTERSECT",EDGE,{"disambiguationData":[OD(0.0)],"derivedFrom":[makeQuery(id+"F1.opExtrude","SWEPT_FACE",FACE,{"disambiguationData":[OSD([sQuery(id+"F0.wireOp",EDGE,"E0")])]}),makeQuery(id+"F10.opExtrude","SWEPT_FACE",FACE,{"disambiguationData":[OSD([sQuery(id+"F9.wireOp",EDGE,"E21")])]})]});
            var Q84;
            Q84=makeQuery(id+"F10.boolean.opBoolean","INTERSECT",EDGE,{"disambiguationData":[OD(0.0)],"derivedFrom":[makeQuery(id+"F1.opExtrude","SWEPT_FACE",FACE,{"disambiguationData":[OSD([sQuery(id+"F0.wireOp",EDGE,"E0")])]}),makeQuery(id+"F10.opExtrude","SWEPT_FACE",FACE,{"disambiguationData":[OSD([sQuery(id+"F9.wireOp",EDGE,"E17.3")])]})]});
            var Q85;
            Q85=makeQuery(id+"F10.boolean.opBoolean","INTERSECT",EDGE,{"disambiguationData":[OD(0.0)],"derivedFrom":[makeQuery(id+"F1.opExtrude","SWEPT_FACE",FACE,{"disambiguationData":[OSD([sQuery(id+"F0.wireOp",EDGE,"E0")])]}),makeQuery(id+"F10.opExtrude","SWEPT_FACE",FACE,{"disambiguationData":[OSD([sQuery(id+"F9.wireOp",EDGE,"E22")])]})]});
            var Q86;
            Q86=makeQuery(id+"F10.boolean.opBoolean","INTERSECT",EDGE,{"disambiguationData":[OD(0.0)],"derivedFrom":[makeQuery(id+"F1.opExtrude","SWEPT_FACE",FACE,{"disambiguationData":[OSD([sQuery(id+"F0.wireOp",EDGE,"E0")])]}),makeQuery(id+"F10.opExtrude","SWEPT_FACE",FACE,{"disambiguationData":[OSD([sQuery(id+"F9.wireOp",EDGE,"E19"),sQuery(id+"F9.wireOp",EDGE,"E20")])]})]});
            var Q87;
            Q87=makeQuery(id+"F5.boolean.opBoolean","INTERSECT",EDGE,{"disambiguationData":[OD(0.0)],"derivedFrom":[makeQuery(id+"F1.opExtrude","SWEPT_FACE",FACE,{"disambiguationData":[OSD([sQuery(id+"F0.wireOp",EDGE,"E0")])]}),makeQuery(id+"F5.opExtrude","SWEPT_FACE",FACE,{"disambiguationData":[OSD([sQuery(id+"F4.wireOp",EDGE,"E4.3")])]})]});
            var Q88;
            Q88=makeQuery(id+"F5.boolean.opBoolean","INTERSECT",EDGE,{"disambiguationData":[OD(0.0)],"derivedFrom":[makeQuery(id+"F1.opExtrude","SWEPT_FACE",FACE,{"disambiguationData":[OSD([sQuery(id+"F0.wireOp",EDGE,"E0")])]}),makeQuery(id+"F5.opExtrude","SWEPT_FACE",FACE,{"disambiguationData":[OSD([sQuery(id+"F4.wireOp",EDGE,"E4.2")])]})]});
            var Q89;
            Q89=makeQuery(id+"F5.boolean.opBoolean","INTERSECT",EDGE,{"disambiguationData":[OD(0.0)],"derivedFrom":[makeQuery(id+"F1.opExtrude","SWEPT_FACE",FACE,{"disambiguationData":[OSD([sQuery(id+"F0.wireOp",EDGE,"E0")])]}),makeQuery(id+"F5.opExtrude","SWEPT_FACE",FACE,{"disambiguationData":[OSD([sQuery(id+"F4.wireOp",EDGE,"E4.1")])]})]});
            var Q90;
            Q90=makeQuery(id+"F5.boolean.opBoolean","INTERSECT",EDGE,{"disambiguationData":[OD(0.0)],"derivedFrom":[makeQuery(id+"F1.opExtrude","SWEPT_FACE",FACE,{"disambiguationData":[OSD([sQuery(id+"F0.wireOp",EDGE,"E0")])]}),makeQuery(id+"F5.opExtrude","SWEPT_FACE",FACE,{"disambiguationData":[OSD([sQuery(id+"F4.wireOp",EDGE,"E4.0")])]})]});
            var Q91;
            Q91=makeQuery(id+"F5.boolean.opBoolean","INTERSECT",EDGE,{"disambiguationData":[OD(0.0)],"derivedFrom":[makeQuery(id+"F1.opExtrude","SWEPT_FACE",FACE,{"disambiguationData":[OSD([sQuery(id+"F0.wireOp",EDGE,"E0")])]}),makeQuery(id+"F5.opExtrude","SWEPT_FACE",FACE,{"disambiguationData":[OSD([sQuery(id+"F4.wireOp",EDGE,"E4.5")])]})]});
            var Q92;
            Q92=makeQuery(id+"F5.boolean.opBoolean","INTERSECT",EDGE,{"disambiguationData":[OD(0.0)],"derivedFrom":[makeQuery(id+"F1.opExtrude","SWEPT_FACE",FACE,{"disambiguationData":[OSD([sQuery(id+"F0.wireOp",EDGE,"E0")])]}),makeQuery(id+"F5.opExtrude","SWEPT_FACE",FACE,{"disambiguationData":[OSD([sQuery(id+"F4.wireOp",EDGE,"E4.4")])]})]});
            var Q93;
            Q93=makeQuery(id+"F5.boolean.opBoolean","INTERSECT",EDGE,{"disambiguationData":[OD(0.0)],"derivedFrom":[makeQuery(id+"F1.opExtrude","SWEPT_FACE",FACE,{"disambiguationData":[OSD([sQuery(id+"F0.wireOp",EDGE,"E0")])]}),makeQuery(id+"F5.opExtrude","SWEPT_FACE",FACE,{"disambiguationData":[OSD([sQuery(id+"F4.wireOp",EDGE,"E5.0.1.1")])]})]});
            var Q94;
            Q94=makeQuery(id+"F5.boolean.opBoolean","INTERSECT",EDGE,{"disambiguationData":[OD(0.0)],"derivedFrom":[makeQuery(id+"F1.opExtrude","SWEPT_FACE",FACE,{"disambiguationData":[OSD([sQuery(id+"F0.wireOp",EDGE,"E0")])]}),makeQuery(id+"F5.opExtrude","SWEPT_FACE",FACE,{"disambiguationData":[OSD([sQuery(id+"F4.wireOp",EDGE,"E5.0.1.2")])]})]});
            var Q95;
            Q95=makeQuery(id+"F5.boolean.opBoolean","INTERSECT",EDGE,{"disambiguationData":[OD(0.0)],"derivedFrom":[makeQuery(id+"F1.opExtrude","SWEPT_FACE",FACE,{"disambiguationData":[OSD([sQuery(id+"F0.wireOp",EDGE,"E0")])]}),makeQuery(id+"F5.opExtrude","SWEPT_FACE",FACE,{"disambiguationData":[OSD([sQuery(id+"F4.wireOp",EDGE,"E5.0.1.3")])]})]});
            var Q96;
            Q96=makeQuery(id+"F5.boolean.opBoolean","INTERSECT",EDGE,{"disambiguationData":[OD(0.0)],"derivedFrom":[makeQuery(id+"F1.opExtrude","SWEPT_FACE",FACE,{"disambiguationData":[OSD([sQuery(id+"F0.wireOp",EDGE,"E0")])]}),makeQuery(id+"F5.opExtrude","SWEPT_FACE",FACE,{"disambiguationData":[OSD([sQuery(id+"F4.wireOp",EDGE,"E5.0.1.4")])]})]});
            var Q97;
            Q97=makeQuery(id+"F5.boolean.opBoolean","INTERSECT",EDGE,{"disambiguationData":[OD(0.0)],"derivedFrom":[makeQuery(id+"F1.opExtrude","SWEPT_FACE",FACE,{"disambiguationData":[OSD([sQuery(id+"F0.wireOp",EDGE,"E0")])]}),makeQuery(id+"F5.opExtrude","SWEPT_FACE",FACE,{"disambiguationData":[OSD([sQuery(id+"F4.wireOp",EDGE,"E5.0.1.0")])]})]});
            var Q98;
            Q98=makeQuery(id+"F5.boolean.opBoolean","INTERSECT",EDGE,{"disambiguationData":[OD(0.0)],"derivedFrom":[makeQuery(id+"F1.opExtrude","SWEPT_FACE",FACE,{"disambiguationData":[OSD([sQuery(id+"F0.wireOp",EDGE,"E0")])]}),makeQuery(id+"F5.opExtrude","SWEPT_FACE",FACE,{"disambiguationData":[OSD([sQuery(id+"F4.wireOp",EDGE,"E5.0.1.7")])]})]});
            var Q99;
            Q99=makeQuery(id+"F5.boolean.opBoolean","INTERSECT",EDGE,{"disambiguationData":[OD(0.0)],"derivedFrom":[makeQuery(id+"F1.opExtrude","SWEPT_FACE",FACE,{"disambiguationData":[OSD([sQuery(id+"F0.wireOp",EDGE,"E0")])]}),makeQuery(id+"F5.opExtrude","SWEPT_FACE",FACE,{"disambiguationData":[OSD([sQuery(id+"F4.wireOp",EDGE,"E5.0.2.1")])]})]});
            var Q100;
            Q100=makeQuery(id+"F5.boolean.opBoolean","INTERSECT",EDGE,{"disambiguationData":[OD(0.0)],"derivedFrom":[makeQuery(id+"F1.opExtrude","SWEPT_FACE",FACE,{"disambiguationData":[OSD([sQuery(id+"F0.wireOp",EDGE,"E0")])]}),makeQuery(id+"F5.opExtrude","SWEPT_FACE",FACE,{"disambiguationData":[OSD([sQuery(id+"F4.wireOp",EDGE,"E5.0.2.2")])]})]});
            var Q101;
            Q101=makeQuery(id+"F5.boolean.opBoolean","INTERSECT",EDGE,{"disambiguationData":[OD(0.0)],"derivedFrom":[makeQuery(id+"F1.opExtrude","SWEPT_FACE",FACE,{"disambiguationData":[OSD([sQuery(id+"F0.wireOp",EDGE,"E0")])]}),makeQuery(id+"F5.opExtrude","SWEPT_FACE",FACE,{"disambiguationData":[OSD([sQuery(id+"F4.wireOp",EDGE,"E5.0.2.3")])]})]});
            var Q102;
            Q102=makeQuery(id+"F5.boolean.opBoolean","INTERSECT",EDGE,{"disambiguationData":[OD(0.0)],"derivedFrom":[makeQuery(id+"F1.opExtrude","SWEPT_FACE",FACE,{"disambiguationData":[OSD([sQuery(id+"F0.wireOp",EDGE,"E0")])]}),makeQuery(id+"F5.opExtrude","SWEPT_FACE",FACE,{"disambiguationData":[OSD([sQuery(id+"F4.wireOp",EDGE,"E5.0.2.4")])]})]});
            var Q103;
            Q103=makeQuery(id+"F5.boolean.opBoolean","INTERSECT",EDGE,{"disambiguationData":[OD(0.0)],"derivedFrom":[makeQuery(id+"F1.opExtrude","SWEPT_FACE",FACE,{"disambiguationData":[OSD([sQuery(id+"F0.wireOp",EDGE,"E0")])]}),makeQuery(id+"F5.opExtrude","SWEPT_FACE",FACE,{"disambiguationData":[OSD([sQuery(id+"F4.wireOp",EDGE,"E5.0.2.0")])]})]});
            var Q104;
            Q104=makeQuery(id+"F5.boolean.opBoolean","INTERSECT",EDGE,{"disambiguationData":[OD(0.0)],"derivedFrom":[makeQuery(id+"F1.opExtrude","SWEPT_FACE",FACE,{"disambiguationData":[OSD([sQuery(id+"F0.wireOp",EDGE,"E0")])]}),makeQuery(id+"F5.opExtrude","SWEPT_FACE",FACE,{"disambiguationData":[OSD([sQuery(id+"F4.wireOp",EDGE,"E5.0.2.7")])]})]});
            var Q105;
            Q105=makeQuery(id+"F5.boolean.opBoolean","INTERSECT",EDGE,{"disambiguationData":[OD(0.0)],"derivedFrom":[makeQuery(id+"F1.opExtrude","SWEPT_FACE",FACE,{"disambiguationData":[OSD([sQuery(id+"F0.wireOp",EDGE,"E0")])]}),makeQuery(id+"F5.opExtrude","SWEPT_FACE",FACE,{"disambiguationData":[OSD([sQuery(id+"F4.wireOp",EDGE,"E5.0.3.1")])]})]});
            var Q106;
            Q106=makeQuery(id+"F5.boolean.opBoolean","INTERSECT",EDGE,{"disambiguationData":[OD(0.0)],"derivedFrom":[makeQuery(id+"F1.opExtrude","SWEPT_FACE",FACE,{"disambiguationData":[OSD([sQuery(id+"F0.wireOp",EDGE,"E0")])]}),makeQuery(id+"F5.opExtrude","SWEPT_FACE",FACE,{"disambiguationData":[OSD([sQuery(id+"F4.wireOp",EDGE,"E5.0.3.2")])]})]});
            var Q107;
            Q107=makeQuery(id+"F5.boolean.opBoolean","INTERSECT",EDGE,{"disambiguationData":[OD(0.0)],"derivedFrom":[makeQuery(id+"F1.opExtrude","SWEPT_FACE",FACE,{"disambiguationData":[OSD([sQuery(id+"F0.wireOp",EDGE,"E0")])]}),makeQuery(id+"F5.opExtrude","SWEPT_FACE",FACE,{"disambiguationData":[OSD([sQuery(id+"F4.wireOp",EDGE,"E5.0.3.3")])]})]});
            var Q108;
            Q108=makeQuery(id+"F5.boolean.opBoolean","INTERSECT",EDGE,{"disambiguationData":[OD(0.0)],"derivedFrom":[makeQuery(id+"F1.opExtrude","SWEPT_FACE",FACE,{"disambiguationData":[OSD([sQuery(id+"F0.wireOp",EDGE,"E0")])]}),makeQuery(id+"F5.opExtrude","SWEPT_FACE",FACE,{"disambiguationData":[OSD([sQuery(id+"F4.wireOp",EDGE,"E5.0.3.4")])]})]});
            var Q109;
            Q109=makeQuery(id+"F5.boolean.opBoolean","INTERSECT",EDGE,{"disambiguationData":[OD(0.0)],"derivedFrom":[makeQuery(id+"F1.opExtrude","SWEPT_FACE",FACE,{"disambiguationData":[OSD([sQuery(id+"F0.wireOp",EDGE,"E0")])]}),makeQuery(id+"F5.opExtrude","SWEPT_FACE",FACE,{"disambiguationData":[OSD([sQuery(id+"F4.wireOp",EDGE,"E5.0.3.0")])]})]});
            var Q110;
            Q110=makeQuery(id+"F5.boolean.opBoolean","INTERSECT",EDGE,{"disambiguationData":[OD(0.0)],"derivedFrom":[makeQuery(id+"F1.opExtrude","SWEPT_FACE",FACE,{"disambiguationData":[OSD([sQuery(id+"F0.wireOp",EDGE,"E0")])]}),makeQuery(id+"F5.opExtrude","SWEPT_FACE",FACE,{"disambiguationData":[OSD([sQuery(id+"F4.wireOp",EDGE,"E5.0.3.7")])]})]});
            var Q111;
            Q111=makeQuery(id+"F7.boolean.opBoolean","INTERSECT",EDGE,{"disambiguationData":[OD(0.0)],"derivedFrom":[makeQuery(id+"F1.opExtrude","SWEPT_FACE",FACE,{"disambiguationData":[OSD([sQuery(id+"F0.wireOp",EDGE,"E0")])]}),makeQuery(id+"F7.opExtrude","SWEPT_FACE",FACE,{"disambiguationData":[OSD([sQuery(id+"F6.wireOp",EDGE,"cfdfa16a-de7a-4601-9022-5211aa514822.1")])]})]});
            var Q112;
            Q112=makeQuery(id+"F7.boolean.opBoolean","INTERSECT",EDGE,{"disambiguationData":[OD(0.0)],"derivedFrom":[makeQuery(id+"F1.opExtrude","SWEPT_FACE",FACE,{"disambiguationData":[OSD([sQuery(id+"F0.wireOp",EDGE,"E0")])]}),makeQuery(id+"F7.opExtrude","SWEPT_FACE",FACE,{"disambiguationData":[OSD([sQuery(id+"F6.wireOp",EDGE,"cfdfa16a-de7a-4601-9022-5211aa514822.2")])]})]});
            var Q113;
            Q113=makeQuery(id+"F7.boolean.opBoolean","INTERSECT",EDGE,{"disambiguationData":[OD(0.0)],"derivedFrom":[makeQuery(id+"F1.opExtrude","SWEPT_FACE",FACE,{"disambiguationData":[OSD([sQuery(id+"F0.wireOp",EDGE,"E0")])]}),makeQuery(id+"F7.opExtrude","SWEPT_FACE",FACE,{"disambiguationData":[OSD([sQuery(id+"F6.wireOp",EDGE,"cfdfa16a-de7a-4601-9022-5211aa514822.3")])]})]});
            var Q114;
            Q114=makeQuery(id+"F7.boolean.opBoolean","INTERSECT",EDGE,{"disambiguationData":[OD(0.0)],"derivedFrom":[makeQuery(id+"F1.opExtrude","SWEPT_FACE",FACE,{"disambiguationData":[OSD([sQuery(id+"F0.wireOp",EDGE,"E0")])]}),makeQuery(id+"F7.opExtrude","SWEPT_FACE",FACE,{"disambiguationData":[OSD([sQuery(id+"F6.wireOp",EDGE,"cfdfa16a-de7a-4601-9022-5211aa514822.5")])]})]});
            var Q115;
            Q115=makeQuery(id+"F7.boolean.opBoolean","INTERSECT",EDGE,{"disambiguationData":[OD(0.0)],"derivedFrom":[makeQuery(id+"F1.opExtrude","SWEPT_FACE",FACE,{"disambiguationData":[OSD([sQuery(id+"F0.wireOp",EDGE,"E0")])]}),makeQuery(id+"F7.opExtrude","SWEPT_FACE",FACE,{"disambiguationData":[OSD([sQuery(id+"F6.wireOp",EDGE,"cfdfa16a-de7a-4601-9022-5211aa514822.0")])]})]});
            var Q116;
            Q116=makeQuery(id+"F7.boolean.opBoolean","INTERSECT",EDGE,{"disambiguationData":[OD(0.0)],"derivedFrom":[makeQuery(id+"F1.opExtrude","SWEPT_FACE",FACE,{"disambiguationData":[OSD([sQuery(id+"F0.wireOp",EDGE,"E0")])]}),makeQuery(id+"F7.opExtrude","SWEPT_FACE",FACE,{"disambiguationData":[OSD([sQuery(id+"F6.wireOp",EDGE,"6fecd9f8-48d6-48ad-88a1-144c9b17d822.3")])]})]});
            var Q117;
            Q117=makeQuery(id+"F7.boolean.opBoolean","INTERSECT",EDGE,{"disambiguationData":[OD(0.0)],"derivedFrom":[makeQuery(id+"F1.opExtrude","SWEPT_FACE",FACE,{"disambiguationData":[OSD([sQuery(id+"F0.wireOp",EDGE,"E0")])]}),makeQuery(id+"F7.opExtrude","SWEPT_FACE",FACE,{"disambiguationData":[OSD([sQuery(id+"F6.wireOp",EDGE,"6fecd9f8-48d6-48ad-88a1-144c9b17d822.2")])]})]});
            var Q118;
            Q118=makeQuery(id+"F7.boolean.opBoolean","INTERSECT",EDGE,{"disambiguationData":[OD(0.0)],"derivedFrom":[makeQuery(id+"F1.opExtrude","SWEPT_FACE",FACE,{"disambiguationData":[OSD([sQuery(id+"F0.wireOp",EDGE,"E0")])]}),makeQuery(id+"F7.opExtrude","SWEPT_FACE",FACE,{"disambiguationData":[OSD([sQuery(id+"F6.wireOp",EDGE,"6fecd9f8-48d6-48ad-88a1-144c9b17d822.1")])]})]});
            var Q119;
            Q119=makeQuery(id+"F7.boolean.opBoolean","INTERSECT",EDGE,{"disambiguationData":[OD(0.0)],"derivedFrom":[makeQuery(id+"F1.opExtrude","SWEPT_FACE",FACE,{"disambiguationData":[OSD([sQuery(id+"F0.wireOp",EDGE,"E0")])]}),makeQuery(id+"F7.opExtrude","SWEPT_FACE",FACE,{"disambiguationData":[OSD([sQuery(id+"F6.wireOp",EDGE,"6fecd9f8-48d6-48ad-88a1-144c9b17d822.0")])]})]});
            var Q120;
            Q120=makeQuery(id+"F7.boolean.opBoolean","INTERSECT",EDGE,{"disambiguationData":[OD(0.0)],"derivedFrom":[makeQuery(id+"F1.opExtrude","SWEPT_FACE",FACE,{"disambiguationData":[OSD([sQuery(id+"F0.wireOp",EDGE,"E0")])]}),makeQuery(id+"F7.opExtrude","SWEPT_FACE",FACE,{"disambiguationData":[OSD([sQuery(id+"F6.wireOp",EDGE,"6fecd9f8-48d6-48ad-88a1-144c9b17d822.5")])]})]});
            var Q121;
            Q121=makeQuery(id+"F7.boolean.opBoolean","INTERSECT",EDGE,{"disambiguationData":[OD(0.0)],"derivedFrom":[makeQuery(id+"F1.opExtrude","SWEPT_FACE",FACE,{"disambiguationData":[OSD([sQuery(id+"F0.wireOp",EDGE,"E0")])]}),makeQuery(id+"F7.opExtrude","SWEPT_FACE",FACE,{"disambiguationData":[OSD([sQuery(id+"F6.wireOp",EDGE,"6fecd9f8-48d6-48ad-88a1-144c9b17d822.4")])]})]});
            fillet(context, id + "F15", {"entities" : qUnion([Q0, Q1, Q2, Q3, Q4, Q5, Q6, Q7, Q8, Q9, Q10, Q11, Q12, Q13, Q14, Q15, Q16, Q17, Q18, Q19, Q20, Q21, Q22, Q23, Q24, Q25, Q26, Q27, Q28, Q29, Q30, Q31, Q32, Q33, Q34, Q35, Q36, Q37, Q38, Q39, Q40, Q41, Q42, Q43, Q44, Q45, Q46, Q47, Q48, Q49, Q50, Q51, Q52, Q53, Q54, Q55, Q56, Q57, Q58, Q59, Q60, Q61, Q62, Q63, Q64, Q65, Q66, Q67, Q68, Q69, Q70, Q71, Q72, Q73, Q74, Q75, Q76, Q77, Q78, Q79, Q80, Q81, Q82, Q83, Q84, Q85, Q86, Q87, Q88, Q89, Q90, Q91, Q92, Q93, Q94, Q95, Q96, Q97, Q98, Q99, Q100, Q101, Q102, Q103, Q104, Q105, Q106, Q107, Q108, Q109, Q110, Q111, Q112, Q113, Q114, Q115, Q116, Q117, Q118, Q119, Q120, Q121]), "radius" : 0.7 * mm, "tangentPropagation" : true, "defaultsChanged" : true, "vertexSettings" : [], "allowEdgeOverflow" : false});
        }
        {
            var Q0;
            Q0=makeQuery(id+"F7.boolean.opBoolean","INTERSECT",EDGE,{"disambiguationData":[OD(0.0)],"derivedFrom":[makeQuery(id+"F1.opExtrude","SWEPT_FACE",FACE,{"disambiguationData":[OSD([sQuery(id+"F0.wireOp",EDGE,"E0")])]}),makeQuery(id+"F7.opExtrude","SWEPT_FACE",FACE,{"disambiguationData":[OSD([sQuery(id+"F6.wireOp",EDGE,"57ad66dd-c389-404c-b97b-3d1c940e2ac9.0")])]})]});
            var Q1;
            Q1=makeQuery(id+"F7.boolean.opBoolean","INTERSECT",EDGE,{"disambiguationData":[OD(0.0)],"derivedFrom":[makeQuery(id+"F1.opExtrude","SWEPT_FACE",FACE,{"disambiguationData":[OSD([sQuery(id+"F0.wireOp",EDGE,"E0")])]}),makeQuery(id+"F7.opExtrude","SWEPT_FACE",FACE,{"disambiguationData":[OSD([sQuery(id+"F6.wireOp",EDGE,"57ad66dd-c389-404c-b97b-3d1c940e2ac9.5")])]})]});
            var Q2;
            Q2=makeQuery(id+"F7.boolean.opBoolean","INTERSECT",EDGE,{"disambiguationData":[OD(0.0)],"derivedFrom":[makeQuery(id+"F1.opExtrude","SWEPT_FACE",FACE,{"disambiguationData":[OSD([sQuery(id+"F0.wireOp",EDGE,"E0")])]}),makeQuery(id+"F7.opExtrude","SWEPT_FACE",FACE,{"disambiguationData":[OSD([sQuery(id+"F6.wireOp",EDGE,"57ad66dd-c389-404c-b97b-3d1c940e2ac9.4")])]})]});
            var Q3;
            Q3=makeQuery(id+"F7.boolean.opBoolean","INTERSECT",EDGE,{"disambiguationData":[OD(0.0)],"derivedFrom":[makeQuery(id+"F1.opExtrude","SWEPT_FACE",FACE,{"disambiguationData":[OSD([sQuery(id+"F0.wireOp",EDGE,"E0")])]}),makeQuery(id+"F7.opExtrude","SWEPT_FACE",FACE,{"disambiguationData":[OSD([sQuery(id+"F6.wireOp",EDGE,"57ad66dd-c389-404c-b97b-3d1c940e2ac9.3")])]})]});
            var Q4;
            Q4=makeQuery(id+"F7.boolean.opBoolean","INTERSECT",EDGE,{"disambiguationData":[OD(0.0)],"derivedFrom":[makeQuery(id+"F1.opExtrude","SWEPT_FACE",FACE,{"disambiguationData":[OSD([sQuery(id+"F0.wireOp",EDGE,"E0")])]}),makeQuery(id+"F7.opExtrude","SWEPT_FACE",FACE,{"disambiguationData":[OSD([sQuery(id+"F6.wireOp",EDGE,"57ad66dd-c389-404c-b97b-3d1c940e2ac9.2")])]})]});
            var Q5;
            Q5=makeQuery(id+"F7.boolean.opBoolean","INTERSECT",EDGE,{"disambiguationData":[OD(0.0)],"derivedFrom":[makeQuery(id+"F1.opExtrude","SWEPT_FACE",FACE,{"disambiguationData":[OSD([sQuery(id+"F0.wireOp",EDGE,"E0")])]}),makeQuery(id+"F7.opExtrude","SWEPT_FACE",FACE,{"disambiguationData":[OSD([sQuery(id+"F6.wireOp",EDGE,"57ad66dd-c389-404c-b97b-3d1c940e2ac9.1")])]})]});
            var Q6;
            Q6=makeQuery(id+"F7.boolean.opBoolean","INTERSECT",EDGE,{"disambiguationData":[OD(0.0)],"derivedFrom":[makeQuery(id+"F1.opExtrude","SWEPT_FACE",FACE,{"disambiguationData":[OSD([sQuery(id+"F0.wireOp",EDGE,"E0")])]}),makeQuery(id+"F7.opExtrude","SWEPT_FACE",FACE,{"disambiguationData":[OSD([sQuery(id+"F6.wireOp",EDGE,"b8bbc581-4b7c-4f09-85fb-0bc221e83278.2")])]})]});
            var Q7;
            Q7=makeQuery(id+"F7.boolean.opBoolean","INTERSECT",EDGE,{"disambiguationData":[OD(0.0)],"derivedFrom":[makeQuery(id+"F1.opExtrude","SWEPT_FACE",FACE,{"disambiguationData":[OSD([sQuery(id+"F0.wireOp",EDGE,"E0")])]}),makeQuery(id+"F7.opExtrude","SWEPT_FACE",FACE,{"disambiguationData":[OSD([sQuery(id+"F6.wireOp",EDGE,"b8bbc581-4b7c-4f09-85fb-0bc221e83278.1")])]})]});
            var Q8;
            Q8=makeQuery(id+"F7.boolean.opBoolean","INTERSECT",EDGE,{"disambiguationData":[OD(0.0)],"derivedFrom":[makeQuery(id+"F1.opExtrude","SWEPT_FACE",FACE,{"disambiguationData":[OSD([sQuery(id+"F0.wireOp",EDGE,"E0")])]}),makeQuery(id+"F7.opExtrude","SWEPT_FACE",FACE,{"disambiguationData":[OSD([sQuery(id+"F6.wireOp",EDGE,"b8bbc581-4b7c-4f09-85fb-0bc221e83278.0")])]})]});
            var Q9;
            Q9=makeQuery(id+"F7.boolean.opBoolean","INTERSECT",EDGE,{"disambiguationData":[OD(0.0)],"derivedFrom":[makeQuery(id+"F1.opExtrude","SWEPT_FACE",FACE,{"disambiguationData":[OSD([sQuery(id+"F0.wireOp",EDGE,"E0")])]}),makeQuery(id+"F7.opExtrude","SWEPT_FACE",FACE,{"disambiguationData":[OSD([sQuery(id+"F6.wireOp",EDGE,"b8bbc581-4b7c-4f09-85fb-0bc221e83278.5")])]})]});
            var Q10;
            Q10=makeQuery(id+"F7.boolean.opBoolean","INTERSECT",EDGE,{"disambiguationData":[OD(0.0)],"derivedFrom":[makeQuery(id+"F1.opExtrude","SWEPT_FACE",FACE,{"disambiguationData":[OSD([sQuery(id+"F0.wireOp",EDGE,"E0")])]}),makeQuery(id+"F7.opExtrude","SWEPT_FACE",FACE,{"disambiguationData":[OSD([sQuery(id+"F6.wireOp",EDGE,"b8bbc581-4b7c-4f09-85fb-0bc221e83278.4")])]})]});
            var Q11;
            Q11=makeQuery(id+"F7.boolean.opBoolean","INTERSECT",EDGE,{"disambiguationData":[OD(0.0)],"derivedFrom":[makeQuery(id+"F1.opExtrude","SWEPT_FACE",FACE,{"disambiguationData":[OSD([sQuery(id+"F0.wireOp",EDGE,"E0")])]}),makeQuery(id+"F7.opExtrude","SWEPT_FACE",FACE,{"disambiguationData":[OSD([sQuery(id+"F6.wireOp",EDGE,"b8bbc581-4b7c-4f09-85fb-0bc221e83278.3")])]})]});
            var Q12;
            Q12=makeQuery(id+"F7.boolean.opBoolean","INTERSECT",EDGE,{"disambiguationData":[OD(0.0)],"derivedFrom":[makeQuery(id+"F1.opExtrude","SWEPT_FACE",FACE,{"disambiguationData":[OSD([sQuery(id+"F0.wireOp",EDGE,"E0")])]}),makeQuery(id+"F7.opExtrude","SWEPT_FACE",FACE,{"disambiguationData":[OSD([sQuery(id+"F6.wireOp",EDGE,"3989a008-e829-4c74-847c-c0cff927c4a6.0")])]})]});
            var Q13;
            Q13=makeQuery(id+"F7.boolean.opBoolean","INTERSECT",EDGE,{"disambiguationData":[OD(0.0)],"derivedFrom":[makeQuery(id+"F1.opExtrude","SWEPT_FACE",FACE,{"disambiguationData":[OSD([sQuery(id+"F0.wireOp",EDGE,"E0")])]}),makeQuery(id+"F7.opExtrude","SWEPT_FACE",FACE,{"disambiguationData":[OSD([sQuery(id+"F6.wireOp",EDGE,"3989a008-e829-4c74-847c-c0cff927c4a6.5")])]})]});
            var Q14;
            Q14=makeQuery(id+"F7.boolean.opBoolean","INTERSECT",EDGE,{"disambiguationData":[OD(0.0)],"derivedFrom":[makeQuery(id+"F1.opExtrude","SWEPT_FACE",FACE,{"disambiguationData":[OSD([sQuery(id+"F0.wireOp",EDGE,"E0")])]}),makeQuery(id+"F7.opExtrude","SWEPT_FACE",FACE,{"disambiguationData":[OSD([sQuery(id+"F6.wireOp",EDGE,"3989a008-e829-4c74-847c-c0cff927c4a6.4")])]})]});
            var Q15;
            Q15=makeQuery(id+"F7.boolean.opBoolean","INTERSECT",EDGE,{"disambiguationData":[OD(0.0)],"derivedFrom":[makeQuery(id+"F1.opExtrude","SWEPT_FACE",FACE,{"disambiguationData":[OSD([sQuery(id+"F0.wireOp",EDGE,"E0")])]}),makeQuery(id+"F7.opExtrude","SWEPT_FACE",FACE,{"disambiguationData":[OSD([sQuery(id+"F6.wireOp",EDGE,"3989a008-e829-4c74-847c-c0cff927c4a6.3")])]})]});
            var Q16;
            Q16=makeQuery(id+"F7.boolean.opBoolean","INTERSECT",EDGE,{"disambiguationData":[OD(0.0)],"derivedFrom":[makeQuery(id+"F1.opExtrude","SWEPT_FACE",FACE,{"disambiguationData":[OSD([sQuery(id+"F0.wireOp",EDGE,"E0")])]}),makeQuery(id+"F7.opExtrude","SWEPT_FACE",FACE,{"disambiguationData":[OSD([sQuery(id+"F6.wireOp",EDGE,"3989a008-e829-4c74-847c-c0cff927c4a6.2")])]})]});
            var Q17;
            Q17=makeQuery(id+"F7.boolean.opBoolean","INTERSECT",EDGE,{"disambiguationData":[OD(0.0)],"derivedFrom":[makeQuery(id+"F1.opExtrude","SWEPT_FACE",FACE,{"disambiguationData":[OSD([sQuery(id+"F0.wireOp",EDGE,"E0")])]}),makeQuery(id+"F7.opExtrude","SWEPT_FACE",FACE,{"disambiguationData":[OSD([sQuery(id+"F6.wireOp",EDGE,"3989a008-e829-4c74-847c-c0cff927c4a6.1")])]})]});
            var Q18;
            Q18=makeQuery(id+"F7.boolean.opBoolean","INTERSECT",EDGE,{"disambiguationData":[OD(0.0)],"derivedFrom":[makeQuery(id+"F1.opExtrude","SWEPT_FACE",FACE,{"disambiguationData":[OSD([sQuery(id+"F0.wireOp",EDGE,"E0")])]}),makeQuery(id+"F7.opExtrude","SWEPT_FACE",FACE,{"disambiguationData":[OSD([sQuery(id+"F6.wireOp",EDGE,"86e64e75-ce93-4209-b98e-9b8fc518f516.2")])]})]});
            var Q19;
            Q19=makeQuery(id+"F7.boolean.opBoolean","INTERSECT",EDGE,{"disambiguationData":[OD(0.0)],"derivedFrom":[makeQuery(id+"F1.opExtrude","SWEPT_FACE",FACE,{"disambiguationData":[OSD([sQuery(id+"F0.wireOp",EDGE,"E0")])]}),makeQuery(id+"F7.opExtrude","SWEPT_FACE",FACE,{"disambiguationData":[OSD([sQuery(id+"F6.wireOp",EDGE,"86e64e75-ce93-4209-b98e-9b8fc518f516.1")])]})]});
            var Q20;
            Q20=makeQuery(id+"F7.boolean.opBoolean","INTERSECT",EDGE,{"disambiguationData":[OD(0.0)],"derivedFrom":[makeQuery(id+"F1.opExtrude","SWEPT_FACE",FACE,{"disambiguationData":[OSD([sQuery(id+"F0.wireOp",EDGE,"E0")])]}),makeQuery(id+"F7.opExtrude","SWEPT_FACE",FACE,{"disambiguationData":[OSD([sQuery(id+"F6.wireOp",EDGE,"86e64e75-ce93-4209-b98e-9b8fc518f516.0")])]})]});
            var Q21;
            Q21=makeQuery(id+"F7.boolean.opBoolean","INTERSECT",EDGE,{"disambiguationData":[OD(0.0)],"derivedFrom":[makeQuery(id+"F1.opExtrude","SWEPT_FACE",FACE,{"disambiguationData":[OSD([sQuery(id+"F0.wireOp",EDGE,"E0")])]}),makeQuery(id+"F7.opExtrude","SWEPT_FACE",FACE,{"disambiguationData":[OSD([sQuery(id+"F6.wireOp",EDGE,"86e64e75-ce93-4209-b98e-9b8fc518f516.5")])]})]});
            var Q22;
            Q22=makeQuery(id+"F7.boolean.opBoolean","INTERSECT",EDGE,{"disambiguationData":[OD(0.0)],"derivedFrom":[makeQuery(id+"F1.opExtrude","SWEPT_FACE",FACE,{"disambiguationData":[OSD([sQuery(id+"F0.wireOp",EDGE,"E0")])]}),makeQuery(id+"F7.opExtrude","SWEPT_FACE",FACE,{"disambiguationData":[OSD([sQuery(id+"F6.wireOp",EDGE,"86e64e75-ce93-4209-b98e-9b8fc518f516.4")])]})]});
            var Q23;
            Q23=makeQuery(id+"F7.boolean.opBoolean","INTERSECT",EDGE,{"disambiguationData":[OD(0.0)],"derivedFrom":[makeQuery(id+"F1.opExtrude","SWEPT_FACE",FACE,{"disambiguationData":[OSD([sQuery(id+"F0.wireOp",EDGE,"E0")])]}),makeQuery(id+"F7.opExtrude","SWEPT_FACE",FACE,{"disambiguationData":[OSD([sQuery(id+"F6.wireOp",EDGE,"86e64e75-ce93-4209-b98e-9b8fc518f516.3")])]})]});
            var Q24;
            Q24=makeQuery(id+"F7.boolean.opBoolean","INTERSECT",EDGE,{"disambiguationData":[OD(0.0)],"derivedFrom":[makeQuery(id+"F1.opExtrude","SWEPT_FACE",FACE,{"disambiguationData":[OSD([sQuery(id+"F0.wireOp",EDGE,"E0")])]}),makeQuery(id+"F7.opExtrude","SWEPT_FACE",FACE,{"disambiguationData":[OSD([sQuery(id+"F6.wireOp",EDGE,"09c30c40-169e-4e38-bf91-241d7524808d.0")])]})]});
            var Q25;
            Q25=makeQuery(id+"F7.boolean.opBoolean","INTERSECT",EDGE,{"disambiguationData":[OD(0.0)],"derivedFrom":[makeQuery(id+"F1.opExtrude","SWEPT_FACE",FACE,{"disambiguationData":[OSD([sQuery(id+"F0.wireOp",EDGE,"E0")])]}),makeQuery(id+"F7.opExtrude","SWEPT_FACE",FACE,{"disambiguationData":[OSD([sQuery(id+"F6.wireOp",EDGE,"09c30c40-169e-4e38-bf91-241d7524808d.4")])]})]});
            var Q26;
            Q26=makeQuery(id+"F7.boolean.opBoolean","INTERSECT",EDGE,{"disambiguationData":[OD(0.0)],"derivedFrom":[makeQuery(id+"F1.opExtrude","SWEPT_FACE",FACE,{"disambiguationData":[OSD([sQuery(id+"F0.wireOp",EDGE,"E0")])]}),makeQuery(id+"F7.opExtrude","SWEPT_FACE",FACE,{"disambiguationData":[OSD([sQuery(id+"F6.wireOp",EDGE,"09c30c40-169e-4e38-bf91-241d7524808d.3")])]})]});
            var Q27;
            Q27=makeQuery(id+"F7.boolean.opBoolean","INTERSECT",EDGE,{"disambiguationData":[OD(0.0)],"derivedFrom":[makeQuery(id+"F1.opExtrude","SWEPT_FACE",FACE,{"disambiguationData":[OSD([sQuery(id+"F0.wireOp",EDGE,"E0")])]}),makeQuery(id+"F7.opExtrude","SWEPT_FACE",FACE,{"disambiguationData":[OSD([sQuery(id+"F6.wireOp",EDGE,"09c30c40-169e-4e38-bf91-241d7524808d.2")])]})]});
            var Q28;
            Q28=makeQuery(id+"F7.boolean.opBoolean","INTERSECT",EDGE,{"disambiguationData":[OD(0.0)],"derivedFrom":[makeQuery(id+"F1.opExtrude","SWEPT_FACE",FACE,{"disambiguationData":[OSD([sQuery(id+"F0.wireOp",EDGE,"E0")])]}),makeQuery(id+"F7.opExtrude","SWEPT_FACE",FACE,{"disambiguationData":[OSD([sQuery(id+"F6.wireOp",EDGE,"09c30c40-169e-4e38-bf91-241d7524808d.1")])]})]});
            var Q29;
            Q29=makeQuery(id+"F7.boolean.opBoolean","INTERSECT",EDGE,{"disambiguationData":[OD(0.0)],"derivedFrom":[makeQuery(id+"F1.opExtrude","SWEPT_FACE",FACE,{"disambiguationData":[OSD([sQuery(id+"F0.wireOp",EDGE,"E0")])]}),makeQuery(id+"F7.opExtrude","SWEPT_FACE",FACE,{"disambiguationData":[OSD([sQuery(id+"F6.wireOp",EDGE,"cfdfa16a-de7a-4601-9022-5211aa514822.2")])]})]});
            var Q30;
            Q30=makeQuery(id+"F7.boolean.opBoolean","INTERSECT",EDGE,{"disambiguationData":[OD(0.0)],"derivedFrom":[makeQuery(id+"F1.opExtrude","SWEPT_FACE",FACE,{"disambiguationData":[OSD([sQuery(id+"F0.wireOp",EDGE,"E0")])]}),makeQuery(id+"F7.opExtrude","SWEPT_FACE",FACE,{"disambiguationData":[OSD([sQuery(id+"F6.wireOp",EDGE,"cfdfa16a-de7a-4601-9022-5211aa514822.1")])]})]});
            var Q31;
            Q31=makeQuery(id+"F7.boolean.opBoolean","INTERSECT",EDGE,{"disambiguationData":[OD(0.0)],"derivedFrom":[makeQuery(id+"F1.opExtrude","SWEPT_FACE",FACE,{"disambiguationData":[OSD([sQuery(id+"F0.wireOp",EDGE,"E0")])]}),makeQuery(id+"F7.opExtrude","SWEPT_FACE",FACE,{"disambiguationData":[OSD([sQuery(id+"F6.wireOp",EDGE,"cfdfa16a-de7a-4601-9022-5211aa514822.0")])]})]});
            var Q32;
            Q32=makeQuery(id+"F7.boolean.opBoolean","INTERSECT",EDGE,{"disambiguationData":[OD(0.0)],"derivedFrom":[makeQuery(id+"F1.opExtrude","SWEPT_FACE",FACE,{"disambiguationData":[OSD([sQuery(id+"F0.wireOp",EDGE,"E0")])]}),makeQuery(id+"F7.opExtrude","SWEPT_FACE",FACE,{"disambiguationData":[OSD([sQuery(id+"F6.wireOp",EDGE,"cfdfa16a-de7a-4601-9022-5211aa514822.5")])]})]});
            var Q33;
            Q33=makeQuery(id+"F7.boolean.opBoolean","INTERSECT",EDGE,{"disambiguationData":[OD(0.0)],"derivedFrom":[makeQuery(id+"F1.opExtrude","SWEPT_FACE",FACE,{"disambiguationData":[OSD([sQuery(id+"F0.wireOp",EDGE,"E0")])]}),makeQuery(id+"F7.opExtrude","SWEPT_FACE",FACE,{"disambiguationData":[OSD([sQuery(id+"F6.wireOp",EDGE,"cfdfa16a-de7a-4601-9022-5211aa514822.3")])]})]});
            var Q34;
            Q34=makeQuery(id+"F5.boolean.opBoolean","INTERSECT",EDGE,{"disambiguationData":[OD(1.0)],"derivedFrom":[makeQuery(id+"F1.opExtrude","SWEPT_FACE",FACE,{"disambiguationData":[OSD([sQuery(id+"F0.wireOp",EDGE,"E0")])]}),makeQuery(id+"F5.opExtrude","SWEPT_FACE",FACE,{"disambiguationData":[OSD([sQuery(id+"F4.wireOp",EDGE,"E4.3")])]})]});
            var Q35;
            Q35=makeQuery(id+"F5.boolean.opBoolean","INTERSECT",EDGE,{"disambiguationData":[OD(1.0)],"derivedFrom":[makeQuery(id+"F1.opExtrude","SWEPT_FACE",FACE,{"disambiguationData":[OSD([sQuery(id+"F0.wireOp",EDGE,"E0")])]}),makeQuery(id+"F5.opExtrude","SWEPT_FACE",FACE,{"disambiguationData":[OSD([sQuery(id+"F4.wireOp",EDGE,"E4.4")])]})]});
            var Q36;
            Q36=makeQuery(id+"F5.boolean.opBoolean","INTERSECT",EDGE,{"disambiguationData":[OD(1.0)],"derivedFrom":[makeQuery(id+"F1.opExtrude","SWEPT_FACE",FACE,{"disambiguationData":[OSD([sQuery(id+"F0.wireOp",EDGE,"E0")])]}),makeQuery(id+"F5.opExtrude","SWEPT_FACE",FACE,{"disambiguationData":[OSD([sQuery(id+"F4.wireOp",EDGE,"E4.5")])]})]});
            var Q37;
            Q37=makeQuery(id+"F5.boolean.opBoolean","INTERSECT",EDGE,{"disambiguationData":[OD(1.0)],"derivedFrom":[makeQuery(id+"F1.opExtrude","SWEPT_FACE",FACE,{"disambiguationData":[OSD([sQuery(id+"F0.wireOp",EDGE,"E0")])]}),makeQuery(id+"F5.opExtrude","SWEPT_FACE",FACE,{"disambiguationData":[OSD([sQuery(id+"F4.wireOp",EDGE,"E4.0")])]})]});
            var Q38;
            Q38=makeQuery(id+"F5.boolean.opBoolean","INTERSECT",EDGE,{"disambiguationData":[OD(1.0)],"derivedFrom":[makeQuery(id+"F1.opExtrude","SWEPT_FACE",FACE,{"disambiguationData":[OSD([sQuery(id+"F0.wireOp",EDGE,"E0")])]}),makeQuery(id+"F5.opExtrude","SWEPT_FACE",FACE,{"disambiguationData":[OSD([sQuery(id+"F4.wireOp",EDGE,"E4.1")])]})]});
            var Q39;
            Q39=makeQuery(id+"F5.boolean.opBoolean","INTERSECT",EDGE,{"disambiguationData":[OD(1.0)],"derivedFrom":[makeQuery(id+"F1.opExtrude","SWEPT_FACE",FACE,{"disambiguationData":[OSD([sQuery(id+"F0.wireOp",EDGE,"E0")])]}),makeQuery(id+"F5.opExtrude","SWEPT_FACE",FACE,{"disambiguationData":[OSD([sQuery(id+"F4.wireOp",EDGE,"E4.2")])]})]});
            var Q40;
            Q40=makeQuery(id+"F5.boolean.opBoolean","INTERSECT",EDGE,{"disambiguationData":[OD(1.0)],"derivedFrom":[makeQuery(id+"F1.opExtrude","SWEPT_FACE",FACE,{"disambiguationData":[OSD([sQuery(id+"F0.wireOp",EDGE,"E0")])]}),makeQuery(id+"F5.opExtrude","SWEPT_FACE",FACE,{"disambiguationData":[OSD([sQuery(id+"F4.wireOp",EDGE,"E5.0.1.1")])]})]});
            var Q41;
            Q41=makeQuery(id+"F5.boolean.opBoolean","INTERSECT",EDGE,{"disambiguationData":[OD(1.0)],"derivedFrom":[makeQuery(id+"F1.opExtrude","SWEPT_FACE",FACE,{"disambiguationData":[OSD([sQuery(id+"F0.wireOp",EDGE,"E0")])]}),makeQuery(id+"F5.opExtrude","SWEPT_FACE",FACE,{"disambiguationData":[OSD([sQuery(id+"F4.wireOp",EDGE,"E5.0.1.7")])]})]});
            var Q42;
            Q42=makeQuery(id+"F5.boolean.opBoolean","INTERSECT",EDGE,{"disambiguationData":[OD(1.0)],"derivedFrom":[makeQuery(id+"F1.opExtrude","SWEPT_FACE",FACE,{"disambiguationData":[OSD([sQuery(id+"F0.wireOp",EDGE,"E0")])]}),makeQuery(id+"F5.opExtrude","SWEPT_FACE",FACE,{"disambiguationData":[OSD([sQuery(id+"F4.wireOp",EDGE,"E5.0.1.0")])]})]});
            var Q43;
            Q43=makeQuery(id+"F5.boolean.opBoolean","INTERSECT",EDGE,{"disambiguationData":[OD(1.0)],"derivedFrom":[makeQuery(id+"F1.opExtrude","SWEPT_FACE",FACE,{"disambiguationData":[OSD([sQuery(id+"F0.wireOp",EDGE,"E0")])]}),makeQuery(id+"F5.opExtrude","SWEPT_FACE",FACE,{"disambiguationData":[OSD([sQuery(id+"F4.wireOp",EDGE,"E5.0.1.4")])]})]});
            var Q44;
            Q44=makeQuery(id+"F5.boolean.opBoolean","INTERSECT",EDGE,{"disambiguationData":[OD(1.0)],"derivedFrom":[makeQuery(id+"F1.opExtrude","SWEPT_FACE",FACE,{"disambiguationData":[OSD([sQuery(id+"F0.wireOp",EDGE,"E0")])]}),makeQuery(id+"F5.opExtrude","SWEPT_FACE",FACE,{"disambiguationData":[OSD([sQuery(id+"F4.wireOp",EDGE,"E5.0.1.3")])]})]});
            var Q45;
            Q45=makeQuery(id+"F5.boolean.opBoolean","INTERSECT",EDGE,{"disambiguationData":[OD(1.0)],"derivedFrom":[makeQuery(id+"F1.opExtrude","SWEPT_FACE",FACE,{"disambiguationData":[OSD([sQuery(id+"F0.wireOp",EDGE,"E0")])]}),makeQuery(id+"F5.opExtrude","SWEPT_FACE",FACE,{"disambiguationData":[OSD([sQuery(id+"F4.wireOp",EDGE,"E5.0.1.2")])]})]});
            var Q46;
            Q46=makeQuery(id+"F5.boolean.opBoolean","INTERSECT",EDGE,{"disambiguationData":[OD(1.0)],"derivedFrom":[makeQuery(id+"F1.opExtrude","SWEPT_FACE",FACE,{"disambiguationData":[OSD([sQuery(id+"F0.wireOp",EDGE,"E0")])]}),makeQuery(id+"F5.opExtrude","SWEPT_FACE",FACE,{"disambiguationData":[OSD([sQuery(id+"F4.wireOp",EDGE,"E5.0.2.1")])]})]});
            var Q47;
            Q47=makeQuery(id+"F5.boolean.opBoolean","INTERSECT",EDGE,{"disambiguationData":[OD(1.0)],"derivedFrom":[makeQuery(id+"F1.opExtrude","SWEPT_FACE",FACE,{"disambiguationData":[OSD([sQuery(id+"F0.wireOp",EDGE,"E0")])]}),makeQuery(id+"F5.opExtrude","SWEPT_FACE",FACE,{"disambiguationData":[OSD([sQuery(id+"F4.wireOp",EDGE,"E5.0.2.7")])]})]});
            var Q48;
            Q48=makeQuery(id+"F5.boolean.opBoolean","INTERSECT",EDGE,{"disambiguationData":[OD(1.0)],"derivedFrom":[makeQuery(id+"F1.opExtrude","SWEPT_FACE",FACE,{"disambiguationData":[OSD([sQuery(id+"F0.wireOp",EDGE,"E0")])]}),makeQuery(id+"F5.opExtrude","SWEPT_FACE",FACE,{"disambiguationData":[OSD([sQuery(id+"F4.wireOp",EDGE,"E5.0.2.0")])]})]});
            var Q49;
            Q49=makeQuery(id+"F5.boolean.opBoolean","INTERSECT",EDGE,{"disambiguationData":[OD(1.0)],"derivedFrom":[makeQuery(id+"F1.opExtrude","SWEPT_FACE",FACE,{"disambiguationData":[OSD([sQuery(id+"F0.wireOp",EDGE,"E0")])]}),makeQuery(id+"F5.opExtrude","SWEPT_FACE",FACE,{"disambiguationData":[OSD([sQuery(id+"F4.wireOp",EDGE,"E5.0.2.4")])]})]});
            var Q50;
            Q50=makeQuery(id+"F5.boolean.opBoolean","INTERSECT",EDGE,{"disambiguationData":[OD(1.0)],"derivedFrom":[makeQuery(id+"F1.opExtrude","SWEPT_FACE",FACE,{"disambiguationData":[OSD([sQuery(id+"F0.wireOp",EDGE,"E0")])]}),makeQuery(id+"F5.opExtrude","SWEPT_FACE",FACE,{"disambiguationData":[OSD([sQuery(id+"F4.wireOp",EDGE,"E5.0.2.3")])]})]});
            var Q51;
            Q51=makeQuery(id+"F5.boolean.opBoolean","INTERSECT",EDGE,{"disambiguationData":[OD(1.0)],"derivedFrom":[makeQuery(id+"F1.opExtrude","SWEPT_FACE",FACE,{"disambiguationData":[OSD([sQuery(id+"F0.wireOp",EDGE,"E0")])]}),makeQuery(id+"F5.opExtrude","SWEPT_FACE",FACE,{"disambiguationData":[OSD([sQuery(id+"F4.wireOp",EDGE,"E5.0.2.2")])]})]});
            var Q52;
            Q52=makeQuery(id+"F5.boolean.opBoolean","INTERSECT",EDGE,{"disambiguationData":[OD(1.0)],"derivedFrom":[makeQuery(id+"F1.opExtrude","SWEPT_FACE",FACE,{"disambiguationData":[OSD([sQuery(id+"F0.wireOp",EDGE,"E0")])]}),makeQuery(id+"F5.opExtrude","SWEPT_FACE",FACE,{"disambiguationData":[OSD([sQuery(id+"F4.wireOp",EDGE,"E5.0.3.1")])]})]});
            var Q53;
            Q53=makeQuery(id+"F5.boolean.opBoolean","INTERSECT",EDGE,{"disambiguationData":[OD(1.0)],"derivedFrom":[makeQuery(id+"F1.opExtrude","SWEPT_FACE",FACE,{"disambiguationData":[OSD([sQuery(id+"F0.wireOp",EDGE,"E0")])]}),makeQuery(id+"F5.opExtrude","SWEPT_FACE",FACE,{"disambiguationData":[OSD([sQuery(id+"F4.wireOp",EDGE,"E5.0.3.7")])]})]});
            var Q54;
            Q54=makeQuery(id+"F5.boolean.opBoolean","INTERSECT",EDGE,{"disambiguationData":[OD(1.0)],"derivedFrom":[makeQuery(id+"F1.opExtrude","SWEPT_FACE",FACE,{"disambiguationData":[OSD([sQuery(id+"F0.wireOp",EDGE,"E0")])]}),makeQuery(id+"F5.opExtrude","SWEPT_FACE",FACE,{"disambiguationData":[OSD([sQuery(id+"F4.wireOp",EDGE,"E5.0.3.0")])]})]});
            var Q55;
            Q55=makeQuery(id+"F5.boolean.opBoolean","INTERSECT",EDGE,{"disambiguationData":[OD(1.0)],"derivedFrom":[makeQuery(id+"F1.opExtrude","SWEPT_FACE",FACE,{"disambiguationData":[OSD([sQuery(id+"F0.wireOp",EDGE,"E0")])]}),makeQuery(id+"F5.opExtrude","SWEPT_FACE",FACE,{"disambiguationData":[OSD([sQuery(id+"F4.wireOp",EDGE,"E5.0.3.4")])]})]});
            var Q56;
            Q56=makeQuery(id+"F5.boolean.opBoolean","INTERSECT",EDGE,{"disambiguationData":[OD(1.0)],"derivedFrom":[makeQuery(id+"F1.opExtrude","SWEPT_FACE",FACE,{"disambiguationData":[OSD([sQuery(id+"F0.wireOp",EDGE,"E0")])]}),makeQuery(id+"F5.opExtrude","SWEPT_FACE",FACE,{"disambiguationData":[OSD([sQuery(id+"F4.wireOp",EDGE,"E5.0.3.3")])]})]});
            var Q57;
            Q57=makeQuery(id+"F5.boolean.opBoolean","INTERSECT",EDGE,{"disambiguationData":[OD(1.0)],"derivedFrom":[makeQuery(id+"F1.opExtrude","SWEPT_FACE",FACE,{"disambiguationData":[OSD([sQuery(id+"F0.wireOp",EDGE,"E0")])]}),makeQuery(id+"F5.opExtrude","SWEPT_FACE",FACE,{"disambiguationData":[OSD([sQuery(id+"F4.wireOp",EDGE,"E5.0.3.2")])]})]});
            var Q58;
            Q58=makeQuery(id+"F5.boolean.opBoolean","INTERSECT",EDGE,{"disambiguationData":[OD(1.0)],"derivedFrom":[makeQuery(id+"F1.opExtrude","SWEPT_FACE",FACE,{"disambiguationData":[OSD([sQuery(id+"F0.wireOp",EDGE,"E0")])]}),makeQuery(id+"F5.opExtrude","SWEPT_FACE",FACE,{"disambiguationData":[OSD([sQuery(id+"F4.wireOp",EDGE,"E5.0.4.1")])]})]});
            var Q59;
            Q59=makeQuery(id+"F5.boolean.opBoolean","INTERSECT",EDGE,{"disambiguationData":[OD(1.0)],"derivedFrom":[makeQuery(id+"F1.opExtrude","SWEPT_FACE",FACE,{"disambiguationData":[OSD([sQuery(id+"F0.wireOp",EDGE,"E0")])]}),makeQuery(id+"F5.opExtrude","SWEPT_FACE",FACE,{"disambiguationData":[OSD([sQuery(id+"F4.wireOp",EDGE,"E5.0.4.7")])]})]});
            var Q60;
            Q60=makeQuery(id+"F5.boolean.opBoolean","INTERSECT",EDGE,{"disambiguationData":[OD(1.0)],"derivedFrom":[makeQuery(id+"F1.opExtrude","SWEPT_FACE",FACE,{"disambiguationData":[OSD([sQuery(id+"F0.wireOp",EDGE,"E0")])]}),makeQuery(id+"F5.opExtrude","SWEPT_FACE",FACE,{"disambiguationData":[OSD([sQuery(id+"F4.wireOp",EDGE,"E5.0.4.0")])]})]});
            var Q61;
            Q61=makeQuery(id+"F5.boolean.opBoolean","INTERSECT",EDGE,{"disambiguationData":[OD(1.0)],"derivedFrom":[makeQuery(id+"F1.opExtrude","SWEPT_FACE",FACE,{"disambiguationData":[OSD([sQuery(id+"F0.wireOp",EDGE,"E0")])]}),makeQuery(id+"F5.opExtrude","SWEPT_FACE",FACE,{"disambiguationData":[OSD([sQuery(id+"F4.wireOp",EDGE,"E5.0.4.4")])]})]});
            var Q62;
            Q62=makeQuery(id+"F5.boolean.opBoolean","INTERSECT",EDGE,{"disambiguationData":[OD(1.0)],"derivedFrom":[makeQuery(id+"F1.opExtrude","SWEPT_FACE",FACE,{"disambiguationData":[OSD([sQuery(id+"F0.wireOp",EDGE,"E0")])]}),makeQuery(id+"F5.opExtrude","SWEPT_FACE",FACE,{"disambiguationData":[OSD([sQuery(id+"F4.wireOp",EDGE,"E5.0.4.3")])]})]});
            var Q63;
            Q63=makeQuery(id+"F5.boolean.opBoolean","INTERSECT",EDGE,{"disambiguationData":[OD(1.0)],"derivedFrom":[makeQuery(id+"F1.opExtrude","SWEPT_FACE",FACE,{"disambiguationData":[OSD([sQuery(id+"F0.wireOp",EDGE,"E0")])]}),makeQuery(id+"F5.opExtrude","SWEPT_FACE",FACE,{"disambiguationData":[OSD([sQuery(id+"F4.wireOp",EDGE,"E5.0.4.2")])]})]});
            var Q64;
            Q64=makeQuery(id+"F5.boolean.opBoolean","INTERSECT",EDGE,{"disambiguationData":[OD(1.0)],"derivedFrom":[makeQuery(id+"F1.opExtrude","SWEPT_FACE",FACE,{"disambiguationData":[OSD([sQuery(id+"F0.wireOp",EDGE,"E0")])]}),makeQuery(id+"F5.opExtrude","SWEPT_FACE",FACE,{"disambiguationData":[OSD([sQuery(id+"F4.wireOp",EDGE,"E5.0.5.1")])]})]});
            var Q65;
            Q65=makeQuery(id+"F5.boolean.opBoolean","INTERSECT",EDGE,{"disambiguationData":[OD(1.0)],"derivedFrom":[makeQuery(id+"F1.opExtrude","SWEPT_FACE",FACE,{"disambiguationData":[OSD([sQuery(id+"F0.wireOp",EDGE,"E0")])]}),makeQuery(id+"F5.opExtrude","SWEPT_FACE",FACE,{"disambiguationData":[OSD([sQuery(id+"F4.wireOp",EDGE,"E5.0.5.7")])]})]});
            var Q66;
            Q66=makeQuery(id+"F5.boolean.opBoolean","INTERSECT",EDGE,{"disambiguationData":[OD(1.0)],"derivedFrom":[makeQuery(id+"F1.opExtrude","SWEPT_FACE",FACE,{"disambiguationData":[OSD([sQuery(id+"F0.wireOp",EDGE,"E0")])]}),makeQuery(id+"F5.opExtrude","SWEPT_FACE",FACE,{"disambiguationData":[OSD([sQuery(id+"F4.wireOp",EDGE,"E5.0.5.0")])]})]});
            var Q67;
            Q67=makeQuery(id+"F5.boolean.opBoolean","INTERSECT",EDGE,{"disambiguationData":[OD(1.0)],"derivedFrom":[makeQuery(id+"F1.opExtrude","SWEPT_FACE",FACE,{"disambiguationData":[OSD([sQuery(id+"F0.wireOp",EDGE,"E0")])]}),makeQuery(id+"F5.opExtrude","SWEPT_FACE",FACE,{"disambiguationData":[OSD([sQuery(id+"F4.wireOp",EDGE,"E5.0.5.4")])]})]});
            var Q68;
            Q68=makeQuery(id+"F5.boolean.opBoolean","INTERSECT",EDGE,{"disambiguationData":[OD(1.0)],"derivedFrom":[makeQuery(id+"F1.opExtrude","SWEPT_FACE",FACE,{"disambiguationData":[OSD([sQuery(id+"F0.wireOp",EDGE,"E0")])]}),makeQuery(id+"F5.opExtrude","SWEPT_FACE",FACE,{"disambiguationData":[OSD([sQuery(id+"F4.wireOp",EDGE,"E5.0.5.3")])]})]});
            var Q69;
            Q69=makeQuery(id+"F5.boolean.opBoolean","INTERSECT",EDGE,{"disambiguationData":[OD(1.0)],"derivedFrom":[makeQuery(id+"F1.opExtrude","SWEPT_FACE",FACE,{"disambiguationData":[OSD([sQuery(id+"F0.wireOp",EDGE,"E0")])]}),makeQuery(id+"F5.opExtrude","SWEPT_FACE",FACE,{"disambiguationData":[OSD([sQuery(id+"F4.wireOp",EDGE,"E5.0.5.2")])]})]});
            var Q70;
            Q70=makeQuery(id+"F5.boolean.opBoolean","INTERSECT",EDGE,{"disambiguationData":[OD(1.0)],"derivedFrom":[makeQuery(id+"F1.opExtrude","SWEPT_FACE",FACE,{"disambiguationData":[OSD([sQuery(id+"F0.wireOp",EDGE,"E0")])]}),makeQuery(id+"F5.opExtrude","SWEPT_FACE",FACE,{"disambiguationData":[OSD([sQuery(id+"F4.wireOp",EDGE,"E5.0.6.1")])]})]});
            var Q71;
            Q71=makeQuery(id+"F5.boolean.opBoolean","INTERSECT",EDGE,{"disambiguationData":[OD(1.0)],"derivedFrom":[makeQuery(id+"F1.opExtrude","SWEPT_FACE",FACE,{"disambiguationData":[OSD([sQuery(id+"F0.wireOp",EDGE,"E0")])]}),makeQuery(id+"F5.opExtrude","SWEPT_FACE",FACE,{"disambiguationData":[OSD([sQuery(id+"F4.wireOp",EDGE,"E5.0.6.7")])]})]});
            var Q72;
            Q72=makeQuery(id+"F5.boolean.opBoolean","INTERSECT",EDGE,{"disambiguationData":[OD(1.0)],"derivedFrom":[makeQuery(id+"F1.opExtrude","SWEPT_FACE",FACE,{"disambiguationData":[OSD([sQuery(id+"F0.wireOp",EDGE,"E0")])]}),makeQuery(id+"F5.opExtrude","SWEPT_FACE",FACE,{"disambiguationData":[OSD([sQuery(id+"F4.wireOp",EDGE,"E5.0.6.0")])]})]});
            var Q73;
            Q73=makeQuery(id+"F5.boolean.opBoolean","INTERSECT",EDGE,{"disambiguationData":[OD(1.0)],"derivedFrom":[makeQuery(id+"F1.opExtrude","SWEPT_FACE",FACE,{"disambiguationData":[OSD([sQuery(id+"F0.wireOp",EDGE,"E0")])]}),makeQuery(id+"F5.opExtrude","SWEPT_FACE",FACE,{"disambiguationData":[OSD([sQuery(id+"F4.wireOp",EDGE,"E5.0.6.4")])]})]});
            var Q74;
            Q74=makeQuery(id+"F5.boolean.opBoolean","INTERSECT",EDGE,{"disambiguationData":[OD(1.0)],"derivedFrom":[makeQuery(id+"F1.opExtrude","SWEPT_FACE",FACE,{"disambiguationData":[OSD([sQuery(id+"F0.wireOp",EDGE,"E0")])]}),makeQuery(id+"F5.opExtrude","SWEPT_FACE",FACE,{"disambiguationData":[OSD([sQuery(id+"F4.wireOp",EDGE,"E5.0.6.3")])]})]});
            var Q75;
            Q75=makeQuery(id+"F5.boolean.opBoolean","INTERSECT",EDGE,{"disambiguationData":[OD(1.0)],"derivedFrom":[makeQuery(id+"F1.opExtrude","SWEPT_FACE",FACE,{"disambiguationData":[OSD([sQuery(id+"F0.wireOp",EDGE,"E0")])]}),makeQuery(id+"F5.opExtrude","SWEPT_FACE",FACE,{"disambiguationData":[OSD([sQuery(id+"F4.wireOp",EDGE,"E5.0.6.2")])]})]});
            fillet(context, id + "F16", {"entities" : qUnion([Q0, Q1, Q2, Q3, Q4, Q5, Q6, Q7, Q8, Q9, Q10, Q11, Q12, Q13, Q14, Q15, Q16, Q17, Q18, Q19, Q20, Q21, Q22, Q23, Q24, Q25, Q26, Q27, Q28, Q29, Q30, Q31, Q32, Q33, Q34, Q35, Q36, Q37, Q38, Q39, Q40, Q41, Q42, Q43, Q44, Q45, Q46, Q47, Q48, Q49, Q50, Q51, Q52, Q53, Q54, Q55, Q56, Q57, Q58, Q59, Q60, Q61, Q62, Q63, Q64, Q65, Q66, Q67, Q68, Q69, Q70, Q71, Q72, Q73, Q74, Q75]), "radius" : 0.7 * mm, "tangentPropagation" : true, "defaultsChanged" : true, "vertexSettings" : [], "allowEdgeOverflow" : false});
        }
        {
            var Q0;
            Q0=makeQuery(id+"F7.boolean.opBoolean","INTERSECT",EDGE,{"disambiguationData":[OD(0.0)],"derivedFrom":[makeQuery(id+"F1.opExtrude","SWEPT_FACE",FACE,{"disambiguationData":[OSD([sQuery(id+"F0.wireOp",EDGE,"E0")])]}),makeQuery(id+"F7.opExtrude","SWEPT_FACE",FACE,{"disambiguationData":[OSD([sQuery(id+"F6.wireOp",EDGE,"E11.2")])]})]});
            var Q1;
            Q1=makeQuery(id+"F7.boolean.opBoolean","INTERSECT",EDGE,{"disambiguationData":[OD(0.0)],"derivedFrom":[makeQuery(id+"F1.opExtrude","SWEPT_FACE",FACE,{"disambiguationData":[OSD([sQuery(id+"F0.wireOp",EDGE,"E0")])]}),makeQuery(id+"F7.opExtrude","SWEPT_FACE",FACE,{"disambiguationData":[OSD([sQuery(id+"F6.wireOp",EDGE,"E11.1")])]})]});
            var Q2;
            Q2=makeQuery(id+"F7.boolean.opBoolean","INTERSECT",EDGE,{"disambiguationData":[OD(0.0)],"derivedFrom":[makeQuery(id+"F1.opExtrude","SWEPT_FACE",FACE,{"disambiguationData":[OSD([sQuery(id+"F0.wireOp",EDGE,"E0")])]}),makeQuery(id+"F7.opExtrude","SWEPT_FACE",FACE,{"disambiguationData":[OSD([sQuery(id+"F6.wireOp",EDGE,"E11.0")])]})]});
            var Q3;
            Q3=makeQuery(id+"F7.boolean.opBoolean","INTERSECT",EDGE,{"disambiguationData":[OD(0.0)],"derivedFrom":[makeQuery(id+"F1.opExtrude","SWEPT_FACE",FACE,{"disambiguationData":[OSD([sQuery(id+"F0.wireOp",EDGE,"E0")])]}),makeQuery(id+"F7.opExtrude","SWEPT_FACE",FACE,{"disambiguationData":[OSD([sQuery(id+"F6.wireOp",EDGE,"E8.4")])]})]});
            var Q4;
            Q4=makeQuery(id+"F7.boolean.opBoolean","INTERSECT",EDGE,{"disambiguationData":[OD(0.0)],"derivedFrom":[makeQuery(id+"F1.opExtrude","SWEPT_FACE",FACE,{"disambiguationData":[OSD([sQuery(id+"F0.wireOp",EDGE,"E0")])]}),makeQuery(id+"F7.opExtrude","SWEPT_FACE",FACE,{"disambiguationData":[OSD([sQuery(id+"F6.wireOp",EDGE,"E8.3")])]})]});
            var Q5;
            Q5=makeQuery(id+"F7.boolean.opBoolean","INTERSECT",EDGE,{"disambiguationData":[OD(0.0)],"derivedFrom":[makeQuery(id+"F1.opExtrude","SWEPT_FACE",FACE,{"disambiguationData":[OSD([sQuery(id+"F0.wireOp",EDGE,"E0")])]}),makeQuery(id+"F7.opExtrude","SWEPT_FACE",FACE,{"disambiguationData":[OSD([sQuery(id+"F6.wireOp",EDGE,"E8.2")])]})]});
            var Q6;
            Q6=makeQuery(id+"F10.boolean.opBoolean","INTERSECT",EDGE,{"disambiguationData":[OD(0.0)],"derivedFrom":[makeQuery(id+"F1.opExtrude","SWEPT_FACE",FACE,{"disambiguationData":[OSD([sQuery(id+"F0.wireOp",EDGE,"E0")])]}),makeQuery(id+"F10.opExtrude","SWEPT_FACE",FACE,{"disambiguationData":[OSD([sQuery(id+"F9.wireOp",EDGE,"E30")])]})]});
            var Q7;
            Q7=makeQuery(id+"F10.boolean.opBoolean","INTERSECT",EDGE,{"disambiguationData":[OD(1.0)],"derivedFrom":[makeQuery(id+"F1.opExtrude","SWEPT_FACE",FACE,{"disambiguationData":[OSD([sQuery(id+"F0.wireOp",EDGE,"E0")])]}),makeQuery(id+"F10.opExtrude","SWEPT_FACE",FACE,{"disambiguationData":[OSD([sQuery(id+"F9.wireOp",EDGE,"E24.3")])]})]});
            var Q8;
            Q8=makeQuery(id+"F10.boolean.opBoolean","INTERSECT",EDGE,{"disambiguationData":[OD(1.0)],"derivedFrom":[makeQuery(id+"F1.opExtrude","SWEPT_FACE",FACE,{"disambiguationData":[OSD([sQuery(id+"F0.wireOp",EDGE,"E0")])]}),makeQuery(id+"F10.opExtrude","SWEPT_FACE",FACE,{"disambiguationData":[OSD([sQuery(id+"F9.wireOp",EDGE,"E29")])]})]});
            var Q9;
            Q9=makeQuery(id+"F10.boolean.opBoolean","INTERSECT",EDGE,{"disambiguationData":[OD(1.0)],"derivedFrom":[makeQuery(id+"F1.opExtrude","SWEPT_FACE",FACE,{"disambiguationData":[OSD([sQuery(id+"F0.wireOp",EDGE,"E0")])]}),makeQuery(id+"F10.opExtrude","SWEPT_FACE",FACE,{"disambiguationData":[OSD([sQuery(id+"F9.wireOp",EDGE,"E26"),sQuery(id+"F9.wireOp",EDGE,"E27")])]})]});
            var Q10;
            Q10=makeQuery(id+"F10.boolean.opBoolean","INTERSECT",EDGE,{"disambiguationData":[OD(1.0)],"derivedFrom":[makeQuery(id+"F1.opExtrude","SWEPT_FACE",FACE,{"disambiguationData":[OSD([sQuery(id+"F0.wireOp",EDGE,"E0")])]}),makeQuery(id+"F10.opExtrude","SWEPT_FACE",FACE,{"disambiguationData":[OSD([sQuery(id+"F9.wireOp",EDGE,"E28")])]})]});
            var Q11;
            Q11=makeQuery(id+"F10.boolean.opBoolean","INTERSECT",EDGE,{"disambiguationData":[OD(1.0)],"derivedFrom":[makeQuery(id+"F1.opExtrude","SWEPT_FACE",FACE,{"disambiguationData":[OSD([sQuery(id+"F0.wireOp",EDGE,"E0")])]}),makeQuery(id+"F10.opExtrude","SWEPT_FACE",FACE,{"disambiguationData":[OSD([sQuery(id+"F9.wireOp",EDGE,"E14.3")])]})]});
            var Q12;
            Q12=makeQuery(id+"F10.boolean.opBoolean","INTERSECT",EDGE,{"disambiguationData":[OD(1.0)],"derivedFrom":[makeQuery(id+"F1.opExtrude","SWEPT_FACE",FACE,{"disambiguationData":[OSD([sQuery(id+"F0.wireOp",EDGE,"E0")])]}),makeQuery(id+"F10.opExtrude","SWEPT_FACE",FACE,{"disambiguationData":[OSD([sQuery(id+"F9.wireOp",EDGE,"E14.2")])]})]});
            var Q13;
            Q13=makeQuery(id+"F10.boolean.opBoolean","INTERSECT",EDGE,{"disambiguationData":[OD(1.0)],"derivedFrom":[makeQuery(id+"F1.opExtrude","SWEPT_FACE",FACE,{"disambiguationData":[OSD([sQuery(id+"F0.wireOp",EDGE,"E0")])]}),makeQuery(id+"F10.opExtrude","SWEPT_FACE",FACE,{"disambiguationData":[OSD([sQuery(id+"F9.wireOp",EDGE,"E14.1")])]})]});
            var Q14;
            Q14=makeQuery(id+"F10.boolean.opBoolean","INTERSECT",EDGE,{"disambiguationData":[OD(1.0)],"derivedFrom":[makeQuery(id+"F1.opExtrude","SWEPT_FACE",FACE,{"disambiguationData":[OSD([sQuery(id+"F0.wireOp",EDGE,"E0")])]}),makeQuery(id+"F10.opExtrude","SWEPT_FACE",FACE,{"disambiguationData":[OSD([sQuery(id+"F9.wireOp",EDGE,"E14.0")])]})]});
            var Q15;
            Q15=makeQuery(id+"F10.boolean.opBoolean","INTERSECT",EDGE,{"disambiguationData":[OD(1.0)],"derivedFrom":[makeQuery(id+"F1.opExtrude","SWEPT_FACE",FACE,{"disambiguationData":[OSD([sQuery(id+"F0.wireOp",EDGE,"E0")])]}),makeQuery(id+"F10.opExtrude","SWEPT_FACE",FACE,{"disambiguationData":[OSD([sQuery(id+"F9.wireOp",EDGE,"E14.5")])]})]});
            var Q16;
            Q16=makeQuery(id+"F10.boolean.opBoolean","INTERSECT",EDGE,{"disambiguationData":[OD(1.0)],"derivedFrom":[makeQuery(id+"F1.opExtrude","SWEPT_FACE",FACE,{"disambiguationData":[OSD([sQuery(id+"F0.wireOp",EDGE,"E0")])]}),makeQuery(id+"F10.opExtrude","SWEPT_FACE",FACE,{"disambiguationData":[OSD([sQuery(id+"F9.wireOp",EDGE,"E14.4")])]})]});
            var Q17;
            Q17=makeQuery(id+"F10.boolean.opBoolean","INTERSECT",EDGE,{"disambiguationData":[OD(1.0)],"derivedFrom":[makeQuery(id+"F1.opExtrude","SWEPT_FACE",FACE,{"disambiguationData":[OSD([sQuery(id+"F0.wireOp",EDGE,"E0")])]}),makeQuery(id+"F10.opExtrude","SWEPT_FACE",FACE,{"disambiguationData":[OSD([sQuery(id+"F9.wireOp",EDGE,"E15.0.1.6")])]})]});
            var Q18;
            Q18=makeQuery(id+"F10.boolean.opBoolean","INTERSECT",EDGE,{"disambiguationData":[OD(1.0)],"derivedFrom":[makeQuery(id+"F1.opExtrude","SWEPT_FACE",FACE,{"disambiguationData":[OSD([sQuery(id+"F0.wireOp",EDGE,"E0")])]}),makeQuery(id+"F10.opExtrude","SWEPT_FACE",FACE,{"disambiguationData":[OSD([sQuery(id+"F9.wireOp",EDGE,"E15.0.1.2")])]})]});
            var Q19;
            Q19=makeQuery(id+"F10.boolean.opBoolean","INTERSECT",EDGE,{"disambiguationData":[OD(1.0)],"derivedFrom":[makeQuery(id+"F1.opExtrude","SWEPT_FACE",FACE,{"disambiguationData":[OSD([sQuery(id+"F0.wireOp",EDGE,"E0")])]}),makeQuery(id+"F10.opExtrude","SWEPT_FACE",FACE,{"disambiguationData":[OSD([sQuery(id+"F9.wireOp",EDGE,"E15.0.1.3")])]})]});
            var Q20;
            Q20=makeQuery(id+"F10.boolean.opBoolean","INTERSECT",EDGE,{"disambiguationData":[OD(1.0)],"derivedFrom":[makeQuery(id+"F1.opExtrude","SWEPT_FACE",FACE,{"disambiguationData":[OSD([sQuery(id+"F0.wireOp",EDGE,"E0")])]}),makeQuery(id+"F10.opExtrude","SWEPT_FACE",FACE,{"disambiguationData":[OSD([sQuery(id+"F9.wireOp",EDGE,"E30")])]})]});
            var Q21;
            Q21=makeQuery(id+"F7.boolean.opBoolean","INTERSECT",EDGE,{"disambiguationData":[OD(1.0)],"derivedFrom":[makeQuery(id+"F1.opExtrude","SWEPT_FACE",FACE,{"disambiguationData":[OSD([sQuery(id+"F0.wireOp",EDGE,"E0")])]}),makeQuery(id+"F7.opExtrude","SWEPT_FACE",FACE,{"disambiguationData":[OSD([sQuery(id+"F6.wireOp",EDGE,"E11.0")])]})]});
            var Q22;
            Q22=makeQuery(id+"F7.boolean.opBoolean","INTERSECT",EDGE,{"disambiguationData":[OD(1.0)],"derivedFrom":[makeQuery(id+"F1.opExtrude","SWEPT_FACE",FACE,{"disambiguationData":[OSD([sQuery(id+"F0.wireOp",EDGE,"E0")])]}),makeQuery(id+"F7.opExtrude","SWEPT_FACE",FACE,{"disambiguationData":[OSD([sQuery(id+"F6.wireOp",EDGE,"E11.5")])]})]});
            var Q23;
            Q23=makeQuery(id+"F7.boolean.opBoolean","INTERSECT",EDGE,{"disambiguationData":[OD(1.0)],"derivedFrom":[makeQuery(id+"F1.opExtrude","SWEPT_FACE",FACE,{"disambiguationData":[OSD([sQuery(id+"F0.wireOp",EDGE,"E0")])]}),makeQuery(id+"F7.opExtrude","SWEPT_FACE",FACE,{"disambiguationData":[OSD([sQuery(id+"F6.wireOp",EDGE,"E11.4")])]})]});
            var Q24;
            Q24=makeQuery(id+"F7.boolean.opBoolean","INTERSECT",EDGE,{"disambiguationData":[OD(1.0)],"derivedFrom":[makeQuery(id+"F1.opExtrude","SWEPT_FACE",FACE,{"disambiguationData":[OSD([sQuery(id+"F0.wireOp",EDGE,"E0")])]}),makeQuery(id+"F7.opExtrude","SWEPT_FACE",FACE,{"disambiguationData":[OSD([sQuery(id+"F6.wireOp",EDGE,"E11.3")])]})]});
            var Q25;
            Q25=makeQuery(id+"F7.boolean.opBoolean","INTERSECT",EDGE,{"disambiguationData":[OD(1.0)],"derivedFrom":[makeQuery(id+"F1.opExtrude","SWEPT_FACE",FACE,{"disambiguationData":[OSD([sQuery(id+"F0.wireOp",EDGE,"E0")])]}),makeQuery(id+"F7.opExtrude","SWEPT_FACE",FACE,{"disambiguationData":[OSD([sQuery(id+"F6.wireOp",EDGE,"E11.2")])]})]});
            var Q26;
            Q26=makeQuery(id+"F7.boolean.opBoolean","INTERSECT",EDGE,{"disambiguationData":[OD(1.0)],"derivedFrom":[makeQuery(id+"F1.opExtrude","SWEPT_FACE",FACE,{"disambiguationData":[OSD([sQuery(id+"F0.wireOp",EDGE,"E0")])]}),makeQuery(id+"F7.opExtrude","SWEPT_FACE",FACE,{"disambiguationData":[OSD([sQuery(id+"F6.wireOp",EDGE,"E11.1")])]})]});
            var Q27;
            Q27=makeQuery(id+"F7.boolean.opBoolean","INTERSECT",EDGE,{"disambiguationData":[OD(1.0)],"derivedFrom":[makeQuery(id+"F1.opExtrude","SWEPT_FACE",FACE,{"disambiguationData":[OSD([sQuery(id+"F0.wireOp",EDGE,"E0")])]}),makeQuery(id+"F7.opExtrude","SWEPT_FACE",FACE,{"disambiguationData":[OSD([sQuery(id+"F6.wireOp",EDGE,"E8.1")])]})]});
            var Q28;
            Q28=makeQuery(id+"F7.boolean.opBoolean","INTERSECT",EDGE,{"disambiguationData":[OD(1.0)],"derivedFrom":[makeQuery(id+"F1.opExtrude","SWEPT_FACE",FACE,{"disambiguationData":[OSD([sQuery(id+"F0.wireOp",EDGE,"E0")])]}),makeQuery(id+"F7.opExtrude","SWEPT_FACE",FACE,{"disambiguationData":[OSD([sQuery(id+"F6.wireOp",EDGE,"E8.2")])]})]});
            var Q29;
            Q29=makeQuery(id+"F7.boolean.opBoolean","INTERSECT",EDGE,{"disambiguationData":[OD(1.0)],"derivedFrom":[makeQuery(id+"F1.opExtrude","SWEPT_FACE",FACE,{"disambiguationData":[OSD([sQuery(id+"F0.wireOp",EDGE,"E0")])]}),makeQuery(id+"F7.opExtrude","SWEPT_FACE",FACE,{"disambiguationData":[OSD([sQuery(id+"F6.wireOp",EDGE,"E8.3")])]})]});
            var Q30;
            Q30=makeQuery(id+"F7.boolean.opBoolean","INTERSECT",EDGE,{"disambiguationData":[OD(1.0)],"derivedFrom":[makeQuery(id+"F1.opExtrude","SWEPT_FACE",FACE,{"disambiguationData":[OSD([sQuery(id+"F0.wireOp",EDGE,"E0")])]}),makeQuery(id+"F7.opExtrude","SWEPT_FACE",FACE,{"disambiguationData":[OSD([sQuery(id+"F6.wireOp",EDGE,"E8.4")])]})]});
            var Q31;
            Q31=makeQuery(id+"F7.boolean.opBoolean","INTERSECT",EDGE,{"disambiguationData":[OD(1.0)],"derivedFrom":[makeQuery(id+"F1.opExtrude","SWEPT_FACE",FACE,{"disambiguationData":[OSD([sQuery(id+"F0.wireOp",EDGE,"E0")])]}),makeQuery(id+"F7.opExtrude","SWEPT_FACE",FACE,{"disambiguationData":[OSD([sQuery(id+"F6.wireOp",EDGE,"E8.5")])]})]});
            var Q32;
            Q32=makeQuery(id+"F7.boolean.opBoolean","INTERSECT",EDGE,{"disambiguationData":[OD(1.0)],"derivedFrom":[makeQuery(id+"F1.opExtrude","SWEPT_FACE",FACE,{"disambiguationData":[OSD([sQuery(id+"F0.wireOp",EDGE,"E0")])]}),makeQuery(id+"F7.opExtrude","SWEPT_FACE",FACE,{"disambiguationData":[OSD([sQuery(id+"F6.wireOp",EDGE,"E8.0")])]})]});
            var Q33;
            Q33=makeQuery(id+"F7.boolean.opBoolean","INTERSECT",EDGE,{"disambiguationData":[OD(0.0)],"derivedFrom":[makeQuery(id+"F1.opExtrude","SWEPT_FACE",FACE,{"disambiguationData":[OSD([sQuery(id+"F0.wireOp",EDGE,"E0")])]}),makeQuery(id+"F7.opExtrude","SWEPT_FACE",FACE,{"disambiguationData":[OSD([sQuery(id+"F6.wireOp",EDGE,"E8.1")])]})]});
            var Q34;
            Q34=makeQuery(id+"F7.boolean.opBoolean","INTERSECT",EDGE,{"disambiguationData":[OD(0.0)],"derivedFrom":[makeQuery(id+"F1.opExtrude","SWEPT_FACE",FACE,{"disambiguationData":[OSD([sQuery(id+"F0.wireOp",EDGE,"E0")])]}),makeQuery(id+"F7.opExtrude","SWEPT_FACE",FACE,{"disambiguationData":[OSD([sQuery(id+"F6.wireOp",EDGE,"E11.5")])]})]});
            var Q35;
            Q35=makeQuery(id+"F7.boolean.opBoolean","INTERSECT",EDGE,{"disambiguationData":[OD(0.0)],"derivedFrom":[makeQuery(id+"F1.opExtrude","SWEPT_FACE",FACE,{"disambiguationData":[OSD([sQuery(id+"F0.wireOp",EDGE,"E0")])]}),makeQuery(id+"F7.opExtrude","SWEPT_FACE",FACE,{"disambiguationData":[OSD([sQuery(id+"F6.wireOp",EDGE,"E11.4")])]})]});
            var Q36;
            Q36=makeQuery(id+"F7.boolean.opBoolean","INTERSECT",EDGE,{"disambiguationData":[OD(0.0)],"derivedFrom":[makeQuery(id+"F1.opExtrude","SWEPT_FACE",FACE,{"disambiguationData":[OSD([sQuery(id+"F0.wireOp",EDGE,"E0")])]}),makeQuery(id+"F7.opExtrude","SWEPT_FACE",FACE,{"disambiguationData":[OSD([sQuery(id+"F6.wireOp",EDGE,"E11.3")])]})]});
            fillet(context, id + "F17", {"entities" : qUnion([Q0, Q1, Q2, Q3, Q4, Q5, Q6, Q7, Q8, Q9, Q10, Q11, Q12, Q13, Q14, Q15, Q16, Q17, Q18, Q19, Q20, Q21, Q22, Q23, Q24, Q25, Q26, Q27, Q28, Q29, Q30, Q31, Q32, Q33, Q34, Q35, Q36]), "tangentPropagation" : true, "radius" : 0.7 * mm, "defaultsChanged" : true, "vertexSettings" : [], "allowEdgeOverflow" : false});
        }
    });
